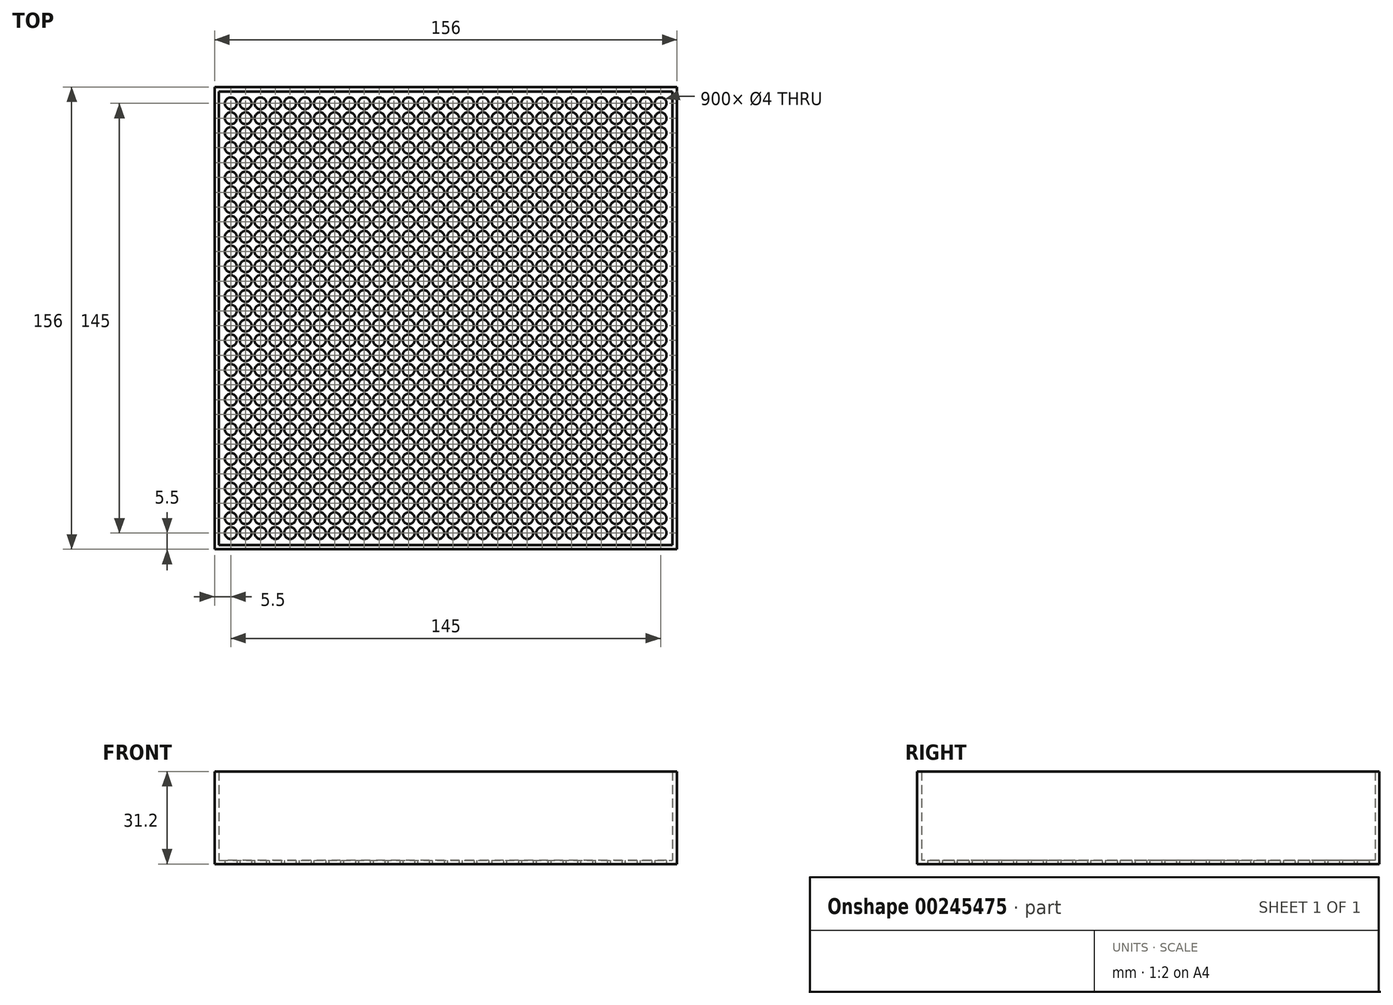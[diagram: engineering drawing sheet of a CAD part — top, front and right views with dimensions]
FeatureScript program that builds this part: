
annotation { "Feature Type Name" : "Feature", "Feature Type Description" : "" }
export const myFeature = defineFeature(function(context is Context, id is Id, definition is map)
    precondition{}
    {
        {
            var Q0;
            Q0=qCreatedBy(makeId("Top.planeOp"),FACE);
            var sketch = newSketch(context, id + "F0", { "sketchPlane" : qUnion([Q0])});
            skCircle(sketch, "E0", {"center": v(0, 0) * mm, "radius": 2 * mm});
            skCircle(sketch, "E1.0.1.0", {"center": v(0, 5) * mm, "radius": 2 * mm});
            skCircle(sketch, "E1.0.2.0", {"center": v(0, 10) * mm, "radius": 2 * mm});
            skCircle(sketch, "E1.0.3.0", {"center": v(0, 15) * mm, "radius": 2 * mm});
            skCircle(sketch, "E1.0.4.0", {"center": v(0, 20) * mm, "radius": 2 * mm});
            skCircle(sketch, "E1.0.5.0", {"center": v(0, 25) * mm, "radius": 2 * mm});
            skCircle(sketch, "E1.0.6.0", {"center": v(0, 30) * mm, "radius": 2 * mm});
            skCircle(sketch, "E1.0.7.0", {"center": v(0, 35) * mm, "radius": 2 * mm});
            skCircle(sketch, "E1.0.8.0", {"center": v(0, 40) * mm, "radius": 2 * mm});
            skCircle(sketch, "E1.0.9.0", {"center": v(0, 45) * mm, "radius": 2 * mm});
            skCircle(sketch, "E1.0.10.0", {"center": v(0, 50) * mm, "radius": 2 * mm});
            skCircle(sketch, "E1.0.11.0", {"center": v(0, 55) * mm, "radius": 2 * mm});
            skCircle(sketch, "E1.0.12.0", {"center": v(0, 60) * mm, "radius": 2 * mm});
            skCircle(sketch, "E1.0.13.0", {"center": v(0, 65) * mm, "radius": 2 * mm});
            skCircle(sketch, "E1.0.14.0", {"center": v(0, 70) * mm, "radius": 2 * mm});
            skCircle(sketch, "E1.0.15.0", {"center": v(0, 75) * mm, "radius": 2 * mm});
            skCircle(sketch, "E1.0.16.0", {"center": v(0, 80) * mm, "radius": 2 * mm});
            skCircle(sketch, "E1.0.17.0", {"center": v(0, 85) * mm, "radius": 2 * mm});
            skCircle(sketch, "E1.0.18.0", {"center": v(0, 90) * mm, "radius": 2 * mm});
            skCircle(sketch, "E1.0.19.0", {"center": v(0, 95) * mm, "radius": 2 * mm});
            skCircle(sketch, "E1.0.20.0", {"center": v(0, 100) * mm, "radius": 2 * mm});
            skCircle(sketch, "E1.0.21.0", {"center": v(0, 105) * mm, "radius": 2 * mm});
            skCircle(sketch, "E1.0.22.0", {"center": v(0, 110) * mm, "radius": 2 * mm});
            skCircle(sketch, "E1.0.23.0", {"center": v(0, 115) * mm, "radius": 2 * mm});
            skCircle(sketch, "E1.0.24.0", {"center": v(0, 120) * mm, "radius": 2 * mm});
            skCircle(sketch, "E1.0.25.0", {"center": v(0, 125) * mm, "radius": 2 * mm});
            skCircle(sketch, "E1.0.26.0", {"center": v(0, 130) * mm, "radius": 2 * mm});
            skCircle(sketch, "E1.0.27.0", {"center": v(0, 135) * mm, "radius": 2 * mm});
            skCircle(sketch, "E1.0.28.0", {"center": v(0, 140) * mm, "radius": 2 * mm});
            skCircle(sketch, "E1.0.29.0", {"center": v(0, 145) * mm, "radius": 2 * mm});
            skCircle(sketch, "E1.1.0.0", {"center": v(5, 0) * mm, "radius": 2 * mm});
            skCircle(sketch, "E1.1.1.0", {"center": v(5, 5) * mm, "radius": 2 * mm});
            skCircle(sketch, "E1.1.2.0", {"center": v(5, 10) * mm, "radius": 2 * mm});
            skCircle(sketch, "E1.1.3.0", {"center": v(5, 15) * mm, "radius": 2 * mm});
            skCircle(sketch, "E1.1.4.0", {"center": v(5, 20) * mm, "radius": 2 * mm});
            skCircle(sketch, "E1.1.5.0", {"center": v(5, 25) * mm, "radius": 2 * mm});
            skCircle(sketch, "E1.1.6.0", {"center": v(5, 30) * mm, "radius": 2 * mm});
            skCircle(sketch, "E1.1.7.0", {"center": v(5, 35) * mm, "radius": 2 * mm});
            skCircle(sketch, "E1.1.8.0", {"center": v(5, 40) * mm, "radius": 2 * mm});
            skCircle(sketch, "E1.1.9.0", {"center": v(5, 45) * mm, "radius": 2 * mm});
            skCircle(sketch, "E1.1.10.0", {"center": v(5, 50) * mm, "radius": 2 * mm});
            skCircle(sketch, "E1.1.11.0", {"center": v(5, 55) * mm, "radius": 2 * mm});
            skCircle(sketch, "E1.1.12.0", {"center": v(5, 60) * mm, "radius": 2 * mm});
            skCircle(sketch, "E1.1.13.0", {"center": v(5, 65) * mm, "radius": 2 * mm});
            skCircle(sketch, "E1.1.14.0", {"center": v(5, 70) * mm, "radius": 2 * mm});
            skCircle(sketch, "E1.1.15.0", {"center": v(5, 75) * mm, "radius": 2 * mm});
            skCircle(sketch, "E1.1.16.0", {"center": v(5, 80) * mm, "radius": 2 * mm});
            skCircle(sketch, "E1.1.17.0", {"center": v(5, 85) * mm, "radius": 2 * mm});
            skCircle(sketch, "E1.1.18.0", {"center": v(5, 90) * mm, "radius": 2 * mm});
            skCircle(sketch, "E1.1.19.0", {"center": v(5, 95) * mm, "radius": 2 * mm});
            skCircle(sketch, "E1.1.20.0", {"center": v(5, 100) * mm, "radius": 2 * mm});
            skCircle(sketch, "E1.1.21.0", {"center": v(5, 105) * mm, "radius": 2 * mm});
            skCircle(sketch, "E1.1.22.0", {"center": v(5, 110) * mm, "radius": 2 * mm});
            skCircle(sketch, "E1.1.23.0", {"center": v(5, 115) * mm, "radius": 2 * mm});
            skCircle(sketch, "E1.1.24.0", {"center": v(5, 120) * mm, "radius": 2 * mm});
            skCircle(sketch, "E1.1.25.0", {"center": v(5, 125) * mm, "radius": 2 * mm});
            skCircle(sketch, "E1.1.26.0", {"center": v(5, 130) * mm, "radius": 2 * mm});
            skCircle(sketch, "E1.1.27.0", {"center": v(5, 135) * mm, "radius": 2 * mm});
            skCircle(sketch, "E1.1.28.0", {"center": v(5, 140) * mm, "radius": 2 * mm});
            skCircle(sketch, "E1.1.29.0", {"center": v(5, 145) * mm, "radius": 2 * mm});
            skCircle(sketch, "E1.2.0.0", {"center": v(10, 0) * mm, "radius": 2 * mm});
            skCircle(sketch, "E1.2.1.0", {"center": v(10, 5) * mm, "radius": 2 * mm});
            skCircle(sketch, "E1.2.2.0", {"center": v(10, 10) * mm, "radius": 2 * mm});
            skCircle(sketch, "E1.2.3.0", {"center": v(10, 15) * mm, "radius": 2 * mm});
            skCircle(sketch, "E1.2.4.0", {"center": v(10, 20) * mm, "radius": 2 * mm});
            skCircle(sketch, "E1.2.5.0", {"center": v(10, 25) * mm, "radius": 2 * mm});
            skCircle(sketch, "E1.2.6.0", {"center": v(10, 30) * mm, "radius": 2 * mm});
            skCircle(sketch, "E1.2.7.0", {"center": v(10, 35) * mm, "radius": 2 * mm});
            skCircle(sketch, "E1.2.8.0", {"center": v(10, 40) * mm, "radius": 2 * mm});
            skCircle(sketch, "E1.2.9.0", {"center": v(10, 45) * mm, "radius": 2 * mm});
            skCircle(sketch, "E1.2.10.0", {"center": v(10, 50) * mm, "radius": 2 * mm});
            skCircle(sketch, "E1.2.11.0", {"center": v(10, 55) * mm, "radius": 2 * mm});
            skCircle(sketch, "E1.2.12.0", {"center": v(10, 60) * mm, "radius": 2 * mm});
            skCircle(sketch, "E1.2.13.0", {"center": v(10, 65) * mm, "radius": 2 * mm});
            skCircle(sketch, "E1.2.14.0", {"center": v(10, 70) * mm, "radius": 2 * mm});
            skCircle(sketch, "E1.2.15.0", {"center": v(10, 75) * mm, "radius": 2 * mm});
            skCircle(sketch, "E1.2.16.0", {"center": v(10, 80) * mm, "radius": 2 * mm});
            skCircle(sketch, "E1.2.17.0", {"center": v(10, 85) * mm, "radius": 2 * mm});
            skCircle(sketch, "E1.2.18.0", {"center": v(10, 90) * mm, "radius": 2 * mm});
            skCircle(sketch, "E1.2.19.0", {"center": v(10, 95) * mm, "radius": 2 * mm});
            skCircle(sketch, "E1.2.20.0", {"center": v(10, 100) * mm, "radius": 2 * mm});
            skCircle(sketch, "E1.2.21.0", {"center": v(10, 105) * mm, "radius": 2 * mm});
            skCircle(sketch, "E1.2.22.0", {"center": v(10, 110) * mm, "radius": 2 * mm});
            skCircle(sketch, "E1.2.23.0", {"center": v(10, 115) * mm, "radius": 2 * mm});
            skCircle(sketch, "E1.2.24.0", {"center": v(10, 120) * mm, "radius": 2 * mm});
            skCircle(sketch, "E1.2.25.0", {"center": v(10, 125) * mm, "radius": 2 * mm});
            skCircle(sketch, "E1.2.26.0", {"center": v(10, 130) * mm, "radius": 2 * mm});
            skCircle(sketch, "E1.2.27.0", {"center": v(10, 135) * mm, "radius": 2 * mm});
            skCircle(sketch, "E1.2.28.0", {"center": v(10, 140) * mm, "radius": 2 * mm});
            skCircle(sketch, "E1.2.29.0", {"center": v(10, 145) * mm, "radius": 2 * mm});
            skCircle(sketch, "E1.3.0.0", {"center": v(15, 0) * mm, "radius": 2 * mm});
            skCircle(sketch, "E1.3.1.0", {"center": v(15, 5) * mm, "radius": 2 * mm});
            skCircle(sketch, "E1.3.2.0", {"center": v(15, 10) * mm, "radius": 2 * mm});
            skCircle(sketch, "E1.3.3.0", {"center": v(15, 15) * mm, "radius": 2 * mm});
            skCircle(sketch, "E1.3.4.0", {"center": v(15, 20) * mm, "radius": 2 * mm});
            skCircle(sketch, "E1.3.5.0", {"center": v(15, 25) * mm, "radius": 2 * mm});
            skCircle(sketch, "E1.3.6.0", {"center": v(15, 30) * mm, "radius": 2 * mm});
            skCircle(sketch, "E1.3.7.0", {"center": v(15, 35) * mm, "radius": 2 * mm});
            skCircle(sketch, "E1.3.8.0", {"center": v(15, 40) * mm, "radius": 2 * mm});
            skCircle(sketch, "E1.3.9.0", {"center": v(15, 45) * mm, "radius": 2 * mm});
            skCircle(sketch, "E1.3.10.0", {"center": v(15, 50) * mm, "radius": 2 * mm});
            skCircle(sketch, "E1.3.11.0", {"center": v(15, 55) * mm, "radius": 2 * mm});
            skCircle(sketch, "E1.3.12.0", {"center": v(15, 60) * mm, "radius": 2 * mm});
            skCircle(sketch, "E1.3.13.0", {"center": v(15, 65) * mm, "radius": 2 * mm});
            skCircle(sketch, "E1.3.14.0", {"center": v(15, 70) * mm, "radius": 2 * mm});
            skCircle(sketch, "E1.3.15.0", {"center": v(15, 75) * mm, "radius": 2 * mm});
            skCircle(sketch, "E1.3.16.0", {"center": v(15, 80) * mm, "radius": 2 * mm});
            skCircle(sketch, "E1.3.17.0", {"center": v(15, 85) * mm, "radius": 2 * mm});
            skCircle(sketch, "E1.3.18.0", {"center": v(15, 90) * mm, "radius": 2 * mm});
            skCircle(sketch, "E1.3.19.0", {"center": v(15, 95) * mm, "radius": 2 * mm});
            skCircle(sketch, "E1.3.20.0", {"center": v(15, 100) * mm, "radius": 2 * mm});
            skCircle(sketch, "E1.3.21.0", {"center": v(15, 105) * mm, "radius": 2 * mm});
            skCircle(sketch, "E1.3.22.0", {"center": v(15, 110) * mm, "radius": 2 * mm});
            skCircle(sketch, "E1.3.23.0", {"center": v(15, 115) * mm, "radius": 2 * mm});
            skCircle(sketch, "E1.3.24.0", {"center": v(15, 120) * mm, "radius": 2 * mm});
            skCircle(sketch, "E1.3.25.0", {"center": v(15, 125) * mm, "radius": 2 * mm});
            skCircle(sketch, "E1.3.26.0", {"center": v(15, 130) * mm, "radius": 2 * mm});
            skCircle(sketch, "E1.3.27.0", {"center": v(15, 135) * mm, "radius": 2 * mm});
            skCircle(sketch, "E1.3.28.0", {"center": v(15, 140) * mm, "radius": 2 * mm});
            skCircle(sketch, "E1.3.29.0", {"center": v(15, 145) * mm, "radius": 2 * mm});
            skCircle(sketch, "E1.4.0.0", {"center": v(20, 0) * mm, "radius": 2 * mm});
            skCircle(sketch, "E1.4.1.0", {"center": v(20, 5) * mm, "radius": 2 * mm});
            skCircle(sketch, "E1.4.2.0", {"center": v(20, 10) * mm, "radius": 2 * mm});
            skCircle(sketch, "E1.4.3.0", {"center": v(20, 15) * mm, "radius": 2 * mm});
            skCircle(sketch, "E1.4.4.0", {"center": v(20, 20) * mm, "radius": 2 * mm});
            skCircle(sketch, "E1.4.5.0", {"center": v(20, 25) * mm, "radius": 2 * mm});
            skCircle(sketch, "E1.4.6.0", {"center": v(20, 30) * mm, "radius": 2 * mm});
            skCircle(sketch, "E1.4.7.0", {"center": v(20, 35) * mm, "radius": 2 * mm});
            skCircle(sketch, "E1.4.8.0", {"center": v(20, 40) * mm, "radius": 2 * mm});
            skCircle(sketch, "E1.4.9.0", {"center": v(20, 45) * mm, "radius": 2 * mm});
            skCircle(sketch, "E1.4.10.0", {"center": v(20, 50) * mm, "radius": 2 * mm});
            skCircle(sketch, "E1.4.11.0", {"center": v(20, 55) * mm, "radius": 2 * mm});
            skCircle(sketch, "E1.4.12.0", {"center": v(20, 60) * mm, "radius": 2 * mm});
            skCircle(sketch, "E1.4.13.0", {"center": v(20, 65) * mm, "radius": 2 * mm});
            skCircle(sketch, "E1.4.14.0", {"center": v(20, 70) * mm, "radius": 2 * mm});
            skCircle(sketch, "E1.4.15.0", {"center": v(20, 75) * mm, "radius": 2 * mm});
            skCircle(sketch, "E1.4.16.0", {"center": v(20, 80) * mm, "radius": 2 * mm});
            skCircle(sketch, "E1.4.17.0", {"center": v(20, 85) * mm, "radius": 2 * mm});
            skCircle(sketch, "E1.4.18.0", {"center": v(20, 90) * mm, "radius": 2 * mm});
            skCircle(sketch, "E1.4.19.0", {"center": v(20, 95) * mm, "radius": 2 * mm});
            skCircle(sketch, "E1.4.20.0", {"center": v(20, 100) * mm, "radius": 2 * mm});
            skCircle(sketch, "E1.4.21.0", {"center": v(20, 105) * mm, "radius": 2 * mm});
            skCircle(sketch, "E1.4.22.0", {"center": v(20, 110) * mm, "radius": 2 * mm});
            skCircle(sketch, "E1.4.23.0", {"center": v(20, 115) * mm, "radius": 2 * mm});
            skCircle(sketch, "E1.4.24.0", {"center": v(20, 120) * mm, "radius": 2 * mm});
            skCircle(sketch, "E1.4.25.0", {"center": v(20, 125) * mm, "radius": 2 * mm});
            skCircle(sketch, "E1.4.26.0", {"center": v(20, 130) * mm, "radius": 2 * mm});
            skCircle(sketch, "E1.4.27.0", {"center": v(20, 135) * mm, "radius": 2 * mm});
            skCircle(sketch, "E1.4.28.0", {"center": v(20, 140) * mm, "radius": 2 * mm});
            skCircle(sketch, "E1.4.29.0", {"center": v(20, 145) * mm, "radius": 2 * mm});
            skCircle(sketch, "E1.5.0.0", {"center": v(25, 0) * mm, "radius": 2 * mm});
            skCircle(sketch, "E1.5.1.0", {"center": v(25, 5) * mm, "radius": 2 * mm});
            skCircle(sketch, "E1.5.2.0", {"center": v(25, 10) * mm, "radius": 2 * mm});
            skCircle(sketch, "E1.5.3.0", {"center": v(25, 15) * mm, "radius": 2 * mm});
            skCircle(sketch, "E1.5.4.0", {"center": v(25, 20) * mm, "radius": 2 * mm});
            skCircle(sketch, "E1.5.5.0", {"center": v(25, 25) * mm, "radius": 2 * mm});
            skCircle(sketch, "E1.5.6.0", {"center": v(25, 30) * mm, "radius": 2 * mm});
            skCircle(sketch, "E1.5.7.0", {"center": v(25, 35) * mm, "radius": 2 * mm});
            skCircle(sketch, "E1.5.8.0", {"center": v(25, 40) * mm, "radius": 2 * mm});
            skCircle(sketch, "E1.5.9.0", {"center": v(25, 45) * mm, "radius": 2 * mm});
            skCircle(sketch, "E1.5.10.0", {"center": v(25, 50) * mm, "radius": 2 * mm});
            skCircle(sketch, "E1.5.11.0", {"center": v(25, 55) * mm, "radius": 2 * mm});
            skCircle(sketch, "E1.5.12.0", {"center": v(25, 60) * mm, "radius": 2 * mm});
            skCircle(sketch, "E1.5.13.0", {"center": v(25, 65) * mm, "radius": 2 * mm});
            skCircle(sketch, "E1.5.14.0", {"center": v(25, 70) * mm, "radius": 2 * mm});
            skCircle(sketch, "E1.5.15.0", {"center": v(25, 75) * mm, "radius": 2 * mm});
            skCircle(sketch, "E1.5.16.0", {"center": v(25, 80) * mm, "radius": 2 * mm});
            skCircle(sketch, "E1.5.17.0", {"center": v(25, 85) * mm, "radius": 2 * mm});
            skCircle(sketch, "E1.5.18.0", {"center": v(25, 90) * mm, "radius": 2 * mm});
            skCircle(sketch, "E1.5.19.0", {"center": v(25, 95) * mm, "radius": 2 * mm});
            skCircle(sketch, "E1.5.20.0", {"center": v(25, 100) * mm, "radius": 2 * mm});
            skCircle(sketch, "E1.5.21.0", {"center": v(25, 105) * mm, "radius": 2 * mm});
            skCircle(sketch, "E1.5.22.0", {"center": v(25, 110) * mm, "radius": 2 * mm});
            skCircle(sketch, "E1.5.23.0", {"center": v(25, 115) * mm, "radius": 2 * mm});
            skCircle(sketch, "E1.5.24.0", {"center": v(25, 120) * mm, "radius": 2 * mm});
            skCircle(sketch, "E1.5.25.0", {"center": v(25, 125) * mm, "radius": 2 * mm});
            skCircle(sketch, "E1.5.26.0", {"center": v(25, 130) * mm, "radius": 2 * mm});
            skCircle(sketch, "E1.5.27.0", {"center": v(25, 135) * mm, "radius": 2 * mm});
            skCircle(sketch, "E1.5.28.0", {"center": v(25, 140) * mm, "radius": 2 * mm});
            skCircle(sketch, "E1.5.29.0", {"center": v(25, 145) * mm, "radius": 2 * mm});
            skCircle(sketch, "E1.6.0.0", {"center": v(30, 0) * mm, "radius": 2 * mm});
            skCircle(sketch, "E1.6.1.0", {"center": v(30, 5) * mm, "radius": 2 * mm});
            skCircle(sketch, "E1.6.2.0", {"center": v(30, 10) * mm, "radius": 2 * mm});
            skCircle(sketch, "E1.6.3.0", {"center": v(30, 15) * mm, "radius": 2 * mm});
            skCircle(sketch, "E1.6.4.0", {"center": v(30, 20) * mm, "radius": 2 * mm});
            skCircle(sketch, "E1.6.5.0", {"center": v(30, 25) * mm, "radius": 2 * mm});
            skCircle(sketch, "E1.6.6.0", {"center": v(30, 30) * mm, "radius": 2 * mm});
            skCircle(sketch, "E1.6.7.0", {"center": v(30, 35) * mm, "radius": 2 * mm});
            skCircle(sketch, "E1.6.8.0", {"center": v(30, 40) * mm, "radius": 2 * mm});
            skCircle(sketch, "E1.6.9.0", {"center": v(30, 45) * mm, "radius": 2 * mm});
            skCircle(sketch, "E1.6.10.0", {"center": v(30, 50) * mm, "radius": 2 * mm});
            skCircle(sketch, "E1.6.11.0", {"center": v(30, 55) * mm, "radius": 2 * mm});
            skCircle(sketch, "E1.6.12.0", {"center": v(30, 60) * mm, "radius": 2 * mm});
            skCircle(sketch, "E1.6.13.0", {"center": v(30, 65) * mm, "radius": 2 * mm});
            skCircle(sketch, "E1.6.14.0", {"center": v(30, 70) * mm, "radius": 2 * mm});
            skCircle(sketch, "E1.6.15.0", {"center": v(30, 75) * mm, "radius": 2 * mm});
            skCircle(sketch, "E1.6.16.0", {"center": v(30, 80) * mm, "radius": 2 * mm});
            skCircle(sketch, "E1.6.17.0", {"center": v(30, 85) * mm, "radius": 2 * mm});
            skCircle(sketch, "E1.6.18.0", {"center": v(30, 90) * mm, "radius": 2 * mm});
            skCircle(sketch, "E1.6.19.0", {"center": v(30, 95) * mm, "radius": 2 * mm});
            skCircle(sketch, "E1.6.20.0", {"center": v(30, 100) * mm, "radius": 2 * mm});
            skCircle(sketch, "E1.6.21.0", {"center": v(30, 105) * mm, "radius": 2 * mm});
            skCircle(sketch, "E1.6.22.0", {"center": v(30, 110) * mm, "radius": 2 * mm});
            skCircle(sketch, "E1.6.23.0", {"center": v(30, 115) * mm, "radius": 2 * mm});
            skCircle(sketch, "E1.6.24.0", {"center": v(30, 120) * mm, "radius": 2 * mm});
            skCircle(sketch, "E1.6.25.0", {"center": v(30, 125) * mm, "radius": 2 * mm});
            skCircle(sketch, "E1.6.26.0", {"center": v(30, 130) * mm, "radius": 2 * mm});
            skCircle(sketch, "E1.6.27.0", {"center": v(30, 135) * mm, "radius": 2 * mm});
            skCircle(sketch, "E1.6.28.0", {"center": v(30, 140) * mm, "radius": 2 * mm});
            skCircle(sketch, "E1.6.29.0", {"center": v(30, 145) * mm, "radius": 2 * mm});
            skCircle(sketch, "E1.7.0.0", {"center": v(35, 0) * mm, "radius": 2 * mm});
            skCircle(sketch, "E1.7.1.0", {"center": v(35, 5) * mm, "radius": 2 * mm});
            skCircle(sketch, "E1.7.2.0", {"center": v(35, 10) * mm, "radius": 2 * mm});
            skCircle(sketch, "E1.7.3.0", {"center": v(35, 15) * mm, "radius": 2 * mm});
            skCircle(sketch, "E1.7.4.0", {"center": v(35, 20) * mm, "radius": 2 * mm});
            skCircle(sketch, "E1.7.5.0", {"center": v(35, 25) * mm, "radius": 2 * mm});
            skCircle(sketch, "E1.7.6.0", {"center": v(35, 30) * mm, "radius": 2 * mm});
            skCircle(sketch, "E1.7.7.0", {"center": v(35, 35) * mm, "radius": 2 * mm});
            skCircle(sketch, "E1.7.8.0", {"center": v(35, 40) * mm, "radius": 2 * mm});
            skCircle(sketch, "E1.7.9.0", {"center": v(35, 45) * mm, "radius": 2 * mm});
            skCircle(sketch, "E1.7.10.0", {"center": v(35, 50) * mm, "radius": 2 * mm});
            skCircle(sketch, "E1.7.11.0", {"center": v(35, 55) * mm, "radius": 2 * mm});
            skCircle(sketch, "E1.7.12.0", {"center": v(35, 60) * mm, "radius": 2 * mm});
            skCircle(sketch, "E1.7.13.0", {"center": v(35, 65) * mm, "radius": 2 * mm});
            skCircle(sketch, "E1.7.14.0", {"center": v(35, 70) * mm, "radius": 2 * mm});
            skCircle(sketch, "E1.7.15.0", {"center": v(35, 75) * mm, "radius": 2 * mm});
            skCircle(sketch, "E1.7.16.0", {"center": v(35, 80) * mm, "radius": 2 * mm});
            skCircle(sketch, "E1.7.17.0", {"center": v(35, 85) * mm, "radius": 2 * mm});
            skCircle(sketch, "E1.7.18.0", {"center": v(35, 90) * mm, "radius": 2 * mm});
            skCircle(sketch, "E1.7.19.0", {"center": v(35, 95) * mm, "radius": 2 * mm});
            skCircle(sketch, "E1.7.20.0", {"center": v(35, 100) * mm, "radius": 2 * mm});
            skCircle(sketch, "E1.7.21.0", {"center": v(35, 105) * mm, "radius": 2 * mm});
            skCircle(sketch, "E1.7.22.0", {"center": v(35, 110) * mm, "radius": 2 * mm});
            skCircle(sketch, "E1.7.23.0", {"center": v(35, 115) * mm, "radius": 2 * mm});
            skCircle(sketch, "E1.7.24.0", {"center": v(35, 120) * mm, "radius": 2 * mm});
            skCircle(sketch, "E1.7.25.0", {"center": v(35, 125) * mm, "radius": 2 * mm});
            skCircle(sketch, "E1.7.26.0", {"center": v(35, 130) * mm, "radius": 2 * mm});
            skCircle(sketch, "E1.7.27.0", {"center": v(35, 135) * mm, "radius": 2 * mm});
            skCircle(sketch, "E1.7.28.0", {"center": v(35, 140) * mm, "radius": 2 * mm});
            skCircle(sketch, "E1.7.29.0", {"center": v(35, 145) * mm, "radius": 2 * mm});
            skCircle(sketch, "E1.8.0.0", {"center": v(40, 0) * mm, "radius": 2 * mm});
            skCircle(sketch, "E1.8.1.0", {"center": v(40, 5) * mm, "radius": 2 * mm});
            skCircle(sketch, "E1.8.2.0", {"center": v(40, 10) * mm, "radius": 2 * mm});
            skCircle(sketch, "E1.8.3.0", {"center": v(40, 15) * mm, "radius": 2 * mm});
            skCircle(sketch, "E1.8.4.0", {"center": v(40, 20) * mm, "radius": 2 * mm});
            skCircle(sketch, "E1.8.5.0", {"center": v(40, 25) * mm, "radius": 2 * mm});
            skCircle(sketch, "E1.8.6.0", {"center": v(40, 30) * mm, "radius": 2 * mm});
            skCircle(sketch, "E1.8.7.0", {"center": v(40, 35) * mm, "radius": 2 * mm});
            skCircle(sketch, "E1.8.8.0", {"center": v(40, 40) * mm, "radius": 2 * mm});
            skCircle(sketch, "E1.8.9.0", {"center": v(40, 45) * mm, "radius": 2 * mm});
            skCircle(sketch, "E1.8.10.0", {"center": v(40, 50) * mm, "radius": 2 * mm});
            skCircle(sketch, "E1.8.11.0", {"center": v(40, 55) * mm, "radius": 2 * mm});
            skCircle(sketch, "E1.8.12.0", {"center": v(40, 60) * mm, "radius": 2 * mm});
            skCircle(sketch, "E1.8.13.0", {"center": v(40, 65) * mm, "radius": 2 * mm});
            skCircle(sketch, "E1.8.14.0", {"center": v(40, 70) * mm, "radius": 2 * mm});
            skCircle(sketch, "E1.8.15.0", {"center": v(40, 75) * mm, "radius": 2 * mm});
            skCircle(sketch, "E1.8.16.0", {"center": v(40, 80) * mm, "radius": 2 * mm});
            skCircle(sketch, "E1.8.17.0", {"center": v(40, 85) * mm, "radius": 2 * mm});
            skCircle(sketch, "E1.8.18.0", {"center": v(40, 90) * mm, "radius": 2 * mm});
            skCircle(sketch, "E1.8.19.0", {"center": v(40, 95) * mm, "radius": 2 * mm});
            skCircle(sketch, "E1.8.20.0", {"center": v(40, 100) * mm, "radius": 2 * mm});
            skCircle(sketch, "E1.8.21.0", {"center": v(40, 105) * mm, "radius": 2 * mm});
            skCircle(sketch, "E1.8.22.0", {"center": v(40, 110) * mm, "radius": 2 * mm});
            skCircle(sketch, "E1.8.23.0", {"center": v(40, 115) * mm, "radius": 2 * mm});
            skCircle(sketch, "E1.8.24.0", {"center": v(40, 120) * mm, "radius": 2 * mm});
            skCircle(sketch, "E1.8.25.0", {"center": v(40, 125) * mm, "radius": 2 * mm});
            skCircle(sketch, "E1.8.26.0", {"center": v(40, 130) * mm, "radius": 2 * mm});
            skCircle(sketch, "E1.8.27.0", {"center": v(40, 135) * mm, "radius": 2 * mm});
            skCircle(sketch, "E1.8.28.0", {"center": v(40, 140) * mm, "radius": 2 * mm});
            skCircle(sketch, "E1.8.29.0", {"center": v(40, 145) * mm, "radius": 2 * mm});
            skCircle(sketch, "E1.9.0.0", {"center": v(45, 0) * mm, "radius": 2 * mm});
            skCircle(sketch, "E1.9.1.0", {"center": v(45, 5) * mm, "radius": 2 * mm});
            skCircle(sketch, "E1.9.2.0", {"center": v(45, 10) * mm, "radius": 2 * mm});
            skCircle(sketch, "E1.9.3.0", {"center": v(45, 15) * mm, "radius": 2 * mm});
            skCircle(sketch, "E1.9.4.0", {"center": v(45, 20) * mm, "radius": 2 * mm});
            skCircle(sketch, "E1.9.5.0", {"center": v(45, 25) * mm, "radius": 2 * mm});
            skCircle(sketch, "E1.9.6.0", {"center": v(45, 30) * mm, "radius": 2 * mm});
            skCircle(sketch, "E1.9.7.0", {"center": v(45, 35) * mm, "radius": 2 * mm});
            skCircle(sketch, "E1.9.8.0", {"center": v(45, 40) * mm, "radius": 2 * mm});
            skCircle(sketch, "E1.9.9.0", {"center": v(45, 45) * mm, "radius": 2 * mm});
            skCircle(sketch, "E1.9.10.0", {"center": v(45, 50) * mm, "radius": 2 * mm});
            skCircle(sketch, "E1.9.11.0", {"center": v(45, 55) * mm, "radius": 2 * mm});
            skCircle(sketch, "E1.9.12.0", {"center": v(45, 60) * mm, "radius": 2 * mm});
            skCircle(sketch, "E1.9.13.0", {"center": v(45, 65) * mm, "radius": 2 * mm});
            skCircle(sketch, "E1.9.14.0", {"center": v(45, 70) * mm, "radius": 2 * mm});
            skCircle(sketch, "E1.9.15.0", {"center": v(45, 75) * mm, "radius": 2 * mm});
            skCircle(sketch, "E1.9.16.0", {"center": v(45, 80) * mm, "radius": 2 * mm});
            skCircle(sketch, "E1.9.17.0", {"center": v(45, 85) * mm, "radius": 2 * mm});
            skCircle(sketch, "E1.9.18.0", {"center": v(45, 90) * mm, "radius": 2 * mm});
            skCircle(sketch, "E1.9.19.0", {"center": v(45, 95) * mm, "radius": 2 * mm});
            skCircle(sketch, "E1.9.20.0", {"center": v(45, 100) * mm, "radius": 2 * mm});
            skCircle(sketch, "E1.9.21.0", {"center": v(45, 105) * mm, "radius": 2 * mm});
            skCircle(sketch, "E1.9.22.0", {"center": v(45, 110) * mm, "radius": 2 * mm});
            skCircle(sketch, "E1.9.23.0", {"center": v(45, 115) * mm, "radius": 2 * mm});
            skCircle(sketch, "E1.9.24.0", {"center": v(45, 120) * mm, "radius": 2 * mm});
            skCircle(sketch, "E1.9.25.0", {"center": v(45, 125) * mm, "radius": 2 * mm});
            skCircle(sketch, "E1.9.26.0", {"center": v(45, 130) * mm, "radius": 2 * mm});
            skCircle(sketch, "E1.9.27.0", {"center": v(45, 135) * mm, "radius": 2 * mm});
            skCircle(sketch, "E1.9.28.0", {"center": v(45, 140) * mm, "radius": 2 * mm});
            skCircle(sketch, "E1.9.29.0", {"center": v(45, 145) * mm, "radius": 2 * mm});
            skCircle(sketch, "E1.10.0.0", {"center": v(50, 0) * mm, "radius": 2 * mm});
            skCircle(sketch, "E1.10.1.0", {"center": v(50, 5) * mm, "radius": 2 * mm});
            skCircle(sketch, "E1.10.2.0", {"center": v(50, 10) * mm, "radius": 2 * mm});
            skCircle(sketch, "E1.10.3.0", {"center": v(50, 15) * mm, "radius": 2 * mm});
            skCircle(sketch, "E1.10.4.0", {"center": v(50, 20) * mm, "radius": 2 * mm});
            skCircle(sketch, "E1.10.5.0", {"center": v(50, 25) * mm, "radius": 2 * mm});
            skCircle(sketch, "E1.10.6.0", {"center": v(50, 30) * mm, "radius": 2 * mm});
            skCircle(sketch, "E1.10.7.0", {"center": v(50, 35) * mm, "radius": 2 * mm});
            skCircle(sketch, "E1.10.8.0", {"center": v(50, 40) * mm, "radius": 2 * mm});
            skCircle(sketch, "E1.10.9.0", {"center": v(50, 45) * mm, "radius": 2 * mm});
            skCircle(sketch, "E1.10.10.0", {"center": v(50, 50) * mm, "radius": 2 * mm});
            skCircle(sketch, "E1.10.11.0", {"center": v(50, 55) * mm, "radius": 2 * mm});
            skCircle(sketch, "E1.10.12.0", {"center": v(50, 60) * mm, "radius": 2 * mm});
            skCircle(sketch, "E1.10.13.0", {"center": v(50, 65) * mm, "radius": 2 * mm});
            skCircle(sketch, "E1.10.14.0", {"center": v(50, 70) * mm, "radius": 2 * mm});
            skCircle(sketch, "E1.10.15.0", {"center": v(50, 75) * mm, "radius": 2 * mm});
            skCircle(sketch, "E1.10.16.0", {"center": v(50, 80) * mm, "radius": 2 * mm});
            skCircle(sketch, "E1.10.17.0", {"center": v(50, 85) * mm, "radius": 2 * mm});
            skCircle(sketch, "E1.10.18.0", {"center": v(50, 90) * mm, "radius": 2 * mm});
            skCircle(sketch, "E1.10.19.0", {"center": v(50, 95) * mm, "radius": 2 * mm});
            skCircle(sketch, "E1.10.20.0", {"center": v(50, 100) * mm, "radius": 2 * mm});
            skCircle(sketch, "E1.10.21.0", {"center": v(50, 105) * mm, "radius": 2 * mm});
            skCircle(sketch, "E1.10.22.0", {"center": v(50, 110) * mm, "radius": 2 * mm});
            skCircle(sketch, "E1.10.23.0", {"center": v(50, 115) * mm, "radius": 2 * mm});
            skCircle(sketch, "E1.10.24.0", {"center": v(50, 120) * mm, "radius": 2 * mm});
            skCircle(sketch, "E1.10.25.0", {"center": v(50, 125) * mm, "radius": 2 * mm});
            skCircle(sketch, "E1.10.26.0", {"center": v(50, 130) * mm, "radius": 2 * mm});
            skCircle(sketch, "E1.10.27.0", {"center": v(50, 135) * mm, "radius": 2 * mm});
            skCircle(sketch, "E1.10.28.0", {"center": v(50, 140) * mm, "radius": 2 * mm});
            skCircle(sketch, "E1.10.29.0", {"center": v(50, 145) * mm, "radius": 2 * mm});
            skCircle(sketch, "E1.11.0.0", {"center": v(55, 0) * mm, "radius": 2 * mm});
            skCircle(sketch, "E1.11.1.0", {"center": v(55, 5) * mm, "radius": 2 * mm});
            skCircle(sketch, "E1.11.2.0", {"center": v(55, 10) * mm, "radius": 2 * mm});
            skCircle(sketch, "E1.11.3.0", {"center": v(55, 15) * mm, "radius": 2 * mm});
            skCircle(sketch, "E1.11.4.0", {"center": v(55, 20) * mm, "radius": 2 * mm});
            skCircle(sketch, "E1.11.5.0", {"center": v(55, 25) * mm, "radius": 2 * mm});
            skCircle(sketch, "E1.11.6.0", {"center": v(55, 30) * mm, "radius": 2 * mm});
            skCircle(sketch, "E1.11.7.0", {"center": v(55, 35) * mm, "radius": 2 * mm});
            skCircle(sketch, "E1.11.8.0", {"center": v(55, 40) * mm, "radius": 2 * mm});
            skCircle(sketch, "E1.11.9.0", {"center": v(55, 45) * mm, "radius": 2 * mm});
            skCircle(sketch, "E1.11.10.0", {"center": v(55, 50) * mm, "radius": 2 * mm});
            skCircle(sketch, "E1.11.11.0", {"center": v(55, 55) * mm, "radius": 2 * mm});
            skCircle(sketch, "E1.11.12.0", {"center": v(55, 60) * mm, "radius": 2 * mm});
            skCircle(sketch, "E1.11.13.0", {"center": v(55, 65) * mm, "radius": 2 * mm});
            skCircle(sketch, "E1.11.14.0", {"center": v(55, 70) * mm, "radius": 2 * mm});
            skCircle(sketch, "E1.11.15.0", {"center": v(55, 75) * mm, "radius": 2 * mm});
            skCircle(sketch, "E1.11.16.0", {"center": v(55, 80) * mm, "radius": 2 * mm});
            skCircle(sketch, "E1.11.17.0", {"center": v(55, 85) * mm, "radius": 2 * mm});
            skCircle(sketch, "E1.11.18.0", {"center": v(55, 90) * mm, "radius": 2 * mm});
            skCircle(sketch, "E1.11.19.0", {"center": v(55, 95) * mm, "radius": 2 * mm});
            skCircle(sketch, "E1.11.20.0", {"center": v(55, 100) * mm, "radius": 2 * mm});
            skCircle(sketch, "E1.11.21.0", {"center": v(55, 105) * mm, "radius": 2 * mm});
            skCircle(sketch, "E1.11.22.0", {"center": v(55, 110) * mm, "radius": 2 * mm});
            skCircle(sketch, "E1.11.23.0", {"center": v(55, 115) * mm, "radius": 2 * mm});
            skCircle(sketch, "E1.11.24.0", {"center": v(55, 120) * mm, "radius": 2 * mm});
            skCircle(sketch, "E1.11.25.0", {"center": v(55, 125) * mm, "radius": 2 * mm});
            skCircle(sketch, "E1.11.26.0", {"center": v(55, 130) * mm, "radius": 2 * mm});
            skCircle(sketch, "E1.11.27.0", {"center": v(55, 135) * mm, "radius": 2 * mm});
            skCircle(sketch, "E1.11.28.0", {"center": v(55, 140) * mm, "radius": 2 * mm});
            skCircle(sketch, "E1.11.29.0", {"center": v(55, 145) * mm, "radius": 2 * mm});
            skCircle(sketch, "E1.12.0.0", {"center": v(60, 0) * mm, "radius": 2 * mm});
            skCircle(sketch, "E1.12.1.0", {"center": v(60, 5) * mm, "radius": 2 * mm});
            skCircle(sketch, "E1.12.2.0", {"center": v(60, 10) * mm, "radius": 2 * mm});
            skCircle(sketch, "E1.12.3.0", {"center": v(60, 15) * mm, "radius": 2 * mm});
            skCircle(sketch, "E1.12.4.0", {"center": v(60, 20) * mm, "radius": 2 * mm});
            skCircle(sketch, "E1.12.5.0", {"center": v(60, 25) * mm, "radius": 2 * mm});
            skCircle(sketch, "E1.12.6.0", {"center": v(60, 30) * mm, "radius": 2 * mm});
            skCircle(sketch, "E1.12.7.0", {"center": v(60, 35) * mm, "radius": 2 * mm});
            skCircle(sketch, "E1.12.8.0", {"center": v(60, 40) * mm, "radius": 2 * mm});
            skCircle(sketch, "E1.12.9.0", {"center": v(60, 45) * mm, "radius": 2 * mm});
            skCircle(sketch, "E1.12.10.0", {"center": v(60, 50) * mm, "radius": 2 * mm});
            skCircle(sketch, "E1.12.11.0", {"center": v(60, 55) * mm, "radius": 2 * mm});
            skCircle(sketch, "E1.12.12.0", {"center": v(60, 60) * mm, "radius": 2 * mm});
            skCircle(sketch, "E1.12.13.0", {"center": v(60, 65) * mm, "radius": 2 * mm});
            skCircle(sketch, "E1.12.14.0", {"center": v(60, 70) * mm, "radius": 2 * mm});
            skCircle(sketch, "E1.12.15.0", {"center": v(60, 75) * mm, "radius": 2 * mm});
            skCircle(sketch, "E1.12.16.0", {"center": v(60, 80) * mm, "radius": 2 * mm});
            skCircle(sketch, "E1.12.17.0", {"center": v(60, 85) * mm, "radius": 2 * mm});
            skCircle(sketch, "E1.12.18.0", {"center": v(60, 90) * mm, "radius": 2 * mm});
            skCircle(sketch, "E1.12.19.0", {"center": v(60, 95) * mm, "radius": 2 * mm});
            skCircle(sketch, "E1.12.20.0", {"center": v(60, 100) * mm, "radius": 2 * mm});
            skCircle(sketch, "E1.12.21.0", {"center": v(60, 105) * mm, "radius": 2 * mm});
            skCircle(sketch, "E1.12.22.0", {"center": v(60, 110) * mm, "radius": 2 * mm});
            skCircle(sketch, "E1.12.23.0", {"center": v(60, 115) * mm, "radius": 2 * mm});
            skCircle(sketch, "E1.12.24.0", {"center": v(60, 120) * mm, "radius": 2 * mm});
            skCircle(sketch, "E1.12.25.0", {"center": v(60, 125) * mm, "radius": 2 * mm});
            skCircle(sketch, "E1.12.26.0", {"center": v(60, 130) * mm, "radius": 2 * mm});
            skCircle(sketch, "E1.12.27.0", {"center": v(60, 135) * mm, "radius": 2 * mm});
            skCircle(sketch, "E1.12.28.0", {"center": v(60, 140) * mm, "radius": 2 * mm});
            skCircle(sketch, "E1.12.29.0", {"center": v(60, 145) * mm, "radius": 2 * mm});
            skCircle(sketch, "E1.13.0.0", {"center": v(65, 0) * mm, "radius": 2 * mm});
            skCircle(sketch, "E1.13.1.0", {"center": v(65, 5) * mm, "radius": 2 * mm});
            skCircle(sketch, "E1.13.2.0", {"center": v(65, 10) * mm, "radius": 2 * mm});
            skCircle(sketch, "E1.13.3.0", {"center": v(65, 15) * mm, "radius": 2 * mm});
            skCircle(sketch, "E1.13.4.0", {"center": v(65, 20) * mm, "radius": 2 * mm});
            skCircle(sketch, "E1.13.5.0", {"center": v(65, 25) * mm, "radius": 2 * mm});
            skCircle(sketch, "E1.13.6.0", {"center": v(65, 30) * mm, "radius": 2 * mm});
            skCircle(sketch, "E1.13.7.0", {"center": v(65, 35) * mm, "radius": 2 * mm});
            skCircle(sketch, "E1.13.8.0", {"center": v(65, 40) * mm, "radius": 2 * mm});
            skCircle(sketch, "E1.13.9.0", {"center": v(65, 45) * mm, "radius": 2 * mm});
            skCircle(sketch, "E1.13.10.0", {"center": v(65, 50) * mm, "radius": 2 * mm});
            skCircle(sketch, "E1.13.11.0", {"center": v(65, 55) * mm, "radius": 2 * mm});
            skCircle(sketch, "E1.13.12.0", {"center": v(65, 60) * mm, "radius": 2 * mm});
            skCircle(sketch, "E1.13.13.0", {"center": v(65, 65) * mm, "radius": 2 * mm});
            skCircle(sketch, "E1.13.14.0", {"center": v(65, 70) * mm, "radius": 2 * mm});
            skCircle(sketch, "E1.13.15.0", {"center": v(65, 75) * mm, "radius": 2 * mm});
            skCircle(sketch, "E1.13.16.0", {"center": v(65, 80) * mm, "radius": 2 * mm});
            skCircle(sketch, "E1.13.17.0", {"center": v(65, 85) * mm, "radius": 2 * mm});
            skCircle(sketch, "E1.13.18.0", {"center": v(65, 90) * mm, "radius": 2 * mm});
            skCircle(sketch, "E1.13.19.0", {"center": v(65, 95) * mm, "radius": 2 * mm});
            skCircle(sketch, "E1.13.20.0", {"center": v(65, 100) * mm, "radius": 2 * mm});
            skCircle(sketch, "E1.13.21.0", {"center": v(65, 105) * mm, "radius": 2 * mm});
            skCircle(sketch, "E1.13.22.0", {"center": v(65, 110) * mm, "radius": 2 * mm});
            skCircle(sketch, "E1.13.23.0", {"center": v(65, 115) * mm, "radius": 2 * mm});
            skCircle(sketch, "E1.13.24.0", {"center": v(65, 120) * mm, "radius": 2 * mm});
            skCircle(sketch, "E1.13.25.0", {"center": v(65, 125) * mm, "radius": 2 * mm});
            skCircle(sketch, "E1.13.26.0", {"center": v(65, 130) * mm, "radius": 2 * mm});
            skCircle(sketch, "E1.13.27.0", {"center": v(65, 135) * mm, "radius": 2 * mm});
            skCircle(sketch, "E1.13.28.0", {"center": v(65, 140) * mm, "radius": 2 * mm});
            skCircle(sketch, "E1.13.29.0", {"center": v(65, 145) * mm, "radius": 2 * mm});
            skCircle(sketch, "E1.14.0.0", {"center": v(70, 0) * mm, "radius": 2 * mm});
            skCircle(sketch, "E1.14.1.0", {"center": v(70, 5) * mm, "radius": 2 * mm});
            skCircle(sketch, "E1.14.2.0", {"center": v(70, 10) * mm, "radius": 2 * mm});
            skCircle(sketch, "E1.14.3.0", {"center": v(70, 15) * mm, "radius": 2 * mm});
            skCircle(sketch, "E1.14.4.0", {"center": v(70, 20) * mm, "radius": 2 * mm});
            skCircle(sketch, "E1.14.5.0", {"center": v(70, 25) * mm, "radius": 2 * mm});
            skCircle(sketch, "E1.14.6.0", {"center": v(70, 30) * mm, "radius": 2 * mm});
            skCircle(sketch, "E1.14.7.0", {"center": v(70, 35) * mm, "radius": 2 * mm});
            skCircle(sketch, "E1.14.8.0", {"center": v(70, 40) * mm, "radius": 2 * mm});
            skCircle(sketch, "E1.14.9.0", {"center": v(70, 45) * mm, "radius": 2 * mm});
            skCircle(sketch, "E1.14.10.0", {"center": v(70, 50) * mm, "radius": 2 * mm});
            skCircle(sketch, "E1.14.11.0", {"center": v(70, 55) * mm, "radius": 2 * mm});
            skCircle(sketch, "E1.14.12.0", {"center": v(70, 60) * mm, "radius": 2 * mm});
            skCircle(sketch, "E1.14.13.0", {"center": v(70, 65) * mm, "radius": 2 * mm});
            skCircle(sketch, "E1.14.14.0", {"center": v(70, 70) * mm, "radius": 2 * mm});
            skCircle(sketch, "E1.14.15.0", {"center": v(70, 75) * mm, "radius": 2 * mm});
            skCircle(sketch, "E1.14.16.0", {"center": v(70, 80) * mm, "radius": 2 * mm});
            skCircle(sketch, "E1.14.17.0", {"center": v(70, 85) * mm, "radius": 2 * mm});
            skCircle(sketch, "E1.14.18.0", {"center": v(70, 90) * mm, "radius": 2 * mm});
            skCircle(sketch, "E1.14.19.0", {"center": v(70, 95) * mm, "radius": 2 * mm});
            skCircle(sketch, "E1.14.20.0", {"center": v(70, 100) * mm, "radius": 2 * mm});
            skCircle(sketch, "E1.14.21.0", {"center": v(70, 105) * mm, "radius": 2 * mm});
            skCircle(sketch, "E1.14.22.0", {"center": v(70, 110) * mm, "radius": 2 * mm});
            skCircle(sketch, "E1.14.23.0", {"center": v(70, 115) * mm, "radius": 2 * mm});
            skCircle(sketch, "E1.14.24.0", {"center": v(70, 120) * mm, "radius": 2 * mm});
            skCircle(sketch, "E1.14.25.0", {"center": v(70, 125) * mm, "radius": 2 * mm});
            skCircle(sketch, "E1.14.26.0", {"center": v(70, 130) * mm, "radius": 2 * mm});
            skCircle(sketch, "E1.14.27.0", {"center": v(70, 135) * mm, "radius": 2 * mm});
            skCircle(sketch, "E1.14.28.0", {"center": v(70, 140) * mm, "radius": 2 * mm});
            skCircle(sketch, "E1.14.29.0", {"center": v(70, 145) * mm, "radius": 2 * mm});
            skCircle(sketch, "E1.15.0.0", {"center": v(75, 0) * mm, "radius": 2 * mm});
            skCircle(sketch, "E1.15.1.0", {"center": v(75, 5) * mm, "radius": 2 * mm});
            skCircle(sketch, "E1.15.2.0", {"center": v(75, 10) * mm, "radius": 2 * mm});
            skCircle(sketch, "E1.15.3.0", {"center": v(75, 15) * mm, "radius": 2 * mm});
            skCircle(sketch, "E1.15.4.0", {"center": v(75, 20) * mm, "radius": 2 * mm});
            skCircle(sketch, "E1.15.5.0", {"center": v(75, 25) * mm, "radius": 2 * mm});
            skCircle(sketch, "E1.15.6.0", {"center": v(75, 30) * mm, "radius": 2 * mm});
            skCircle(sketch, "E1.15.7.0", {"center": v(75, 35) * mm, "radius": 2 * mm});
            skCircle(sketch, "E1.15.8.0", {"center": v(75, 40) * mm, "radius": 2 * mm});
            skCircle(sketch, "E1.15.9.0", {"center": v(75, 45) * mm, "radius": 2 * mm});
            skCircle(sketch, "E1.15.10.0", {"center": v(75, 50) * mm, "radius": 2 * mm});
            skCircle(sketch, "E1.15.11.0", {"center": v(75, 55) * mm, "radius": 2 * mm});
            skCircle(sketch, "E1.15.12.0", {"center": v(75, 60) * mm, "radius": 2 * mm});
            skCircle(sketch, "E1.15.13.0", {"center": v(75, 65) * mm, "radius": 2 * mm});
            skCircle(sketch, "E1.15.14.0", {"center": v(75, 70) * mm, "radius": 2 * mm});
            skCircle(sketch, "E1.15.15.0", {"center": v(75, 75) * mm, "radius": 2 * mm});
            skCircle(sketch, "E1.15.16.0", {"center": v(75, 80) * mm, "radius": 2 * mm});
            skCircle(sketch, "E1.15.17.0", {"center": v(75, 85) * mm, "radius": 2 * mm});
            skCircle(sketch, "E1.15.18.0", {"center": v(75, 90) * mm, "radius": 2 * mm});
            skCircle(sketch, "E1.15.19.0", {"center": v(75, 95) * mm, "radius": 2 * mm});
            skCircle(sketch, "E1.15.20.0", {"center": v(75, 100) * mm, "radius": 2 * mm});
            skCircle(sketch, "E1.15.21.0", {"center": v(75, 105) * mm, "radius": 2 * mm});
            skCircle(sketch, "E1.15.22.0", {"center": v(75, 110) * mm, "radius": 2 * mm});
            skCircle(sketch, "E1.15.23.0", {"center": v(75, 115) * mm, "radius": 2 * mm});
            skCircle(sketch, "E1.15.24.0", {"center": v(75, 120) * mm, "radius": 2 * mm});
            skCircle(sketch, "E1.15.25.0", {"center": v(75, 125) * mm, "radius": 2 * mm});
            skCircle(sketch, "E1.15.26.0", {"center": v(75, 130) * mm, "radius": 2 * mm});
            skCircle(sketch, "E1.15.27.0", {"center": v(75, 135) * mm, "radius": 2 * mm});
            skCircle(sketch, "E1.15.28.0", {"center": v(75, 140) * mm, "radius": 2 * mm});
            skCircle(sketch, "E1.15.29.0", {"center": v(75, 145) * mm, "radius": 2 * mm});
            skCircle(sketch, "E1.16.0.0", {"center": v(80, 0) * mm, "radius": 2 * mm});
            skCircle(sketch, "E1.16.1.0", {"center": v(80, 5) * mm, "radius": 2 * mm});
            skCircle(sketch, "E1.16.2.0", {"center": v(80, 10) * mm, "radius": 2 * mm});
            skCircle(sketch, "E1.16.3.0", {"center": v(80, 15) * mm, "radius": 2 * mm});
            skCircle(sketch, "E1.16.4.0", {"center": v(80, 20) * mm, "radius": 2 * mm});
            skCircle(sketch, "E1.16.5.0", {"center": v(80, 25) * mm, "radius": 2 * mm});
            skCircle(sketch, "E1.16.6.0", {"center": v(80, 30) * mm, "radius": 2 * mm});
            skCircle(sketch, "E1.16.7.0", {"center": v(80, 35) * mm, "radius": 2 * mm});
            skCircle(sketch, "E1.16.8.0", {"center": v(80, 40) * mm, "radius": 2 * mm});
            skCircle(sketch, "E1.16.9.0", {"center": v(80, 45) * mm, "radius": 2 * mm});
            skCircle(sketch, "E1.16.10.0", {"center": v(80, 50) * mm, "radius": 2 * mm});
            skCircle(sketch, "E1.16.11.0", {"center": v(80, 55) * mm, "radius": 2 * mm});
            skCircle(sketch, "E1.16.12.0", {"center": v(80, 60) * mm, "radius": 2 * mm});
            skCircle(sketch, "E1.16.13.0", {"center": v(80, 65) * mm, "radius": 2 * mm});
            skCircle(sketch, "E1.16.14.0", {"center": v(80, 70) * mm, "radius": 2 * mm});
            skCircle(sketch, "E1.16.15.0", {"center": v(80, 75) * mm, "radius": 2 * mm});
            skCircle(sketch, "E1.16.16.0", {"center": v(80, 80) * mm, "radius": 2 * mm});
            skCircle(sketch, "E1.16.17.0", {"center": v(80, 85) * mm, "radius": 2 * mm});
            skCircle(sketch, "E1.16.18.0", {"center": v(80, 90) * mm, "radius": 2 * mm});
            skCircle(sketch, "E1.16.19.0", {"center": v(80, 95) * mm, "radius": 2 * mm});
            skCircle(sketch, "E1.16.20.0", {"center": v(80, 100) * mm, "radius": 2 * mm});
            skCircle(sketch, "E1.16.21.0", {"center": v(80, 105) * mm, "radius": 2 * mm});
            skCircle(sketch, "E1.16.22.0", {"center": v(80, 110) * mm, "radius": 2 * mm});
            skCircle(sketch, "E1.16.23.0", {"center": v(80, 115) * mm, "radius": 2 * mm});
            skCircle(sketch, "E1.16.24.0", {"center": v(80, 120) * mm, "radius": 2 * mm});
            skCircle(sketch, "E1.16.25.0", {"center": v(80, 125) * mm, "radius": 2 * mm});
            skCircle(sketch, "E1.16.26.0", {"center": v(80, 130) * mm, "radius": 2 * mm});
            skCircle(sketch, "E1.16.27.0", {"center": v(80, 135) * mm, "radius": 2 * mm});
            skCircle(sketch, "E1.16.28.0", {"center": v(80, 140) * mm, "radius": 2 * mm});
            skCircle(sketch, "E1.16.29.0", {"center": v(80, 145) * mm, "radius": 2 * mm});
            skCircle(sketch, "E1.17.0.0", {"center": v(85, 0) * mm, "radius": 2 * mm});
            skCircle(sketch, "E1.17.1.0", {"center": v(85, 5) * mm, "radius": 2 * mm});
            skCircle(sketch, "E1.17.2.0", {"center": v(85, 10) * mm, "radius": 2 * mm});
            skCircle(sketch, "E1.17.3.0", {"center": v(85, 15) * mm, "radius": 2 * mm});
            skCircle(sketch, "E1.17.4.0", {"center": v(85, 20) * mm, "radius": 2 * mm});
            skCircle(sketch, "E1.17.5.0", {"center": v(85, 25) * mm, "radius": 2 * mm});
            skCircle(sketch, "E1.17.6.0", {"center": v(85, 30) * mm, "radius": 2 * mm});
            skCircle(sketch, "E1.17.7.0", {"center": v(85, 35) * mm, "radius": 2 * mm});
            skCircle(sketch, "E1.17.8.0", {"center": v(85, 40) * mm, "radius": 2 * mm});
            skCircle(sketch, "E1.17.9.0", {"center": v(85, 45) * mm, "radius": 2 * mm});
            skCircle(sketch, "E1.17.10.0", {"center": v(85, 50) * mm, "radius": 2 * mm});
            skCircle(sketch, "E1.17.11.0", {"center": v(85, 55) * mm, "radius": 2 * mm});
            skCircle(sketch, "E1.17.12.0", {"center": v(85, 60) * mm, "radius": 2 * mm});
            skCircle(sketch, "E1.17.13.0", {"center": v(85, 65) * mm, "radius": 2 * mm});
            skCircle(sketch, "E1.17.14.0", {"center": v(85, 70) * mm, "radius": 2 * mm});
            skCircle(sketch, "E1.17.15.0", {"center": v(85, 75) * mm, "radius": 2 * mm});
            skCircle(sketch, "E1.17.16.0", {"center": v(85, 80) * mm, "radius": 2 * mm});
            skCircle(sketch, "E1.17.17.0", {"center": v(85, 85) * mm, "radius": 2 * mm});
            skCircle(sketch, "E1.17.18.0", {"center": v(85, 90) * mm, "radius": 2 * mm});
            skCircle(sketch, "E1.17.19.0", {"center": v(85, 95) * mm, "radius": 2 * mm});
            skCircle(sketch, "E1.17.20.0", {"center": v(85, 100) * mm, "radius": 2 * mm});
            skCircle(sketch, "E1.17.21.0", {"center": v(85, 105) * mm, "radius": 2 * mm});
            skCircle(sketch, "E1.17.22.0", {"center": v(85, 110) * mm, "radius": 2 * mm});
            skCircle(sketch, "E1.17.23.0", {"center": v(85, 115) * mm, "radius": 2 * mm});
            skCircle(sketch, "E1.17.24.0", {"center": v(85, 120) * mm, "radius": 2 * mm});
            skCircle(sketch, "E1.17.25.0", {"center": v(85, 125) * mm, "radius": 2 * mm});
            skCircle(sketch, "E1.17.26.0", {"center": v(85, 130) * mm, "radius": 2 * mm});
            skCircle(sketch, "E1.17.27.0", {"center": v(85, 135) * mm, "radius": 2 * mm});
            skCircle(sketch, "E1.17.28.0", {"center": v(85, 140) * mm, "radius": 2 * mm});
            skCircle(sketch, "E1.17.29.0", {"center": v(85, 145) * mm, "radius": 2 * mm});
            skCircle(sketch, "E1.18.0.0", {"center": v(90, 0) * mm, "radius": 2 * mm});
            skCircle(sketch, "E1.18.1.0", {"center": v(90, 5) * mm, "radius": 2 * mm});
            skCircle(sketch, "E1.18.2.0", {"center": v(90, 10) * mm, "radius": 2 * mm});
            skCircle(sketch, "E1.18.3.0", {"center": v(90, 15) * mm, "radius": 2 * mm});
            skCircle(sketch, "E1.18.4.0", {"center": v(90, 20) * mm, "radius": 2 * mm});
            skCircle(sketch, "E1.18.5.0", {"center": v(90, 25) * mm, "radius": 2 * mm});
            skCircle(sketch, "E1.18.6.0", {"center": v(90, 30) * mm, "radius": 2 * mm});
            skCircle(sketch, "E1.18.7.0", {"center": v(90, 35) * mm, "radius": 2 * mm});
            skCircle(sketch, "E1.18.8.0", {"center": v(90, 40) * mm, "radius": 2 * mm});
            skCircle(sketch, "E1.18.9.0", {"center": v(90, 45) * mm, "radius": 2 * mm});
            skCircle(sketch, "E1.18.10.0", {"center": v(90, 50) * mm, "radius": 2 * mm});
            skCircle(sketch, "E1.18.11.0", {"center": v(90, 55) * mm, "radius": 2 * mm});
            skCircle(sketch, "E1.18.12.0", {"center": v(90, 60) * mm, "radius": 2 * mm});
            skCircle(sketch, "E1.18.13.0", {"center": v(90, 65) * mm, "radius": 2 * mm});
            skCircle(sketch, "E1.18.14.0", {"center": v(90, 70) * mm, "radius": 2 * mm});
            skCircle(sketch, "E1.18.15.0", {"center": v(90, 75) * mm, "radius": 2 * mm});
            skCircle(sketch, "E1.18.16.0", {"center": v(90, 80) * mm, "radius": 2 * mm});
            skCircle(sketch, "E1.18.17.0", {"center": v(90, 85) * mm, "radius": 2 * mm});
            skCircle(sketch, "E1.18.18.0", {"center": v(90, 90) * mm, "radius": 2 * mm});
            skCircle(sketch, "E1.18.19.0", {"center": v(90, 95) * mm, "radius": 2 * mm});
            skCircle(sketch, "E1.18.20.0", {"center": v(90, 100) * mm, "radius": 2 * mm});
            skCircle(sketch, "E1.18.21.0", {"center": v(90, 105) * mm, "radius": 2 * mm});
            skCircle(sketch, "E1.18.22.0", {"center": v(90, 110) * mm, "radius": 2 * mm});
            skCircle(sketch, "E1.18.23.0", {"center": v(90, 115) * mm, "radius": 2 * mm});
            skCircle(sketch, "E1.18.24.0", {"center": v(90, 120) * mm, "radius": 2 * mm});
            skCircle(sketch, "E1.18.25.0", {"center": v(90, 125) * mm, "radius": 2 * mm});
            skCircle(sketch, "E1.18.26.0", {"center": v(90, 130) * mm, "radius": 2 * mm});
            skCircle(sketch, "E1.18.27.0", {"center": v(90, 135) * mm, "radius": 2 * mm});
            skCircle(sketch, "E1.18.28.0", {"center": v(90, 140) * mm, "radius": 2 * mm});
            skCircle(sketch, "E1.18.29.0", {"center": v(90, 145) * mm, "radius": 2 * mm});
            skCircle(sketch, "E1.19.0.0", {"center": v(95, 0) * mm, "radius": 2 * mm});
            skCircle(sketch, "E1.19.1.0", {"center": v(95, 5) * mm, "radius": 2 * mm});
            skCircle(sketch, "E1.19.2.0", {"center": v(95, 10) * mm, "radius": 2 * mm});
            skCircle(sketch, "E1.19.3.0", {"center": v(95, 15) * mm, "radius": 2 * mm});
            skCircle(sketch, "E1.19.4.0", {"center": v(95, 20) * mm, "radius": 2 * mm});
            skCircle(sketch, "E1.19.5.0", {"center": v(95, 25) * mm, "radius": 2 * mm});
            skCircle(sketch, "E1.19.6.0", {"center": v(95, 30) * mm, "radius": 2 * mm});
            skCircle(sketch, "E1.19.7.0", {"center": v(95, 35) * mm, "radius": 2 * mm});
            skCircle(sketch, "E1.19.8.0", {"center": v(95, 40) * mm, "radius": 2 * mm});
            skCircle(sketch, "E1.19.9.0", {"center": v(95, 45) * mm, "radius": 2 * mm});
            skCircle(sketch, "E1.19.10.0", {"center": v(95, 50) * mm, "radius": 2 * mm});
            skCircle(sketch, "E1.19.11.0", {"center": v(95, 55) * mm, "radius": 2 * mm});
            skCircle(sketch, "E1.19.12.0", {"center": v(95, 60) * mm, "radius": 2 * mm});
            skCircle(sketch, "E1.19.13.0", {"center": v(95, 65) * mm, "radius": 2 * mm});
            skCircle(sketch, "E1.19.14.0", {"center": v(95, 70) * mm, "radius": 2 * mm});
            skCircle(sketch, "E1.19.15.0", {"center": v(95, 75) * mm, "radius": 2 * mm});
            skCircle(sketch, "E1.19.16.0", {"center": v(95, 80) * mm, "radius": 2 * mm});
            skCircle(sketch, "E1.19.17.0", {"center": v(95, 85) * mm, "radius": 2 * mm});
            skCircle(sketch, "E1.19.18.0", {"center": v(95, 90) * mm, "radius": 2 * mm});
            skCircle(sketch, "E1.19.19.0", {"center": v(95, 95) * mm, "radius": 2 * mm});
            skCircle(sketch, "E1.19.20.0", {"center": v(95, 100) * mm, "radius": 2 * mm});
            skCircle(sketch, "E1.19.21.0", {"center": v(95, 105) * mm, "radius": 2 * mm});
            skCircle(sketch, "E1.19.22.0", {"center": v(95, 110) * mm, "radius": 2 * mm});
            skCircle(sketch, "E1.19.23.0", {"center": v(95, 115) * mm, "radius": 2 * mm});
            skCircle(sketch, "E1.19.24.0", {"center": v(95, 120) * mm, "radius": 2 * mm});
            skCircle(sketch, "E1.19.25.0", {"center": v(95, 125) * mm, "radius": 2 * mm});
            skCircle(sketch, "E1.19.26.0", {"center": v(95, 130) * mm, "radius": 2 * mm});
            skCircle(sketch, "E1.19.27.0", {"center": v(95, 135) * mm, "radius": 2 * mm});
            skCircle(sketch, "E1.19.28.0", {"center": v(95, 140) * mm, "radius": 2 * mm});
            skCircle(sketch, "E1.19.29.0", {"center": v(95, 145) * mm, "radius": 2 * mm});
            skCircle(sketch, "E1.20.0.0", {"center": v(100, 0) * mm, "radius": 2 * mm});
            skCircle(sketch, "E1.20.1.0", {"center": v(100, 5) * mm, "radius": 2 * mm});
            skCircle(sketch, "E1.20.2.0", {"center": v(100, 10) * mm, "radius": 2 * mm});
            skCircle(sketch, "E1.20.3.0", {"center": v(100, 15) * mm, "radius": 2 * mm});
            skCircle(sketch, "E1.20.4.0", {"center": v(100, 20) * mm, "radius": 2 * mm});
            skCircle(sketch, "E1.20.5.0", {"center": v(100, 25) * mm, "radius": 2 * mm});
            skCircle(sketch, "E1.20.6.0", {"center": v(100, 30) * mm, "radius": 2 * mm});
            skCircle(sketch, "E1.20.7.0", {"center": v(100, 35) * mm, "radius": 2 * mm});
            skCircle(sketch, "E1.20.8.0", {"center": v(100, 40) * mm, "radius": 2 * mm});
            skCircle(sketch, "E1.20.9.0", {"center": v(100, 45) * mm, "radius": 2 * mm});
            skCircle(sketch, "E1.20.10.0", {"center": v(100, 50) * mm, "radius": 2 * mm});
            skCircle(sketch, "E1.20.11.0", {"center": v(100, 55) * mm, "radius": 2 * mm});
            skCircle(sketch, "E1.20.12.0", {"center": v(100, 60) * mm, "radius": 2 * mm});
            skCircle(sketch, "E1.20.13.0", {"center": v(100, 65) * mm, "radius": 2 * mm});
            skCircle(sketch, "E1.20.14.0", {"center": v(100, 70) * mm, "radius": 2 * mm});
            skCircle(sketch, "E1.20.15.0", {"center": v(100, 75) * mm, "radius": 2 * mm});
            skCircle(sketch, "E1.20.16.0", {"center": v(100, 80) * mm, "radius": 2 * mm});
            skCircle(sketch, "E1.20.17.0", {"center": v(100, 85) * mm, "radius": 2 * mm});
            skCircle(sketch, "E1.20.18.0", {"center": v(100, 90) * mm, "radius": 2 * mm});
            skCircle(sketch, "E1.20.19.0", {"center": v(100, 95) * mm, "radius": 2 * mm});
            skCircle(sketch, "E1.20.20.0", {"center": v(100, 100) * mm, "radius": 2 * mm});
            skCircle(sketch, "E1.20.21.0", {"center": v(100, 105) * mm, "radius": 2 * mm});
            skCircle(sketch, "E1.20.22.0", {"center": v(100, 110) * mm, "radius": 2 * mm});
            skCircle(sketch, "E1.20.23.0", {"center": v(100, 115) * mm, "radius": 2 * mm});
            skCircle(sketch, "E1.20.24.0", {"center": v(100, 120) * mm, "radius": 2 * mm});
            skCircle(sketch, "E1.20.25.0", {"center": v(100, 125) * mm, "radius": 2 * mm});
            skCircle(sketch, "E1.20.26.0", {"center": v(100, 130) * mm, "radius": 2 * mm});
            skCircle(sketch, "E1.20.27.0", {"center": v(100, 135) * mm, "radius": 2 * mm});
            skCircle(sketch, "E1.20.28.0", {"center": v(100, 140) * mm, "radius": 2 * mm});
            skCircle(sketch, "E1.20.29.0", {"center": v(100, 145) * mm, "radius": 2 * mm});
            skCircle(sketch, "E1.21.0.0", {"center": v(105, 0) * mm, "radius": 2 * mm});
            skCircle(sketch, "E1.21.1.0", {"center": v(105, 5) * mm, "radius": 2 * mm});
            skCircle(sketch, "E1.21.2.0", {"center": v(105, 10) * mm, "radius": 2 * mm});
            skCircle(sketch, "E1.21.3.0", {"center": v(105, 15) * mm, "radius": 2 * mm});
            skCircle(sketch, "E1.21.4.0", {"center": v(105, 20) * mm, "radius": 2 * mm});
            skCircle(sketch, "E1.21.5.0", {"center": v(105, 25) * mm, "radius": 2 * mm});
            skCircle(sketch, "E1.21.6.0", {"center": v(105, 30) * mm, "radius": 2 * mm});
            skCircle(sketch, "E1.21.7.0", {"center": v(105, 35) * mm, "radius": 2 * mm});
            skCircle(sketch, "E1.21.8.0", {"center": v(105, 40) * mm, "radius": 2 * mm});
            skCircle(sketch, "E1.21.9.0", {"center": v(105, 45) * mm, "radius": 2 * mm});
            skCircle(sketch, "E1.21.10.0", {"center": v(105, 50) * mm, "radius": 2 * mm});
            skCircle(sketch, "E1.21.11.0", {"center": v(105, 55) * mm, "radius": 2 * mm});
            skCircle(sketch, "E1.21.12.0", {"center": v(105, 60) * mm, "radius": 2 * mm});
            skCircle(sketch, "E1.21.13.0", {"center": v(105, 65) * mm, "radius": 2 * mm});
            skCircle(sketch, "E1.21.14.0", {"center": v(105, 70) * mm, "radius": 2 * mm});
            skCircle(sketch, "E1.21.15.0", {"center": v(105, 75) * mm, "radius": 2 * mm});
            skCircle(sketch, "E1.21.16.0", {"center": v(105, 80) * mm, "radius": 2 * mm});
            skCircle(sketch, "E1.21.17.0", {"center": v(105, 85) * mm, "radius": 2 * mm});
            skCircle(sketch, "E1.21.18.0", {"center": v(105, 90) * mm, "radius": 2 * mm});
            skCircle(sketch, "E1.21.19.0", {"center": v(105, 95) * mm, "radius": 2 * mm});
            skCircle(sketch, "E1.21.20.0", {"center": v(105, 100) * mm, "radius": 2 * mm});
            skCircle(sketch, "E1.21.21.0", {"center": v(105, 105) * mm, "radius": 2 * mm});
            skCircle(sketch, "E1.21.22.0", {"center": v(105, 110) * mm, "radius": 2 * mm});
            skCircle(sketch, "E1.21.23.0", {"center": v(105, 115) * mm, "radius": 2 * mm});
            skCircle(sketch, "E1.21.24.0", {"center": v(105, 120) * mm, "radius": 2 * mm});
            skCircle(sketch, "E1.21.25.0", {"center": v(105, 125) * mm, "radius": 2 * mm});
            skCircle(sketch, "E1.21.26.0", {"center": v(105, 130) * mm, "radius": 2 * mm});
            skCircle(sketch, "E1.21.27.0", {"center": v(105, 135) * mm, "radius": 2 * mm});
            skCircle(sketch, "E1.21.28.0", {"center": v(105, 140) * mm, "radius": 2 * mm});
            skCircle(sketch, "E1.21.29.0", {"center": v(105, 145) * mm, "radius": 2 * mm});
            skCircle(sketch, "E1.22.0.0", {"center": v(110, 0) * mm, "radius": 2 * mm});
            skCircle(sketch, "E1.22.1.0", {"center": v(110, 5) * mm, "radius": 2 * mm});
            skCircle(sketch, "E1.22.2.0", {"center": v(110, 10) * mm, "radius": 2 * mm});
            skCircle(sketch, "E1.22.3.0", {"center": v(110, 15) * mm, "radius": 2 * mm});
            skCircle(sketch, "E1.22.4.0", {"center": v(110, 20) * mm, "radius": 2 * mm});
            skCircle(sketch, "E1.22.5.0", {"center": v(110, 25) * mm, "radius": 2 * mm});
            skCircle(sketch, "E1.22.6.0", {"center": v(110, 30) * mm, "radius": 2 * mm});
            skCircle(sketch, "E1.22.7.0", {"center": v(110, 35) * mm, "radius": 2 * mm});
            skCircle(sketch, "E1.22.8.0", {"center": v(110, 40) * mm, "radius": 2 * mm});
            skCircle(sketch, "E1.22.9.0", {"center": v(110, 45) * mm, "radius": 2 * mm});
            skCircle(sketch, "E1.22.10.0", {"center": v(110, 50) * mm, "radius": 2 * mm});
            skCircle(sketch, "E1.22.11.0", {"center": v(110, 55) * mm, "radius": 2 * mm});
            skCircle(sketch, "E1.22.12.0", {"center": v(110, 60) * mm, "radius": 2 * mm});
            skCircle(sketch, "E1.22.13.0", {"center": v(110, 65) * mm, "radius": 2 * mm});
            skCircle(sketch, "E1.22.14.0", {"center": v(110, 70) * mm, "radius": 2 * mm});
            skCircle(sketch, "E1.22.15.0", {"center": v(110, 75) * mm, "radius": 2 * mm});
            skCircle(sketch, "E1.22.16.0", {"center": v(110, 80) * mm, "radius": 2 * mm});
            skCircle(sketch, "E1.22.17.0", {"center": v(110, 85) * mm, "radius": 2 * mm});
            skCircle(sketch, "E1.22.18.0", {"center": v(110, 90) * mm, "radius": 2 * mm});
            skCircle(sketch, "E1.22.19.0", {"center": v(110, 95) * mm, "radius": 2 * mm});
            skCircle(sketch, "E1.22.20.0", {"center": v(110, 100) * mm, "radius": 2 * mm});
            skCircle(sketch, "E1.22.21.0", {"center": v(110, 105) * mm, "radius": 2 * mm});
            skCircle(sketch, "E1.22.22.0", {"center": v(110, 110) * mm, "radius": 2 * mm});
            skCircle(sketch, "E1.22.23.0", {"center": v(110, 115) * mm, "radius": 2 * mm});
            skCircle(sketch, "E1.22.24.0", {"center": v(110, 120) * mm, "radius": 2 * mm});
            skCircle(sketch, "E1.22.25.0", {"center": v(110, 125) * mm, "radius": 2 * mm});
            skCircle(sketch, "E1.22.26.0", {"center": v(110, 130) * mm, "radius": 2 * mm});
            skCircle(sketch, "E1.22.27.0", {"center": v(110, 135) * mm, "radius": 2 * mm});
            skCircle(sketch, "E1.22.28.0", {"center": v(110, 140) * mm, "radius": 2 * mm});
            skCircle(sketch, "E1.22.29.0", {"center": v(110, 145) * mm, "radius": 2 * mm});
            skCircle(sketch, "E1.23.0.0", {"center": v(115, 0) * mm, "radius": 2 * mm});
            skCircle(sketch, "E1.23.1.0", {"center": v(115, 5) * mm, "radius": 2 * mm});
            skCircle(sketch, "E1.23.2.0", {"center": v(115, 10) * mm, "radius": 2 * mm});
            skCircle(sketch, "E1.23.3.0", {"center": v(115, 15) * mm, "radius": 2 * mm});
            skCircle(sketch, "E1.23.4.0", {"center": v(115, 20) * mm, "radius": 2 * mm});
            skCircle(sketch, "E1.23.5.0", {"center": v(115, 25) * mm, "radius": 2 * mm});
            skCircle(sketch, "E1.23.6.0", {"center": v(115, 30) * mm, "radius": 2 * mm});
            skCircle(sketch, "E1.23.7.0", {"center": v(115, 35) * mm, "radius": 2 * mm});
            skCircle(sketch, "E1.23.8.0", {"center": v(115, 40) * mm, "radius": 2 * mm});
            skCircle(sketch, "E1.23.9.0", {"center": v(115, 45) * mm, "radius": 2 * mm});
            skCircle(sketch, "E1.23.10.0", {"center": v(115, 50) * mm, "radius": 2 * mm});
            skCircle(sketch, "E1.23.11.0", {"center": v(115, 55) * mm, "radius": 2 * mm});
            skCircle(sketch, "E1.23.12.0", {"center": v(115, 60) * mm, "radius": 2 * mm});
            skCircle(sketch, "E1.23.13.0", {"center": v(115, 65) * mm, "radius": 2 * mm});
            skCircle(sketch, "E1.23.14.0", {"center": v(115, 70) * mm, "radius": 2 * mm});
            skCircle(sketch, "E1.23.15.0", {"center": v(115, 75) * mm, "radius": 2 * mm});
            skCircle(sketch, "E1.23.16.0", {"center": v(115, 80) * mm, "radius": 2 * mm});
            skCircle(sketch, "E1.23.17.0", {"center": v(115, 85) * mm, "radius": 2 * mm});
            skCircle(sketch, "E1.23.18.0", {"center": v(115, 90) * mm, "radius": 2 * mm});
            skCircle(sketch, "E1.23.19.0", {"center": v(115, 95) * mm, "radius": 2 * mm});
            skCircle(sketch, "E1.23.20.0", {"center": v(115, 100) * mm, "radius": 2 * mm});
            skCircle(sketch, "E1.23.21.0", {"center": v(115, 105) * mm, "radius": 2 * mm});
            skCircle(sketch, "E1.23.22.0", {"center": v(115, 110) * mm, "radius": 2 * mm});
            skCircle(sketch, "E1.23.23.0", {"center": v(115, 115) * mm, "radius": 2 * mm});
            skCircle(sketch, "E1.23.24.0", {"center": v(115, 120) * mm, "radius": 2 * mm});
            skCircle(sketch, "E1.23.25.0", {"center": v(115, 125) * mm, "radius": 2 * mm});
            skCircle(sketch, "E1.23.26.0", {"center": v(115, 130) * mm, "radius": 2 * mm});
            skCircle(sketch, "E1.23.27.0", {"center": v(115, 135) * mm, "radius": 2 * mm});
            skCircle(sketch, "E1.23.28.0", {"center": v(115, 140) * mm, "radius": 2 * mm});
            skCircle(sketch, "E1.23.29.0", {"center": v(115, 145) * mm, "radius": 2 * mm});
            skCircle(sketch, "E1.24.0.0", {"center": v(120, 0) * mm, "radius": 2 * mm});
            skCircle(sketch, "E1.24.1.0", {"center": v(120, 5) * mm, "radius": 2 * mm});
            skCircle(sketch, "E1.24.2.0", {"center": v(120, 10) * mm, "radius": 2 * mm});
            skCircle(sketch, "E1.24.3.0", {"center": v(120, 15) * mm, "radius": 2 * mm});
            skCircle(sketch, "E1.24.4.0", {"center": v(120, 20) * mm, "radius": 2 * mm});
            skCircle(sketch, "E1.24.5.0", {"center": v(120, 25) * mm, "radius": 2 * mm});
            skCircle(sketch, "E1.24.6.0", {"center": v(120, 30) * mm, "radius": 2 * mm});
            skCircle(sketch, "E1.24.7.0", {"center": v(120, 35) * mm, "radius": 2 * mm});
            skCircle(sketch, "E1.24.8.0", {"center": v(120, 40) * mm, "radius": 2 * mm});
            skCircle(sketch, "E1.24.9.0", {"center": v(120, 45) * mm, "radius": 2 * mm});
            skCircle(sketch, "E1.24.10.0", {"center": v(120, 50) * mm, "radius": 2 * mm});
            skCircle(sketch, "E1.24.11.0", {"center": v(120, 55) * mm, "radius": 2 * mm});
            skCircle(sketch, "E1.24.12.0", {"center": v(120, 60) * mm, "radius": 2 * mm});
            skCircle(sketch, "E1.24.13.0", {"center": v(120, 65) * mm, "radius": 2 * mm});
            skCircle(sketch, "E1.24.14.0", {"center": v(120, 70) * mm, "radius": 2 * mm});
            skCircle(sketch, "E1.24.15.0", {"center": v(120, 75) * mm, "radius": 2 * mm});
            skCircle(sketch, "E1.24.16.0", {"center": v(120, 80) * mm, "radius": 2 * mm});
            skCircle(sketch, "E1.24.17.0", {"center": v(120, 85) * mm, "radius": 2 * mm});
            skCircle(sketch, "E1.24.18.0", {"center": v(120, 90) * mm, "radius": 2 * mm});
            skCircle(sketch, "E1.24.19.0", {"center": v(120, 95) * mm, "radius": 2 * mm});
            skCircle(sketch, "E1.24.20.0", {"center": v(120, 100) * mm, "radius": 2 * mm});
            skCircle(sketch, "E1.24.21.0", {"center": v(120, 105) * mm, "radius": 2 * mm});
            skCircle(sketch, "E1.24.22.0", {"center": v(120, 110) * mm, "radius": 2 * mm});
            skCircle(sketch, "E1.24.23.0", {"center": v(120, 115) * mm, "radius": 2 * mm});
            skCircle(sketch, "E1.24.24.0", {"center": v(120, 120) * mm, "radius": 2 * mm});
            skCircle(sketch, "E1.24.25.0", {"center": v(120, 125) * mm, "radius": 2 * mm});
            skCircle(sketch, "E1.24.26.0", {"center": v(120, 130) * mm, "radius": 2 * mm});
            skCircle(sketch, "E1.24.27.0", {"center": v(120, 135) * mm, "radius": 2 * mm});
            skCircle(sketch, "E1.24.28.0", {"center": v(120, 140) * mm, "radius": 2 * mm});
            skCircle(sketch, "E1.24.29.0", {"center": v(120, 145) * mm, "radius": 2 * mm});
            skCircle(sketch, "E1.25.0.0", {"center": v(125, 0) * mm, "radius": 2 * mm});
            skCircle(sketch, "E1.25.1.0", {"center": v(125, 5) * mm, "radius": 2 * mm});
            skCircle(sketch, "E1.25.2.0", {"center": v(125, 10) * mm, "radius": 2 * mm});
            skCircle(sketch, "E1.25.3.0", {"center": v(125, 15) * mm, "radius": 2 * mm});
            skCircle(sketch, "E1.25.4.0", {"center": v(125, 20) * mm, "radius": 2 * mm});
            skCircle(sketch, "E1.25.5.0", {"center": v(125, 25) * mm, "radius": 2 * mm});
            skCircle(sketch, "E1.25.6.0", {"center": v(125, 30) * mm, "radius": 2 * mm});
            skCircle(sketch, "E1.25.7.0", {"center": v(125, 35) * mm, "radius": 2 * mm});
            skCircle(sketch, "E1.25.8.0", {"center": v(125, 40) * mm, "radius": 2 * mm});
            skCircle(sketch, "E1.25.9.0", {"center": v(125, 45) * mm, "radius": 2 * mm});
            skCircle(sketch, "E1.25.10.0", {"center": v(125, 50) * mm, "radius": 2 * mm});
            skCircle(sketch, "E1.25.11.0", {"center": v(125, 55) * mm, "radius": 2 * mm});
            skCircle(sketch, "E1.25.12.0", {"center": v(125, 60) * mm, "radius": 2 * mm});
            skCircle(sketch, "E1.25.13.0", {"center": v(125, 65) * mm, "radius": 2 * mm});
            skCircle(sketch, "E1.25.14.0", {"center": v(125, 70) * mm, "radius": 2 * mm});
            skCircle(sketch, "E1.25.15.0", {"center": v(125, 75) * mm, "radius": 2 * mm});
            skCircle(sketch, "E1.25.16.0", {"center": v(125, 80) * mm, "radius": 2 * mm});
            skCircle(sketch, "E1.25.17.0", {"center": v(125, 85) * mm, "radius": 2 * mm});
            skCircle(sketch, "E1.25.18.0", {"center": v(125, 90) * mm, "radius": 2 * mm});
            skCircle(sketch, "E1.25.19.0", {"center": v(125, 95) * mm, "radius": 2 * mm});
            skCircle(sketch, "E1.25.20.0", {"center": v(125, 100) * mm, "radius": 2 * mm});
            skCircle(sketch, "E1.25.21.0", {"center": v(125, 105) * mm, "radius": 2 * mm});
            skCircle(sketch, "E1.25.22.0", {"center": v(125, 110) * mm, "radius": 2 * mm});
            skCircle(sketch, "E1.25.23.0", {"center": v(125, 115) * mm, "radius": 2 * mm});
            skCircle(sketch, "E1.25.24.0", {"center": v(125, 120) * mm, "radius": 2 * mm});
            skCircle(sketch, "E1.25.25.0", {"center": v(125, 125) * mm, "radius": 2 * mm});
            skCircle(sketch, "E1.25.26.0", {"center": v(125, 130) * mm, "radius": 2 * mm});
            skCircle(sketch, "E1.25.27.0", {"center": v(125, 135) * mm, "radius": 2 * mm});
            skCircle(sketch, "E1.25.28.0", {"center": v(125, 140) * mm, "radius": 2 * mm});
            skCircle(sketch, "E1.25.29.0", {"center": v(125, 145) * mm, "radius": 2 * mm});
            skCircle(sketch, "E1.26.0.0", {"center": v(130, 0) * mm, "radius": 2 * mm});
            skCircle(sketch, "E1.26.1.0", {"center": v(130, 5) * mm, "radius": 2 * mm});
            skCircle(sketch, "E1.26.2.0", {"center": v(130, 10) * mm, "radius": 2 * mm});
            skCircle(sketch, "E1.26.3.0", {"center": v(130, 15) * mm, "radius": 2 * mm});
            skCircle(sketch, "E1.26.4.0", {"center": v(130, 20) * mm, "radius": 2 * mm});
            skCircle(sketch, "E1.26.5.0", {"center": v(130, 25) * mm, "radius": 2 * mm});
            skCircle(sketch, "E1.26.6.0", {"center": v(130, 30) * mm, "radius": 2 * mm});
            skCircle(sketch, "E1.26.7.0", {"center": v(130, 35) * mm, "radius": 2 * mm});
            skCircle(sketch, "E1.26.8.0", {"center": v(130, 40) * mm, "radius": 2 * mm});
            skCircle(sketch, "E1.26.9.0", {"center": v(130, 45) * mm, "radius": 2 * mm});
            skCircle(sketch, "E1.26.10.0", {"center": v(130, 50) * mm, "radius": 2 * mm});
            skCircle(sketch, "E1.26.11.0", {"center": v(130, 55) * mm, "radius": 2 * mm});
            skCircle(sketch, "E1.26.12.0", {"center": v(130, 60) * mm, "radius": 2 * mm});
            skCircle(sketch, "E1.26.13.0", {"center": v(130, 65) * mm, "radius": 2 * mm});
            skCircle(sketch, "E1.26.14.0", {"center": v(130, 70) * mm, "radius": 2 * mm});
            skCircle(sketch, "E1.26.15.0", {"center": v(130, 75) * mm, "radius": 2 * mm});
            skCircle(sketch, "E1.26.16.0", {"center": v(130, 80) * mm, "radius": 2 * mm});
            skCircle(sketch, "E1.26.17.0", {"center": v(130, 85) * mm, "radius": 2 * mm});
            skCircle(sketch, "E1.26.18.0", {"center": v(130, 90) * mm, "radius": 2 * mm});
            skCircle(sketch, "E1.26.19.0", {"center": v(130, 95) * mm, "radius": 2 * mm});
            skCircle(sketch, "E1.26.20.0", {"center": v(130, 100) * mm, "radius": 2 * mm});
            skCircle(sketch, "E1.26.21.0", {"center": v(130, 105) * mm, "radius": 2 * mm});
            skCircle(sketch, "E1.26.22.0", {"center": v(130, 110) * mm, "radius": 2 * mm});
            skCircle(sketch, "E1.26.23.0", {"center": v(130, 115) * mm, "radius": 2 * mm});
            skCircle(sketch, "E1.26.24.0", {"center": v(130, 120) * mm, "radius": 2 * mm});
            skCircle(sketch, "E1.26.25.0", {"center": v(130, 125) * mm, "radius": 2 * mm});
            skCircle(sketch, "E1.26.26.0", {"center": v(130, 130) * mm, "radius": 2 * mm});
            skCircle(sketch, "E1.26.27.0", {"center": v(130, 135) * mm, "radius": 2 * mm});
            skCircle(sketch, "E1.26.28.0", {"center": v(130, 140) * mm, "radius": 2 * mm});
            skCircle(sketch, "E1.26.29.0", {"center": v(130, 145) * mm, "radius": 2 * mm});
            skCircle(sketch, "E1.27.0.0", {"center": v(135, 0) * mm, "radius": 2 * mm});
            skCircle(sketch, "E1.27.1.0", {"center": v(135, 5) * mm, "radius": 2 * mm});
            skCircle(sketch, "E1.27.2.0", {"center": v(135, 10) * mm, "radius": 2 * mm});
            skCircle(sketch, "E1.27.3.0", {"center": v(135, 15) * mm, "radius": 2 * mm});
            skCircle(sketch, "E1.27.4.0", {"center": v(135, 20) * mm, "radius": 2 * mm});
            skCircle(sketch, "E1.27.5.0", {"center": v(135, 25) * mm, "radius": 2 * mm});
            skCircle(sketch, "E1.27.6.0", {"center": v(135, 30) * mm, "radius": 2 * mm});
            skCircle(sketch, "E1.27.7.0", {"center": v(135, 35) * mm, "radius": 2 * mm});
            skCircle(sketch, "E1.27.8.0", {"center": v(135, 40) * mm, "radius": 2 * mm});
            skCircle(sketch, "E1.27.9.0", {"center": v(135, 45) * mm, "radius": 2 * mm});
            skCircle(sketch, "E1.27.10.0", {"center": v(135, 50) * mm, "radius": 2 * mm});
            skCircle(sketch, "E1.27.11.0", {"center": v(135, 55) * mm, "radius": 2 * mm});
            skCircle(sketch, "E1.27.12.0", {"center": v(135, 60) * mm, "radius": 2 * mm});
            skCircle(sketch, "E1.27.13.0", {"center": v(135, 65) * mm, "radius": 2 * mm});
            skCircle(sketch, "E1.27.14.0", {"center": v(135, 70) * mm, "radius": 2 * mm});
            skCircle(sketch, "E1.27.15.0", {"center": v(135, 75) * mm, "radius": 2 * mm});
            skCircle(sketch, "E1.27.16.0", {"center": v(135, 80) * mm, "radius": 2 * mm});
            skCircle(sketch, "E1.27.17.0", {"center": v(135, 85) * mm, "radius": 2 * mm});
            skCircle(sketch, "E1.27.18.0", {"center": v(135, 90) * mm, "radius": 2 * mm});
            skCircle(sketch, "E1.27.19.0", {"center": v(135, 95) * mm, "radius": 2 * mm});
            skCircle(sketch, "E1.27.20.0", {"center": v(135, 100) * mm, "radius": 2 * mm});
            skCircle(sketch, "E1.27.21.0", {"center": v(135, 105) * mm, "radius": 2 * mm});
            skCircle(sketch, "E1.27.22.0", {"center": v(135, 110) * mm, "radius": 2 * mm});
            skCircle(sketch, "E1.27.23.0", {"center": v(135, 115) * mm, "radius": 2 * mm});
            skCircle(sketch, "E1.27.24.0", {"center": v(135, 120) * mm, "radius": 2 * mm});
            skCircle(sketch, "E1.27.25.0", {"center": v(135, 125) * mm, "radius": 2 * mm});
            skCircle(sketch, "E1.27.26.0", {"center": v(135, 130) * mm, "radius": 2 * mm});
            skCircle(sketch, "E1.27.27.0", {"center": v(135, 135) * mm, "radius": 2 * mm});
            skCircle(sketch, "E1.27.28.0", {"center": v(135, 140) * mm, "radius": 2 * mm});
            skCircle(sketch, "E1.27.29.0", {"center": v(135, 145) * mm, "radius": 2 * mm});
            skCircle(sketch, "E1.28.0.0", {"center": v(140, 0) * mm, "radius": 2 * mm});
            skCircle(sketch, "E1.28.1.0", {"center": v(140, 5) * mm, "radius": 2 * mm});
            skCircle(sketch, "E1.28.2.0", {"center": v(140, 10) * mm, "radius": 2 * mm});
            skCircle(sketch, "E1.28.3.0", {"center": v(140, 15) * mm, "radius": 2 * mm});
            skCircle(sketch, "E1.28.4.0", {"center": v(140, 20) * mm, "radius": 2 * mm});
            skCircle(sketch, "E1.28.5.0", {"center": v(140, 25) * mm, "radius": 2 * mm});
            skCircle(sketch, "E1.28.6.0", {"center": v(140, 30) * mm, "radius": 2 * mm});
            skCircle(sketch, "E1.28.7.0", {"center": v(140, 35) * mm, "radius": 2 * mm});
            skCircle(sketch, "E1.28.8.0", {"center": v(140, 40) * mm, "radius": 2 * mm});
            skCircle(sketch, "E1.28.9.0", {"center": v(140, 45) * mm, "radius": 2 * mm});
            skCircle(sketch, "E1.28.10.0", {"center": v(140, 50) * mm, "radius": 2 * mm});
            skCircle(sketch, "E1.28.11.0", {"center": v(140, 55) * mm, "radius": 2 * mm});
            skCircle(sketch, "E1.28.12.0", {"center": v(140, 60) * mm, "radius": 2 * mm});
            skCircle(sketch, "E1.28.13.0", {"center": v(140, 65) * mm, "radius": 2 * mm});
            skCircle(sketch, "E1.28.14.0", {"center": v(140, 70) * mm, "radius": 2 * mm});
            skCircle(sketch, "E1.28.15.0", {"center": v(140, 75) * mm, "radius": 2 * mm});
            skCircle(sketch, "E1.28.16.0", {"center": v(140, 80) * mm, "radius": 2 * mm});
            skCircle(sketch, "E1.28.17.0", {"center": v(140, 85) * mm, "radius": 2 * mm});
            skCircle(sketch, "E1.28.18.0", {"center": v(140, 90) * mm, "radius": 2 * mm});
            skCircle(sketch, "E1.28.19.0", {"center": v(140, 95) * mm, "radius": 2 * mm});
            skCircle(sketch, "E1.28.20.0", {"center": v(140, 100) * mm, "radius": 2 * mm});
            skCircle(sketch, "E1.28.21.0", {"center": v(140, 105) * mm, "radius": 2 * mm});
            skCircle(sketch, "E1.28.22.0", {"center": v(140, 110) * mm, "radius": 2 * mm});
            skCircle(sketch, "E1.28.23.0", {"center": v(140, 115) * mm, "radius": 2 * mm});
            skCircle(sketch, "E1.28.24.0", {"center": v(140, 120) * mm, "radius": 2 * mm});
            skCircle(sketch, "E1.28.25.0", {"center": v(140, 125) * mm, "radius": 2 * mm});
            skCircle(sketch, "E1.28.26.0", {"center": v(140, 130) * mm, "radius": 2 * mm});
            skCircle(sketch, "E1.28.27.0", {"center": v(140, 135) * mm, "radius": 2 * mm});
            skCircle(sketch, "E1.28.28.0", {"center": v(140, 140) * mm, "radius": 2 * mm});
            skCircle(sketch, "E1.28.29.0", {"center": v(140, 145) * mm, "radius": 2 * mm});
            skCircle(sketch, "E1.29.0.0", {"center": v(145, 0) * mm, "radius": 2 * mm});
            skCircle(sketch, "E1.29.1.0", {"center": v(145, 5) * mm, "radius": 2 * mm});
            skCircle(sketch, "E1.29.2.0", {"center": v(145, 10) * mm, "radius": 2 * mm});
            skCircle(sketch, "E1.29.3.0", {"center": v(145, 15) * mm, "radius": 2 * mm});
            skCircle(sketch, "E1.29.4.0", {"center": v(145, 20) * mm, "radius": 2 * mm});
            skCircle(sketch, "E1.29.5.0", {"center": v(145, 25) * mm, "radius": 2 * mm});
            skCircle(sketch, "E1.29.6.0", {"center": v(145, 30) * mm, "radius": 2 * mm});
            skCircle(sketch, "E1.29.7.0", {"center": v(145, 35) * mm, "radius": 2 * mm});
            skCircle(sketch, "E1.29.8.0", {"center": v(145, 40) * mm, "radius": 2 * mm});
            skCircle(sketch, "E1.29.9.0", {"center": v(145, 45) * mm, "radius": 2 * mm});
            skCircle(sketch, "E1.29.10.0", {"center": v(145, 50) * mm, "radius": 2 * mm});
            skCircle(sketch, "E1.29.11.0", {"center": v(145, 55) * mm, "radius": 2 * mm});
            skCircle(sketch, "E1.29.12.0", {"center": v(145, 60) * mm, "radius": 2 * mm});
            skCircle(sketch, "E1.29.13.0", {"center": v(145, 65) * mm, "radius": 2 * mm});
            skCircle(sketch, "E1.29.14.0", {"center": v(145, 70) * mm, "radius": 2 * mm});
            skCircle(sketch, "E1.29.15.0", {"center": v(145, 75) * mm, "radius": 2 * mm});
            skCircle(sketch, "E1.29.16.0", {"center": v(145, 80) * mm, "radius": 2 * mm});
            skCircle(sketch, "E1.29.17.0", {"center": v(145, 85) * mm, "radius": 2 * mm});
            skCircle(sketch, "E1.29.18.0", {"center": v(145, 90) * mm, "radius": 2 * mm});
            skCircle(sketch, "E1.29.19.0", {"center": v(145, 95) * mm, "radius": 2 * mm});
            skCircle(sketch, "E1.29.20.0", {"center": v(145, 100) * mm, "radius": 2 * mm});
            skCircle(sketch, "E1.29.21.0", {"center": v(145, 105) * mm, "radius": 2 * mm});
            skCircle(sketch, "E1.29.22.0", {"center": v(145, 110) * mm, "radius": 2 * mm});
            skCircle(sketch, "E1.29.23.0", {"center": v(145, 115) * mm, "radius": 2 * mm});
            skCircle(sketch, "E1.29.24.0", {"center": v(145, 120) * mm, "radius": 2 * mm});
            skCircle(sketch, "E1.29.25.0", {"center": v(145, 125) * mm, "radius": 2 * mm});
            skCircle(sketch, "E1.29.26.0", {"center": v(145, 130) * mm, "radius": 2 * mm});
            skCircle(sketch, "E1.29.27.0", {"center": v(145, 135) * mm, "radius": 2 * mm});
            skCircle(sketch, "E1.29.28.0", {"center": v(145, 140) * mm, "radius": 2 * mm});
            skCircle(sketch, "E1.29.29.0", {"center": v(145, 145) * mm, "radius": 2 * mm});
            skLineSegment(sketch, "E1.direction1", {"start": v(0, 0) * mm, "end": v(5, 0) * mm, "construction": true});
            skLineSegment(sketch, "E1.direction2", {"start": v(0, 0) * mm, "end": v(0, 5) * mm, "construction": true});
            skLineSegment(sketch, "E2.bottom", {"start": v(-4, 149) * mm, "end": v(149, 149) * mm});
            skLineSegment(sketch, "E2.top", {"start": v(-4, -4) * mm, "end": v(149, -4) * mm});
            skLineSegment(sketch, "E2.left", {"start": v(-4, 149) * mm, "end": v(-4, -4) * mm});
            skLineSegment(sketch, "E2.right", {"start": v(149, 149) * mm, "end": v(149, -4) * mm});
            skSolve(sketch);
        }
        {
            var Q0;
            Q0=makeQuery(id+"F0.imprint","IMPRINT",FACE,{"disambiguationData":[TD([[makeQuery(id+"F0.imprint","IMPRINT",EDGE,{"derivedFrom":sQuery(id+"F0.wireOp",EDGE,"E0")}),-1.0]])]});
            extrude(context, id + "F1", {"entities" : qUnion([Q0]), "depth" : 1.2 * mm, "offsetDistance" : 25 * mm});
        }
        {
            var Q0;
            Q0=makeQuery(id+"F1.opExtrude","CAP_FACE",FACE,{"disambiguationData":[OSD([sQuery(id+"F0.wireOp",EDGE,"E0"),sQuery(id+"F0.wireOp",EDGE,"E1.0.1.0"),sQuery(id+"F0.wireOp",EDGE,"E1.0.2.0"),sQuery(id+"F0.wireOp",EDGE,"E1.0.3.0"),sQuery(id+"F0.wireOp",EDGE,"E1.0.4.0"),sQuery(id+"F0.wireOp",EDGE,"E1.0.5.0"),sQuery(id+"F0.wireOp",EDGE,"E1.0.6.0"),sQuery(id+"F0.wireOp",EDGE,"E1.0.7.0"),sQuery(id+"F0.wireOp",EDGE,"E1.0.8.0"),sQuery(id+"F0.wireOp",EDGE,"E1.0.9.0"),sQuery(id+"F0.wireOp",EDGE,"E1.0.10.0"),sQuery(id+"F0.wireOp",EDGE,"E1.0.11.0"),sQuery(id+"F0.wireOp",EDGE,"E1.0.12.0"),sQuery(id+"F0.wireOp",EDGE,"E1.0.13.0"),sQuery(id+"F0.wireOp",EDGE,"E1.0.14.0"),sQuery(id+"F0.wireOp",EDGE,"E1.0.15.0"),sQuery(id+"F0.wireOp",EDGE,"E1.0.16.0"),sQuery(id+"F0.wireOp",EDGE,"E1.0.17.0"),sQuery(id+"F0.wireOp",EDGE,"E1.0.18.0"),sQuery(id+"F0.wireOp",EDGE,"E1.0.19.0"),sQuery(id+"F0.wireOp",EDGE,"E1.0.20.0"),sQuery(id+"F0.wireOp",EDGE,"E1.0.21.0"),sQuery(id+"F0.wireOp",EDGE,"E1.0.22.0"),sQuery(id+"F0.wireOp",EDGE,"E1.0.23.0"),sQuery(id+"F0.wireOp",EDGE,"E1.0.24.0"),sQuery(id+"F0.wireOp",EDGE,"E1.0.25.0"),sQuery(id+"F0.wireOp",EDGE,"E1.0.26.0"),sQuery(id+"F0.wireOp",EDGE,"E1.0.27.0"),sQuery(id+"F0.wireOp",EDGE,"E1.0.28.0"),sQuery(id+"F0.wireOp",EDGE,"E1.0.29.0"),sQuery(id+"F0.wireOp",EDGE,"E1.1.0.0"),sQuery(id+"F0.wireOp",EDGE,"E1.1.1.0"),sQuery(id+"F0.wireOp",EDGE,"E1.1.2.0"),sQuery(id+"F0.wireOp",EDGE,"E1.1.3.0"),sQuery(id+"F0.wireOp",EDGE,"E1.1.4.0"),sQuery(id+"F0.wireOp",EDGE,"E1.1.5.0"),sQuery(id+"F0.wireOp",EDGE,"E1.1.6.0"),sQuery(id+"F0.wireOp",EDGE,"E1.1.7.0"),sQuery(id+"F0.wireOp",EDGE,"E1.1.8.0"),sQuery(id+"F0.wireOp",EDGE,"E1.1.9.0"),sQuery(id+"F0.wireOp",EDGE,"E1.1.10.0"),sQuery(id+"F0.wireOp",EDGE,"E1.1.11.0"),sQuery(id+"F0.wireOp",EDGE,"E1.1.12.0"),sQuery(id+"F0.wireOp",EDGE,"E1.1.13.0"),sQuery(id+"F0.wireOp",EDGE,"E1.1.14.0"),sQuery(id+"F0.wireOp",EDGE,"E1.1.15.0"),sQuery(id+"F0.wireOp",EDGE,"E1.1.16.0"),sQuery(id+"F0.wireOp",EDGE,"E1.1.17.0"),sQuery(id+"F0.wireOp",EDGE,"E1.1.18.0"),sQuery(id+"F0.wireOp",EDGE,"E1.1.19.0"),sQuery(id+"F0.wireOp",EDGE,"E1.1.20.0"),sQuery(id+"F0.wireOp",EDGE,"E1.1.21.0"),sQuery(id+"F0.wireOp",EDGE,"E1.1.22.0"),sQuery(id+"F0.wireOp",EDGE,"E1.1.23.0"),sQuery(id+"F0.wireOp",EDGE,"E1.1.24.0"),sQuery(id+"F0.wireOp",EDGE,"E1.1.25.0"),sQuery(id+"F0.wireOp",EDGE,"E1.1.26.0"),sQuery(id+"F0.wireOp",EDGE,"E1.1.27.0"),sQuery(id+"F0.wireOp",EDGE,"E1.1.28.0"),sQuery(id+"F0.wireOp",EDGE,"E1.1.29.0"),sQuery(id+"F0.wireOp",EDGE,"E1.2.0.0"),sQuery(id+"F0.wireOp",EDGE,"E1.2.1.0"),sQuery(id+"F0.wireOp",EDGE,"E1.2.2.0"),sQuery(id+"F0.wireOp",EDGE,"E1.2.3.0"),sQuery(id+"F0.wireOp",EDGE,"E1.2.4.0"),sQuery(id+"F0.wireOp",EDGE,"E1.2.5.0"),sQuery(id+"F0.wireOp",EDGE,"E1.2.6.0"),sQuery(id+"F0.wireOp",EDGE,"E1.2.7.0"),sQuery(id+"F0.wireOp",EDGE,"E1.2.8.0"),sQuery(id+"F0.wireOp",EDGE,"E1.2.9.0"),sQuery(id+"F0.wireOp",EDGE,"E1.2.10.0"),sQuery(id+"F0.wireOp",EDGE,"E1.2.11.0"),sQuery(id+"F0.wireOp",EDGE,"E1.2.12.0"),sQuery(id+"F0.wireOp",EDGE,"E1.2.13.0"),sQuery(id+"F0.wireOp",EDGE,"E1.2.14.0"),sQuery(id+"F0.wireOp",EDGE,"E1.2.15.0"),sQuery(id+"F0.wireOp",EDGE,"E1.2.16.0"),sQuery(id+"F0.wireOp",EDGE,"E1.2.17.0"),sQuery(id+"F0.wireOp",EDGE,"E1.2.18.0"),sQuery(id+"F0.wireOp",EDGE,"E1.2.19.0"),sQuery(id+"F0.wireOp",EDGE,"E1.2.20.0"),sQuery(id+"F0.wireOp",EDGE,"E1.2.21.0"),sQuery(id+"F0.wireOp",EDGE,"E1.2.22.0"),sQuery(id+"F0.wireOp",EDGE,"E1.2.23.0"),sQuery(id+"F0.wireOp",EDGE,"E1.2.24.0"),sQuery(id+"F0.wireOp",EDGE,"E1.2.25.0"),sQuery(id+"F0.wireOp",EDGE,"E1.2.26.0"),sQuery(id+"F0.wireOp",EDGE,"E1.2.27.0"),sQuery(id+"F0.wireOp",EDGE,"E1.2.28.0"),sQuery(id+"F0.wireOp",EDGE,"E1.2.29.0"),sQuery(id+"F0.wireOp",EDGE,"E1.3.0.0"),sQuery(id+"F0.wireOp",EDGE,"E1.3.1.0"),sQuery(id+"F0.wireOp",EDGE,"E1.3.2.0"),sQuery(id+"F0.wireOp",EDGE,"E1.3.3.0"),sQuery(id+"F0.wireOp",EDGE,"E1.3.4.0"),sQuery(id+"F0.wireOp",EDGE,"E1.3.5.0"),sQuery(id+"F0.wireOp",EDGE,"E1.3.6.0"),sQuery(id+"F0.wireOp",EDGE,"E1.3.7.0"),sQuery(id+"F0.wireOp",EDGE,"E1.3.8.0"),sQuery(id+"F0.wireOp",EDGE,"E1.3.9.0"),sQuery(id+"F0.wireOp",EDGE,"E1.3.10.0"),sQuery(id+"F0.wireOp",EDGE,"E1.3.11.0"),sQuery(id+"F0.wireOp",EDGE,"E1.3.12.0"),sQuery(id+"F0.wireOp",EDGE,"E1.3.13.0"),sQuery(id+"F0.wireOp",EDGE,"E1.3.14.0"),sQuery(id+"F0.wireOp",EDGE,"E1.3.15.0"),sQuery(id+"F0.wireOp",EDGE,"E1.3.16.0"),sQuery(id+"F0.wireOp",EDGE,"E1.3.17.0"),sQuery(id+"F0.wireOp",EDGE,"E1.3.18.0"),sQuery(id+"F0.wireOp",EDGE,"E1.3.19.0"),sQuery(id+"F0.wireOp",EDGE,"E1.3.20.0"),sQuery(id+"F0.wireOp",EDGE,"E1.3.21.0"),sQuery(id+"F0.wireOp",EDGE,"E1.3.22.0"),sQuery(id+"F0.wireOp",EDGE,"E1.3.23.0"),sQuery(id+"F0.wireOp",EDGE,"E1.3.24.0"),sQuery(id+"F0.wireOp",EDGE,"E1.3.25.0"),sQuery(id+"F0.wireOp",EDGE,"E1.3.26.0"),sQuery(id+"F0.wireOp",EDGE,"E1.3.27.0"),sQuery(id+"F0.wireOp",EDGE,"E1.3.28.0"),sQuery(id+"F0.wireOp",EDGE,"E1.3.29.0"),sQuery(id+"F0.wireOp",EDGE,"E1.4.0.0"),sQuery(id+"F0.wireOp",EDGE,"E1.4.1.0"),sQuery(id+"F0.wireOp",EDGE,"E1.4.2.0"),sQuery(id+"F0.wireOp",EDGE,"E1.4.3.0"),sQuery(id+"F0.wireOp",EDGE,"E1.4.4.0"),sQuery(id+"F0.wireOp",EDGE,"E1.4.5.0"),sQuery(id+"F0.wireOp",EDGE,"E1.4.6.0"),sQuery(id+"F0.wireOp",EDGE,"E1.4.7.0"),sQuery(id+"F0.wireOp",EDGE,"E1.4.8.0"),sQuery(id+"F0.wireOp",EDGE,"E1.4.9.0"),sQuery(id+"F0.wireOp",EDGE,"E1.4.10.0"),sQuery(id+"F0.wireOp",EDGE,"E1.4.11.0"),sQuery(id+"F0.wireOp",EDGE,"E1.4.12.0"),sQuery(id+"F0.wireOp",EDGE,"E1.4.13.0"),sQuery(id+"F0.wireOp",EDGE,"E1.4.14.0"),sQuery(id+"F0.wireOp",EDGE,"E1.4.15.0"),sQuery(id+"F0.wireOp",EDGE,"E1.4.16.0"),sQuery(id+"F0.wireOp",EDGE,"E1.4.17.0"),sQuery(id+"F0.wireOp",EDGE,"E1.4.18.0"),sQuery(id+"F0.wireOp",EDGE,"E1.4.19.0"),sQuery(id+"F0.wireOp",EDGE,"E1.4.20.0"),sQuery(id+"F0.wireOp",EDGE,"E1.4.21.0"),sQuery(id+"F0.wireOp",EDGE,"E1.4.22.0"),sQuery(id+"F0.wireOp",EDGE,"E1.4.23.0"),sQuery(id+"F0.wireOp",EDGE,"E1.4.24.0"),sQuery(id+"F0.wireOp",EDGE,"E1.4.25.0"),sQuery(id+"F0.wireOp",EDGE,"E1.4.26.0"),sQuery(id+"F0.wireOp",EDGE,"E1.4.27.0"),sQuery(id+"F0.wireOp",EDGE,"E1.4.28.0"),sQuery(id+"F0.wireOp",EDGE,"E1.4.29.0"),sQuery(id+"F0.wireOp",EDGE,"E1.5.0.0"),sQuery(id+"F0.wireOp",EDGE,"E1.5.1.0"),sQuery(id+"F0.wireOp",EDGE,"E1.5.2.0"),sQuery(id+"F0.wireOp",EDGE,"E1.5.3.0"),sQuery(id+"F0.wireOp",EDGE,"E1.5.4.0"),sQuery(id+"F0.wireOp",EDGE,"E1.5.5.0"),sQuery(id+"F0.wireOp",EDGE,"E1.5.6.0"),sQuery(id+"F0.wireOp",EDGE,"E1.5.7.0"),sQuery(id+"F0.wireOp",EDGE,"E1.5.8.0"),sQuery(id+"F0.wireOp",EDGE,"E1.5.9.0"),sQuery(id+"F0.wireOp",EDGE,"E1.5.10.0"),sQuery(id+"F0.wireOp",EDGE,"E1.5.11.0"),sQuery(id+"F0.wireOp",EDGE,"E1.5.12.0"),sQuery(id+"F0.wireOp",EDGE,"E1.5.13.0"),sQuery(id+"F0.wireOp",EDGE,"E1.5.14.0"),sQuery(id+"F0.wireOp",EDGE,"E1.5.15.0"),sQuery(id+"F0.wireOp",EDGE,"E1.5.16.0"),sQuery(id+"F0.wireOp",EDGE,"E1.5.17.0"),sQuery(id+"F0.wireOp",EDGE,"E1.5.18.0"),sQuery(id+"F0.wireOp",EDGE,"E1.5.19.0"),sQuery(id+"F0.wireOp",EDGE,"E1.5.20.0"),sQuery(id+"F0.wireOp",EDGE,"E1.5.21.0"),sQuery(id+"F0.wireOp",EDGE,"E1.5.22.0"),sQuery(id+"F0.wireOp",EDGE,"E1.5.23.0"),sQuery(id+"F0.wireOp",EDGE,"E1.5.24.0"),sQuery(id+"F0.wireOp",EDGE,"E1.5.25.0"),sQuery(id+"F0.wireOp",EDGE,"E1.5.26.0"),sQuery(id+"F0.wireOp",EDGE,"E1.5.27.0"),sQuery(id+"F0.wireOp",EDGE,"E1.5.28.0"),sQuery(id+"F0.wireOp",EDGE,"E1.5.29.0"),sQuery(id+"F0.wireOp",EDGE,"E1.6.0.0"),sQuery(id+"F0.wireOp",EDGE,"E1.6.1.0"),sQuery(id+"F0.wireOp",EDGE,"E1.6.2.0"),sQuery(id+"F0.wireOp",EDGE,"E1.6.3.0"),sQuery(id+"F0.wireOp",EDGE,"E1.6.4.0"),sQuery(id+"F0.wireOp",EDGE,"E1.6.5.0"),sQuery(id+"F0.wireOp",EDGE,"E1.6.6.0"),sQuery(id+"F0.wireOp",EDGE,"E1.6.7.0"),sQuery(id+"F0.wireOp",EDGE,"E1.6.8.0"),sQuery(id+"F0.wireOp",EDGE,"E1.6.9.0"),sQuery(id+"F0.wireOp",EDGE,"E1.6.10.0"),sQuery(id+"F0.wireOp",EDGE,"E1.6.11.0"),sQuery(id+"F0.wireOp",EDGE,"E1.6.12.0"),sQuery(id+"F0.wireOp",EDGE,"E1.6.13.0"),sQuery(id+"F0.wireOp",EDGE,"E1.6.14.0"),sQuery(id+"F0.wireOp",EDGE,"E1.6.15.0"),sQuery(id+"F0.wireOp",EDGE,"E1.6.16.0"),sQuery(id+"F0.wireOp",EDGE,"E1.6.17.0"),sQuery(id+"F0.wireOp",EDGE,"E1.6.18.0"),sQuery(id+"F0.wireOp",EDGE,"E1.6.19.0"),sQuery(id+"F0.wireOp",EDGE,"E1.6.20.0"),sQuery(id+"F0.wireOp",EDGE,"E1.6.21.0"),sQuery(id+"F0.wireOp",EDGE,"E1.6.22.0"),sQuery(id+"F0.wireOp",EDGE,"E1.6.23.0"),sQuery(id+"F0.wireOp",EDGE,"E1.6.24.0"),sQuery(id+"F0.wireOp",EDGE,"E1.6.25.0"),sQuery(id+"F0.wireOp",EDGE,"E1.6.26.0"),sQuery(id+"F0.wireOp",EDGE,"E1.6.27.0"),sQuery(id+"F0.wireOp",EDGE,"E1.6.28.0"),sQuery(id+"F0.wireOp",EDGE,"E1.6.29.0"),sQuery(id+"F0.wireOp",EDGE,"E1.7.0.0"),sQuery(id+"F0.wireOp",EDGE,"E1.7.1.0"),sQuery(id+"F0.wireOp",EDGE,"E1.7.2.0"),sQuery(id+"F0.wireOp",EDGE,"E1.7.3.0"),sQuery(id+"F0.wireOp",EDGE,"E1.7.4.0"),sQuery(id+"F0.wireOp",EDGE,"E1.7.5.0"),sQuery(id+"F0.wireOp",EDGE,"E1.7.6.0"),sQuery(id+"F0.wireOp",EDGE,"E1.7.7.0"),sQuery(id+"F0.wireOp",EDGE,"E1.7.8.0"),sQuery(id+"F0.wireOp",EDGE,"E1.7.9.0"),sQuery(id+"F0.wireOp",EDGE,"E1.7.10.0"),sQuery(id+"F0.wireOp",EDGE,"E1.7.11.0"),sQuery(id+"F0.wireOp",EDGE,"E1.7.12.0"),sQuery(id+"F0.wireOp",EDGE,"E1.7.13.0"),sQuery(id+"F0.wireOp",EDGE,"E1.7.14.0"),sQuery(id+"F0.wireOp",EDGE,"E1.7.15.0"),sQuery(id+"F0.wireOp",EDGE,"E1.7.16.0"),sQuery(id+"F0.wireOp",EDGE,"E1.7.17.0"),sQuery(id+"F0.wireOp",EDGE,"E1.7.18.0"),sQuery(id+"F0.wireOp",EDGE,"E1.7.19.0"),sQuery(id+"F0.wireOp",EDGE,"E1.7.20.0"),sQuery(id+"F0.wireOp",EDGE,"E1.7.21.0"),sQuery(id+"F0.wireOp",EDGE,"E1.7.22.0"),sQuery(id+"F0.wireOp",EDGE,"E1.7.23.0"),sQuery(id+"F0.wireOp",EDGE,"E1.7.24.0"),sQuery(id+"F0.wireOp",EDGE,"E1.7.25.0"),sQuery(id+"F0.wireOp",EDGE,"E1.7.26.0"),sQuery(id+"F0.wireOp",EDGE,"E1.7.27.0"),sQuery(id+"F0.wireOp",EDGE,"E1.7.28.0"),sQuery(id+"F0.wireOp",EDGE,"E1.7.29.0"),sQuery(id+"F0.wireOp",EDGE,"E1.8.0.0"),sQuery(id+"F0.wireOp",EDGE,"E1.8.1.0"),sQuery(id+"F0.wireOp",EDGE,"E1.8.2.0"),sQuery(id+"F0.wireOp",EDGE,"E1.8.3.0"),sQuery(id+"F0.wireOp",EDGE,"E1.8.4.0"),sQuery(id+"F0.wireOp",EDGE,"E1.8.5.0"),sQuery(id+"F0.wireOp",EDGE,"E1.8.6.0"),sQuery(id+"F0.wireOp",EDGE,"E1.8.7.0"),sQuery(id+"F0.wireOp",EDGE,"E1.8.8.0"),sQuery(id+"F0.wireOp",EDGE,"E1.8.9.0"),sQuery(id+"F0.wireOp",EDGE,"E1.8.10.0"),sQuery(id+"F0.wireOp",EDGE,"E1.8.11.0"),sQuery(id+"F0.wireOp",EDGE,"E1.8.12.0"),sQuery(id+"F0.wireOp",EDGE,"E1.8.13.0"),sQuery(id+"F0.wireOp",EDGE,"E1.8.14.0"),sQuery(id+"F0.wireOp",EDGE,"E1.8.15.0"),sQuery(id+"F0.wireOp",EDGE,"E1.8.16.0"),sQuery(id+"F0.wireOp",EDGE,"E1.8.17.0"),sQuery(id+"F0.wireOp",EDGE,"E1.8.18.0"),sQuery(id+"F0.wireOp",EDGE,"E1.8.19.0"),sQuery(id+"F0.wireOp",EDGE,"E1.8.20.0"),sQuery(id+"F0.wireOp",EDGE,"E1.8.21.0"),sQuery(id+"F0.wireOp",EDGE,"E1.8.22.0"),sQuery(id+"F0.wireOp",EDGE,"E1.8.23.0"),sQuery(id+"F0.wireOp",EDGE,"E1.8.24.0"),sQuery(id+"F0.wireOp",EDGE,"E1.8.25.0"),sQuery(id+"F0.wireOp",EDGE,"E1.8.26.0"),sQuery(id+"F0.wireOp",EDGE,"E1.8.27.0"),sQuery(id+"F0.wireOp",EDGE,"E1.8.28.0"),sQuery(id+"F0.wireOp",EDGE,"E1.8.29.0"),sQuery(id+"F0.wireOp",EDGE,"E1.9.0.0"),sQuery(id+"F0.wireOp",EDGE,"E1.9.1.0"),sQuery(id+"F0.wireOp",EDGE,"E1.9.2.0"),sQuery(id+"F0.wireOp",EDGE,"E1.9.3.0"),sQuery(id+"F0.wireOp",EDGE,"E1.9.4.0"),sQuery(id+"F0.wireOp",EDGE,"E1.9.5.0"),sQuery(id+"F0.wireOp",EDGE,"E1.9.6.0"),sQuery(id+"F0.wireOp",EDGE,"E1.9.7.0"),sQuery(id+"F0.wireOp",EDGE,"E1.9.8.0"),sQuery(id+"F0.wireOp",EDGE,"E1.9.9.0"),sQuery(id+"F0.wireOp",EDGE,"E1.9.10.0"),sQuery(id+"F0.wireOp",EDGE,"E1.9.11.0"),sQuery(id+"F0.wireOp",EDGE,"E1.9.12.0"),sQuery(id+"F0.wireOp",EDGE,"E1.9.13.0"),sQuery(id+"F0.wireOp",EDGE,"E1.9.14.0"),sQuery(id+"F0.wireOp",EDGE,"E1.9.15.0"),sQuery(id+"F0.wireOp",EDGE,"E1.9.16.0"),sQuery(id+"F0.wireOp",EDGE,"E1.9.17.0"),sQuery(id+"F0.wireOp",EDGE,"E1.9.18.0"),sQuery(id+"F0.wireOp",EDGE,"E1.9.19.0"),sQuery(id+"F0.wireOp",EDGE,"E1.9.20.0"),sQuery(id+"F0.wireOp",EDGE,"E1.9.21.0"),sQuery(id+"F0.wireOp",EDGE,"E1.9.22.0"),sQuery(id+"F0.wireOp",EDGE,"E1.9.23.0"),sQuery(id+"F0.wireOp",EDGE,"E1.9.24.0"),sQuery(id+"F0.wireOp",EDGE,"E1.9.25.0"),sQuery(id+"F0.wireOp",EDGE,"E1.9.26.0"),sQuery(id+"F0.wireOp",EDGE,"E1.9.27.0"),sQuery(id+"F0.wireOp",EDGE,"E1.9.28.0"),sQuery(id+"F0.wireOp",EDGE,"E1.9.29.0"),sQuery(id+"F0.wireOp",EDGE,"E1.10.0.0"),sQuery(id+"F0.wireOp",EDGE,"E1.10.1.0"),sQuery(id+"F0.wireOp",EDGE,"E1.10.2.0"),sQuery(id+"F0.wireOp",EDGE,"E1.10.3.0"),sQuery(id+"F0.wireOp",EDGE,"E1.10.4.0"),sQuery(id+"F0.wireOp",EDGE,"E1.10.5.0"),sQuery(id+"F0.wireOp",EDGE,"E1.10.6.0"),sQuery(id+"F0.wireOp",EDGE,"E1.10.7.0"),sQuery(id+"F0.wireOp",EDGE,"E1.10.8.0"),sQuery(id+"F0.wireOp",EDGE,"E1.10.9.0"),sQuery(id+"F0.wireOp",EDGE,"E1.10.10.0"),sQuery(id+"F0.wireOp",EDGE,"E1.10.11.0"),sQuery(id+"F0.wireOp",EDGE,"E1.10.12.0"),sQuery(id+"F0.wireOp",EDGE,"E1.10.13.0"),sQuery(id+"F0.wireOp",EDGE,"E1.10.14.0"),sQuery(id+"F0.wireOp",EDGE,"E1.10.15.0"),sQuery(id+"F0.wireOp",EDGE,"E1.10.16.0"),sQuery(id+"F0.wireOp",EDGE,"E1.10.17.0"),sQuery(id+"F0.wireOp",EDGE,"E1.10.18.0"),sQuery(id+"F0.wireOp",EDGE,"E1.10.19.0"),sQuery(id+"F0.wireOp",EDGE,"E1.10.20.0"),sQuery(id+"F0.wireOp",EDGE,"E1.10.21.0"),sQuery(id+"F0.wireOp",EDGE,"E1.10.22.0"),sQuery(id+"F0.wireOp",EDGE,"E1.10.23.0"),sQuery(id+"F0.wireOp",EDGE,"E1.10.24.0"),sQuery(id+"F0.wireOp",EDGE,"E1.10.25.0"),sQuery(id+"F0.wireOp",EDGE,"E1.10.26.0"),sQuery(id+"F0.wireOp",EDGE,"E1.10.27.0"),sQuery(id+"F0.wireOp",EDGE,"E1.10.28.0"),sQuery(id+"F0.wireOp",EDGE,"E1.10.29.0"),sQuery(id+"F0.wireOp",EDGE,"E1.11.0.0"),sQuery(id+"F0.wireOp",EDGE,"E1.11.1.0"),sQuery(id+"F0.wireOp",EDGE,"E1.11.2.0"),sQuery(id+"F0.wireOp",EDGE,"E1.11.3.0"),sQuery(id+"F0.wireOp",EDGE,"E1.11.4.0"),sQuery(id+"F0.wireOp",EDGE,"E1.11.5.0"),sQuery(id+"F0.wireOp",EDGE,"E1.11.6.0"),sQuery(id+"F0.wireOp",EDGE,"E1.11.7.0"),sQuery(id+"F0.wireOp",EDGE,"E1.11.8.0"),sQuery(id+"F0.wireOp",EDGE,"E1.11.9.0"),sQuery(id+"F0.wireOp",EDGE,"E1.11.10.0"),sQuery(id+"F0.wireOp",EDGE,"E1.11.11.0"),sQuery(id+"F0.wireOp",EDGE,"E1.11.12.0"),sQuery(id+"F0.wireOp",EDGE,"E1.11.13.0"),sQuery(id+"F0.wireOp",EDGE,"E1.11.14.0"),sQuery(id+"F0.wireOp",EDGE,"E1.11.15.0"),sQuery(id+"F0.wireOp",EDGE,"E1.11.16.0"),sQuery(id+"F0.wireOp",EDGE,"E1.11.17.0"),sQuery(id+"F0.wireOp",EDGE,"E1.11.18.0"),sQuery(id+"F0.wireOp",EDGE,"E1.11.19.0"),sQuery(id+"F0.wireOp",EDGE,"E1.11.20.0"),sQuery(id+"F0.wireOp",EDGE,"E1.11.21.0"),sQuery(id+"F0.wireOp",EDGE,"E1.11.22.0"),sQuery(id+"F0.wireOp",EDGE,"E1.11.23.0"),sQuery(id+"F0.wireOp",EDGE,"E1.11.24.0"),sQuery(id+"F0.wireOp",EDGE,"E1.11.25.0"),sQuery(id+"F0.wireOp",EDGE,"E1.11.26.0"),sQuery(id+"F0.wireOp",EDGE,"E1.11.27.0"),sQuery(id+"F0.wireOp",EDGE,"E1.11.28.0"),sQuery(id+"F0.wireOp",EDGE,"E1.11.29.0"),sQuery(id+"F0.wireOp",EDGE,"E1.12.0.0"),sQuery(id+"F0.wireOp",EDGE,"E1.12.1.0"),sQuery(id+"F0.wireOp",EDGE,"E1.12.2.0"),sQuery(id+"F0.wireOp",EDGE,"E1.12.3.0"),sQuery(id+"F0.wireOp",EDGE,"E1.12.4.0"),sQuery(id+"F0.wireOp",EDGE,"E1.12.5.0"),sQuery(id+"F0.wireOp",EDGE,"E1.12.6.0"),sQuery(id+"F0.wireOp",EDGE,"E1.12.7.0"),sQuery(id+"F0.wireOp",EDGE,"E1.12.8.0"),sQuery(id+"F0.wireOp",EDGE,"E1.12.9.0"),sQuery(id+"F0.wireOp",EDGE,"E1.12.10.0"),sQuery(id+"F0.wireOp",EDGE,"E1.12.11.0"),sQuery(id+"F0.wireOp",EDGE,"E1.12.12.0"),sQuery(id+"F0.wireOp",EDGE,"E1.12.13.0"),sQuery(id+"F0.wireOp",EDGE,"E1.12.14.0"),sQuery(id+"F0.wireOp",EDGE,"E1.12.15.0"),sQuery(id+"F0.wireOp",EDGE,"E1.12.16.0"),sQuery(id+"F0.wireOp",EDGE,"E1.12.17.0"),sQuery(id+"F0.wireOp",EDGE,"E1.12.18.0"),sQuery(id+"F0.wireOp",EDGE,"E1.12.19.0"),sQuery(id+"F0.wireOp",EDGE,"E1.12.20.0"),sQuery(id+"F0.wireOp",EDGE,"E1.12.21.0"),sQuery(id+"F0.wireOp",EDGE,"E1.12.22.0"),sQuery(id+"F0.wireOp",EDGE,"E1.12.23.0"),sQuery(id+"F0.wireOp",EDGE,"E1.12.24.0"),sQuery(id+"F0.wireOp",EDGE,"E1.12.25.0"),sQuery(id+"F0.wireOp",EDGE,"E1.12.26.0"),sQuery(id+"F0.wireOp",EDGE,"E1.12.27.0"),sQuery(id+"F0.wireOp",EDGE,"E1.12.28.0"),sQuery(id+"F0.wireOp",EDGE,"E1.12.29.0"),sQuery(id+"F0.wireOp",EDGE,"E1.13.0.0"),sQuery(id+"F0.wireOp",EDGE,"E1.13.1.0"),sQuery(id+"F0.wireOp",EDGE,"E1.13.2.0"),sQuery(id+"F0.wireOp",EDGE,"E1.13.3.0"),sQuery(id+"F0.wireOp",EDGE,"E1.13.4.0"),sQuery(id+"F0.wireOp",EDGE,"E1.13.5.0"),sQuery(id+"F0.wireOp",EDGE,"E1.13.6.0"),sQuery(id+"F0.wireOp",EDGE,"E1.13.7.0"),sQuery(id+"F0.wireOp",EDGE,"E1.13.8.0"),sQuery(id+"F0.wireOp",EDGE,"E1.13.9.0"),sQuery(id+"F0.wireOp",EDGE,"E1.13.10.0"),sQuery(id+"F0.wireOp",EDGE,"E1.13.11.0"),sQuery(id+"F0.wireOp",EDGE,"E1.13.12.0"),sQuery(id+"F0.wireOp",EDGE,"E1.13.13.0"),sQuery(id+"F0.wireOp",EDGE,"E1.13.14.0"),sQuery(id+"F0.wireOp",EDGE,"E1.13.15.0"),sQuery(id+"F0.wireOp",EDGE,"E1.13.16.0"),sQuery(id+"F0.wireOp",EDGE,"E1.13.17.0"),sQuery(id+"F0.wireOp",EDGE,"E1.13.18.0"),sQuery(id+"F0.wireOp",EDGE,"E1.13.19.0"),sQuery(id+"F0.wireOp",EDGE,"E1.13.20.0"),sQuery(id+"F0.wireOp",EDGE,"E1.13.21.0"),sQuery(id+"F0.wireOp",EDGE,"E1.13.22.0"),sQuery(id+"F0.wireOp",EDGE,"E1.13.23.0"),sQuery(id+"F0.wireOp",EDGE,"E1.13.24.0"),sQuery(id+"F0.wireOp",EDGE,"E1.13.25.0"),sQuery(id+"F0.wireOp",EDGE,"E1.13.26.0"),sQuery(id+"F0.wireOp",EDGE,"E1.13.27.0"),sQuery(id+"F0.wireOp",EDGE,"E1.13.28.0"),sQuery(id+"F0.wireOp",EDGE,"E1.13.29.0"),sQuery(id+"F0.wireOp",EDGE,"E1.14.0.0"),sQuery(id+"F0.wireOp",EDGE,"E1.14.1.0"),sQuery(id+"F0.wireOp",EDGE,"E1.14.2.0"),sQuery(id+"F0.wireOp",EDGE,"E1.14.3.0"),sQuery(id+"F0.wireOp",EDGE,"E1.14.4.0"),sQuery(id+"F0.wireOp",EDGE,"E1.14.5.0"),sQuery(id+"F0.wireOp",EDGE,"E1.14.6.0"),sQuery(id+"F0.wireOp",EDGE,"E1.14.7.0"),sQuery(id+"F0.wireOp",EDGE,"E1.14.8.0"),sQuery(id+"F0.wireOp",EDGE,"E1.14.9.0"),sQuery(id+"F0.wireOp",EDGE,"E1.14.10.0"),sQuery(id+"F0.wireOp",EDGE,"E1.14.11.0"),sQuery(id+"F0.wireOp",EDGE,"E1.14.12.0"),sQuery(id+"F0.wireOp",EDGE,"E1.14.13.0"),sQuery(id+"F0.wireOp",EDGE,"E1.14.14.0"),sQuery(id+"F0.wireOp",EDGE,"E1.14.15.0"),sQuery(id+"F0.wireOp",EDGE,"E1.14.16.0"),sQuery(id+"F0.wireOp",EDGE,"E1.14.17.0"),sQuery(id+"F0.wireOp",EDGE,"E1.14.18.0"),sQuery(id+"F0.wireOp",EDGE,"E1.14.19.0"),sQuery(id+"F0.wireOp",EDGE,"E1.14.20.0"),sQuery(id+"F0.wireOp",EDGE,"E1.14.21.0"),sQuery(id+"F0.wireOp",EDGE,"E1.14.22.0"),sQuery(id+"F0.wireOp",EDGE,"E1.14.23.0"),sQuery(id+"F0.wireOp",EDGE,"E1.14.24.0"),sQuery(id+"F0.wireOp",EDGE,"E1.14.25.0"),sQuery(id+"F0.wireOp",EDGE,"E1.14.26.0"),sQuery(id+"F0.wireOp",EDGE,"E1.14.27.0"),sQuery(id+"F0.wireOp",EDGE,"E1.14.28.0"),sQuery(id+"F0.wireOp",EDGE,"E1.14.29.0"),sQuery(id+"F0.wireOp",EDGE,"E1.15.0.0"),sQuery(id+"F0.wireOp",EDGE,"E1.15.1.0"),sQuery(id+"F0.wireOp",EDGE,"E1.15.2.0"),sQuery(id+"F0.wireOp",EDGE,"E1.15.3.0"),sQuery(id+"F0.wireOp",EDGE,"E1.15.4.0"),sQuery(id+"F0.wireOp",EDGE,"E1.15.5.0"),sQuery(id+"F0.wireOp",EDGE,"E1.15.6.0"),sQuery(id+"F0.wireOp",EDGE,"E1.15.7.0"),sQuery(id+"F0.wireOp",EDGE,"E1.15.8.0"),sQuery(id+"F0.wireOp",EDGE,"E1.15.9.0"),sQuery(id+"F0.wireOp",EDGE,"E1.15.10.0"),sQuery(id+"F0.wireOp",EDGE,"E1.15.11.0"),sQuery(id+"F0.wireOp",EDGE,"E1.15.12.0"),sQuery(id+"F0.wireOp",EDGE,"E1.15.13.0"),sQuery(id+"F0.wireOp",EDGE,"E1.15.14.0"),sQuery(id+"F0.wireOp",EDGE,"E1.15.15.0"),sQuery(id+"F0.wireOp",EDGE,"E1.15.16.0"),sQuery(id+"F0.wireOp",EDGE,"E1.15.17.0"),sQuery(id+"F0.wireOp",EDGE,"E1.15.18.0"),sQuery(id+"F0.wireOp",EDGE,"E1.15.19.0"),sQuery(id+"F0.wireOp",EDGE,"E1.15.20.0"),sQuery(id+"F0.wireOp",EDGE,"E1.15.21.0"),sQuery(id+"F0.wireOp",EDGE,"E1.15.22.0"),sQuery(id+"F0.wireOp",EDGE,"E1.15.23.0"),sQuery(id+"F0.wireOp",EDGE,"E1.15.24.0"),sQuery(id+"F0.wireOp",EDGE,"E1.15.25.0"),sQuery(id+"F0.wireOp",EDGE,"E1.15.26.0"),sQuery(id+"F0.wireOp",EDGE,"E1.15.27.0"),sQuery(id+"F0.wireOp",EDGE,"E1.15.28.0"),sQuery(id+"F0.wireOp",EDGE,"E1.15.29.0"),sQuery(id+"F0.wireOp",EDGE,"E1.16.0.0"),sQuery(id+"F0.wireOp",EDGE,"E1.16.1.0"),sQuery(id+"F0.wireOp",EDGE,"E1.16.2.0"),sQuery(id+"F0.wireOp",EDGE,"E1.16.3.0"),sQuery(id+"F0.wireOp",EDGE,"E1.16.4.0"),sQuery(id+"F0.wireOp",EDGE,"E1.16.5.0"),sQuery(id+"F0.wireOp",EDGE,"E1.16.6.0"),sQuery(id+"F0.wireOp",EDGE,"E1.16.7.0"),sQuery(id+"F0.wireOp",EDGE,"E1.16.8.0"),sQuery(id+"F0.wireOp",EDGE,"E1.16.9.0"),sQuery(id+"F0.wireOp",EDGE,"E1.16.10.0"),sQuery(id+"F0.wireOp",EDGE,"E1.16.11.0"),sQuery(id+"F0.wireOp",EDGE,"E1.16.12.0"),sQuery(id+"F0.wireOp",EDGE,"E1.16.13.0"),sQuery(id+"F0.wireOp",EDGE,"E1.16.14.0"),sQuery(id+"F0.wireOp",EDGE,"E1.16.15.0"),sQuery(id+"F0.wireOp",EDGE,"E1.16.16.0"),sQuery(id+"F0.wireOp",EDGE,"E1.16.17.0"),sQuery(id+"F0.wireOp",EDGE,"E1.16.18.0"),sQuery(id+"F0.wireOp",EDGE,"E1.16.19.0"),sQuery(id+"F0.wireOp",EDGE,"E1.16.20.0"),sQuery(id+"F0.wireOp",EDGE,"E1.16.21.0"),sQuery(id+"F0.wireOp",EDGE,"E1.16.22.0"),sQuery(id+"F0.wireOp",EDGE,"E1.16.23.0"),sQuery(id+"F0.wireOp",EDGE,"E1.16.24.0"),sQuery(id+"F0.wireOp",EDGE,"E1.16.25.0"),sQuery(id+"F0.wireOp",EDGE,"E1.16.26.0"),sQuery(id+"F0.wireOp",EDGE,"E1.16.27.0"),sQuery(id+"F0.wireOp",EDGE,"E1.16.28.0"),sQuery(id+"F0.wireOp",EDGE,"E1.16.29.0"),sQuery(id+"F0.wireOp",EDGE,"E1.17.0.0"),sQuery(id+"F0.wireOp",EDGE,"E1.17.1.0"),sQuery(id+"F0.wireOp",EDGE,"E1.17.2.0"),sQuery(id+"F0.wireOp",EDGE,"E1.17.3.0"),sQuery(id+"F0.wireOp",EDGE,"E1.17.4.0"),sQuery(id+"F0.wireOp",EDGE,"E1.17.5.0"),sQuery(id+"F0.wireOp",EDGE,"E1.17.6.0"),sQuery(id+"F0.wireOp",EDGE,"E1.17.7.0"),sQuery(id+"F0.wireOp",EDGE,"E1.17.8.0"),sQuery(id+"F0.wireOp",EDGE,"E1.17.9.0"),sQuery(id+"F0.wireOp",EDGE,"E1.17.10.0"),sQuery(id+"F0.wireOp",EDGE,"E1.17.11.0"),sQuery(id+"F0.wireOp",EDGE,"E1.17.12.0"),sQuery(id+"F0.wireOp",EDGE,"E1.17.13.0"),sQuery(id+"F0.wireOp",EDGE,"E1.17.14.0"),sQuery(id+"F0.wireOp",EDGE,"E1.17.15.0"),sQuery(id+"F0.wireOp",EDGE,"E1.17.16.0"),sQuery(id+"F0.wireOp",EDGE,"E1.17.17.0"),sQuery(id+"F0.wireOp",EDGE,"E1.17.18.0"),sQuery(id+"F0.wireOp",EDGE,"E1.17.19.0"),sQuery(id+"F0.wireOp",EDGE,"E1.17.20.0"),sQuery(id+"F0.wireOp",EDGE,"E1.17.21.0"),sQuery(id+"F0.wireOp",EDGE,"E1.17.22.0"),sQuery(id+"F0.wireOp",EDGE,"E1.17.23.0"),sQuery(id+"F0.wireOp",EDGE,"E1.17.24.0"),sQuery(id+"F0.wireOp",EDGE,"E1.17.25.0"),sQuery(id+"F0.wireOp",EDGE,"E1.17.26.0"),sQuery(id+"F0.wireOp",EDGE,"E1.17.27.0"),sQuery(id+"F0.wireOp",EDGE,"E1.17.28.0"),sQuery(id+"F0.wireOp",EDGE,"E1.17.29.0"),sQuery(id+"F0.wireOp",EDGE,"E1.18.0.0"),sQuery(id+"F0.wireOp",EDGE,"E1.18.1.0"),sQuery(id+"F0.wireOp",EDGE,"E1.18.2.0"),sQuery(id+"F0.wireOp",EDGE,"E1.18.3.0"),sQuery(id+"F0.wireOp",EDGE,"E1.18.4.0"),sQuery(id+"F0.wireOp",EDGE,"E1.18.5.0"),sQuery(id+"F0.wireOp",EDGE,"E1.18.6.0"),sQuery(id+"F0.wireOp",EDGE,"E1.18.7.0"),sQuery(id+"F0.wireOp",EDGE,"E1.18.8.0"),sQuery(id+"F0.wireOp",EDGE,"E1.18.9.0"),sQuery(id+"F0.wireOp",EDGE,"E1.18.10.0"),sQuery(id+"F0.wireOp",EDGE,"E1.18.11.0"),sQuery(id+"F0.wireOp",EDGE,"E1.18.12.0"),sQuery(id+"F0.wireOp",EDGE,"E1.18.13.0"),sQuery(id+"F0.wireOp",EDGE,"E1.18.14.0"),sQuery(id+"F0.wireOp",EDGE,"E1.18.15.0"),sQuery(id+"F0.wireOp",EDGE,"E1.18.16.0"),sQuery(id+"F0.wireOp",EDGE,"E1.18.17.0"),sQuery(id+"F0.wireOp",EDGE,"E1.18.18.0"),sQuery(id+"F0.wireOp",EDGE,"E1.18.19.0"),sQuery(id+"F0.wireOp",EDGE,"E1.18.20.0"),sQuery(id+"F0.wireOp",EDGE,"E1.18.21.0"),sQuery(id+"F0.wireOp",EDGE,"E1.18.22.0"),sQuery(id+"F0.wireOp",EDGE,"E1.18.23.0"),sQuery(id+"F0.wireOp",EDGE,"E1.18.24.0"),sQuery(id+"F0.wireOp",EDGE,"E1.18.25.0"),sQuery(id+"F0.wireOp",EDGE,"E1.18.26.0"),sQuery(id+"F0.wireOp",EDGE,"E1.18.27.0"),sQuery(id+"F0.wireOp",EDGE,"E1.18.28.0"),sQuery(id+"F0.wireOp",EDGE,"E1.18.29.0"),sQuery(id+"F0.wireOp",EDGE,"E1.19.0.0"),sQuery(id+"F0.wireOp",EDGE,"E1.19.1.0"),sQuery(id+"F0.wireOp",EDGE,"E1.19.2.0"),sQuery(id+"F0.wireOp",EDGE,"E1.19.3.0"),sQuery(id+"F0.wireOp",EDGE,"E1.19.4.0"),sQuery(id+"F0.wireOp",EDGE,"E1.19.5.0"),sQuery(id+"F0.wireOp",EDGE,"E1.19.6.0"),sQuery(id+"F0.wireOp",EDGE,"E1.19.7.0"),sQuery(id+"F0.wireOp",EDGE,"E1.19.8.0"),sQuery(id+"F0.wireOp",EDGE,"E1.19.9.0"),sQuery(id+"F0.wireOp",EDGE,"E1.19.10.0"),sQuery(id+"F0.wireOp",EDGE,"E1.19.11.0"),sQuery(id+"F0.wireOp",EDGE,"E1.19.12.0"),sQuery(id+"F0.wireOp",EDGE,"E1.19.13.0"),sQuery(id+"F0.wireOp",EDGE,"E1.19.14.0"),sQuery(id+"F0.wireOp",EDGE,"E1.19.15.0"),sQuery(id+"F0.wireOp",EDGE,"E1.19.16.0"),sQuery(id+"F0.wireOp",EDGE,"E1.19.17.0"),sQuery(id+"F0.wireOp",EDGE,"E1.19.18.0"),sQuery(id+"F0.wireOp",EDGE,"E1.19.19.0"),sQuery(id+"F0.wireOp",EDGE,"E1.19.20.0"),sQuery(id+"F0.wireOp",EDGE,"E1.19.21.0"),sQuery(id+"F0.wireOp",EDGE,"E1.19.22.0"),sQuery(id+"F0.wireOp",EDGE,"E1.19.23.0"),sQuery(id+"F0.wireOp",EDGE,"E1.19.24.0"),sQuery(id+"F0.wireOp",EDGE,"E1.19.25.0"),sQuery(id+"F0.wireOp",EDGE,"E1.19.26.0"),sQuery(id+"F0.wireOp",EDGE,"E1.19.27.0"),sQuery(id+"F0.wireOp",EDGE,"E1.19.28.0"),sQuery(id+"F0.wireOp",EDGE,"E1.19.29.0"),sQuery(id+"F0.wireOp",EDGE,"E1.20.0.0"),sQuery(id+"F0.wireOp",EDGE,"E1.20.1.0"),sQuery(id+"F0.wireOp",EDGE,"E1.20.2.0"),sQuery(id+"F0.wireOp",EDGE,"E1.20.3.0"),sQuery(id+"F0.wireOp",EDGE,"E1.20.4.0"),sQuery(id+"F0.wireOp",EDGE,"E1.20.5.0"),sQuery(id+"F0.wireOp",EDGE,"E1.20.6.0"),sQuery(id+"F0.wireOp",EDGE,"E1.20.7.0"),sQuery(id+"F0.wireOp",EDGE,"E1.20.8.0"),sQuery(id+"F0.wireOp",EDGE,"E1.20.9.0"),sQuery(id+"F0.wireOp",EDGE,"E1.20.10.0"),sQuery(id+"F0.wireOp",EDGE,"E1.20.11.0"),sQuery(id+"F0.wireOp",EDGE,"E1.20.12.0"),sQuery(id+"F0.wireOp",EDGE,"E1.20.13.0"),sQuery(id+"F0.wireOp",EDGE,"E1.20.14.0"),sQuery(id+"F0.wireOp",EDGE,"E1.20.15.0"),sQuery(id+"F0.wireOp",EDGE,"E1.20.16.0"),sQuery(id+"F0.wireOp",EDGE,"E1.20.17.0"),sQuery(id+"F0.wireOp",EDGE,"E1.20.18.0"),sQuery(id+"F0.wireOp",EDGE,"E1.20.19.0"),sQuery(id+"F0.wireOp",EDGE,"E1.20.20.0"),sQuery(id+"F0.wireOp",EDGE,"E1.20.21.0"),sQuery(id+"F0.wireOp",EDGE,"E1.20.22.0"),sQuery(id+"F0.wireOp",EDGE,"E1.20.23.0"),sQuery(id+"F0.wireOp",EDGE,"E1.20.24.0"),sQuery(id+"F0.wireOp",EDGE,"E1.20.25.0"),sQuery(id+"F0.wireOp",EDGE,"E1.20.26.0"),sQuery(id+"F0.wireOp",EDGE,"E1.20.27.0"),sQuery(id+"F0.wireOp",EDGE,"E1.20.28.0"),sQuery(id+"F0.wireOp",EDGE,"E1.20.29.0"),sQuery(id+"F0.wireOp",EDGE,"E1.21.0.0"),sQuery(id+"F0.wireOp",EDGE,"E1.21.1.0"),sQuery(id+"F0.wireOp",EDGE,"E1.21.2.0"),sQuery(id+"F0.wireOp",EDGE,"E1.21.3.0"),sQuery(id+"F0.wireOp",EDGE,"E1.21.4.0"),sQuery(id+"F0.wireOp",EDGE,"E1.21.5.0"),sQuery(id+"F0.wireOp",EDGE,"E1.21.6.0"),sQuery(id+"F0.wireOp",EDGE,"E1.21.7.0"),sQuery(id+"F0.wireOp",EDGE,"E1.21.8.0"),sQuery(id+"F0.wireOp",EDGE,"E1.21.9.0"),sQuery(id+"F0.wireOp",EDGE,"E1.21.10.0"),sQuery(id+"F0.wireOp",EDGE,"E1.21.11.0"),sQuery(id+"F0.wireOp",EDGE,"E1.21.12.0"),sQuery(id+"F0.wireOp",EDGE,"E1.21.13.0"),sQuery(id+"F0.wireOp",EDGE,"E1.21.14.0"),sQuery(id+"F0.wireOp",EDGE,"E1.21.15.0"),sQuery(id+"F0.wireOp",EDGE,"E1.21.16.0"),sQuery(id+"F0.wireOp",EDGE,"E1.21.17.0"),sQuery(id+"F0.wireOp",EDGE,"E1.21.18.0"),sQuery(id+"F0.wireOp",EDGE,"E1.21.19.0"),sQuery(id+"F0.wireOp",EDGE,"E1.21.20.0"),sQuery(id+"F0.wireOp",EDGE,"E1.21.21.0"),sQuery(id+"F0.wireOp",EDGE,"E1.21.22.0"),sQuery(id+"F0.wireOp",EDGE,"E1.21.23.0"),sQuery(id+"F0.wireOp",EDGE,"E1.21.24.0"),sQuery(id+"F0.wireOp",EDGE,"E1.21.25.0"),sQuery(id+"F0.wireOp",EDGE,"E1.21.26.0"),sQuery(id+"F0.wireOp",EDGE,"E1.21.27.0"),sQuery(id+"F0.wireOp",EDGE,"E1.21.28.0"),sQuery(id+"F0.wireOp",EDGE,"E1.21.29.0"),sQuery(id+"F0.wireOp",EDGE,"E1.22.0.0"),sQuery(id+"F0.wireOp",EDGE,"E1.22.1.0"),sQuery(id+"F0.wireOp",EDGE,"E1.22.2.0"),sQuery(id+"F0.wireOp",EDGE,"E1.22.3.0"),sQuery(id+"F0.wireOp",EDGE,"E1.22.4.0"),sQuery(id+"F0.wireOp",EDGE,"E1.22.5.0"),sQuery(id+"F0.wireOp",EDGE,"E1.22.6.0"),sQuery(id+"F0.wireOp",EDGE,"E1.22.7.0"),sQuery(id+"F0.wireOp",EDGE,"E1.22.8.0"),sQuery(id+"F0.wireOp",EDGE,"E1.22.9.0"),sQuery(id+"F0.wireOp",EDGE,"E1.22.10.0"),sQuery(id+"F0.wireOp",EDGE,"E1.22.11.0"),sQuery(id+"F0.wireOp",EDGE,"E1.22.12.0"),sQuery(id+"F0.wireOp",EDGE,"E1.22.13.0"),sQuery(id+"F0.wireOp",EDGE,"E1.22.14.0"),sQuery(id+"F0.wireOp",EDGE,"E1.22.15.0"),sQuery(id+"F0.wireOp",EDGE,"E1.22.16.0"),sQuery(id+"F0.wireOp",EDGE,"E1.22.17.0"),sQuery(id+"F0.wireOp",EDGE,"E1.22.18.0"),sQuery(id+"F0.wireOp",EDGE,"E1.22.19.0"),sQuery(id+"F0.wireOp",EDGE,"E1.22.20.0"),sQuery(id+"F0.wireOp",EDGE,"E1.22.21.0"),sQuery(id+"F0.wireOp",EDGE,"E1.22.22.0"),sQuery(id+"F0.wireOp",EDGE,"E1.22.23.0"),sQuery(id+"F0.wireOp",EDGE,"E1.22.24.0"),sQuery(id+"F0.wireOp",EDGE,"E1.22.25.0"),sQuery(id+"F0.wireOp",EDGE,"E1.22.26.0"),sQuery(id+"F0.wireOp",EDGE,"E1.22.27.0"),sQuery(id+"F0.wireOp",EDGE,"E1.22.28.0"),sQuery(id+"F0.wireOp",EDGE,"E1.22.29.0"),sQuery(id+"F0.wireOp",EDGE,"E1.23.0.0"),sQuery(id+"F0.wireOp",EDGE,"E1.23.1.0"),sQuery(id+"F0.wireOp",EDGE,"E1.23.2.0"),sQuery(id+"F0.wireOp",EDGE,"E1.23.3.0"),sQuery(id+"F0.wireOp",EDGE,"E1.23.4.0"),sQuery(id+"F0.wireOp",EDGE,"E1.23.5.0"),sQuery(id+"F0.wireOp",EDGE,"E1.23.6.0"),sQuery(id+"F0.wireOp",EDGE,"E1.23.7.0"),sQuery(id+"F0.wireOp",EDGE,"E1.23.8.0"),sQuery(id+"F0.wireOp",EDGE,"E1.23.9.0"),sQuery(id+"F0.wireOp",EDGE,"E1.23.10.0"),sQuery(id+"F0.wireOp",EDGE,"E1.23.11.0"),sQuery(id+"F0.wireOp",EDGE,"E1.23.12.0"),sQuery(id+"F0.wireOp",EDGE,"E1.23.13.0"),sQuery(id+"F0.wireOp",EDGE,"E1.23.14.0"),sQuery(id+"F0.wireOp",EDGE,"E1.23.15.0"),sQuery(id+"F0.wireOp",EDGE,"E1.23.16.0"),sQuery(id+"F0.wireOp",EDGE,"E1.23.17.0"),sQuery(id+"F0.wireOp",EDGE,"E1.23.18.0"),sQuery(id+"F0.wireOp",EDGE,"E1.23.19.0"),sQuery(id+"F0.wireOp",EDGE,"E1.23.20.0"),sQuery(id+"F0.wireOp",EDGE,"E1.23.21.0"),sQuery(id+"F0.wireOp",EDGE,"E1.23.22.0"),sQuery(id+"F0.wireOp",EDGE,"E1.23.23.0"),sQuery(id+"F0.wireOp",EDGE,"E1.23.24.0"),sQuery(id+"F0.wireOp",EDGE,"E1.23.25.0"),sQuery(id+"F0.wireOp",EDGE,"E1.23.26.0"),sQuery(id+"F0.wireOp",EDGE,"E1.23.27.0"),sQuery(id+"F0.wireOp",EDGE,"E1.23.28.0"),sQuery(id+"F0.wireOp",EDGE,"E1.23.29.0"),sQuery(id+"F0.wireOp",EDGE,"E1.24.0.0"),sQuery(id+"F0.wireOp",EDGE,"E1.24.1.0"),sQuery(id+"F0.wireOp",EDGE,"E1.24.2.0"),sQuery(id+"F0.wireOp",EDGE,"E1.24.3.0"),sQuery(id+"F0.wireOp",EDGE,"E1.24.4.0"),sQuery(id+"F0.wireOp",EDGE,"E1.24.5.0"),sQuery(id+"F0.wireOp",EDGE,"E1.24.6.0"),sQuery(id+"F0.wireOp",EDGE,"E1.24.7.0"),sQuery(id+"F0.wireOp",EDGE,"E1.24.8.0"),sQuery(id+"F0.wireOp",EDGE,"E1.24.9.0"),sQuery(id+"F0.wireOp",EDGE,"E1.24.10.0"),sQuery(id+"F0.wireOp",EDGE,"E1.24.11.0"),sQuery(id+"F0.wireOp",EDGE,"E1.24.12.0"),sQuery(id+"F0.wireOp",EDGE,"E1.24.13.0"),sQuery(id+"F0.wireOp",EDGE,"E1.24.14.0"),sQuery(id+"F0.wireOp",EDGE,"E1.24.15.0"),sQuery(id+"F0.wireOp",EDGE,"E1.24.16.0"),sQuery(id+"F0.wireOp",EDGE,"E1.24.17.0"),sQuery(id+"F0.wireOp",EDGE,"E1.24.18.0"),sQuery(id+"F0.wireOp",EDGE,"E1.24.19.0"),sQuery(id+"F0.wireOp",EDGE,"E1.24.20.0"),sQuery(id+"F0.wireOp",EDGE,"E1.24.21.0"),sQuery(id+"F0.wireOp",EDGE,"E1.24.22.0"),sQuery(id+"F0.wireOp",EDGE,"E1.24.23.0"),sQuery(id+"F0.wireOp",EDGE,"E1.24.24.0"),sQuery(id+"F0.wireOp",EDGE,"E1.24.25.0"),sQuery(id+"F0.wireOp",EDGE,"E1.24.26.0"),sQuery(id+"F0.wireOp",EDGE,"E1.24.27.0"),sQuery(id+"F0.wireOp",EDGE,"E1.24.28.0"),sQuery(id+"F0.wireOp",EDGE,"E1.24.29.0"),sQuery(id+"F0.wireOp",EDGE,"E1.25.0.0"),sQuery(id+"F0.wireOp",EDGE,"E1.25.1.0"),sQuery(id+"F0.wireOp",EDGE,"E1.25.2.0"),sQuery(id+"F0.wireOp",EDGE,"E1.25.3.0"),sQuery(id+"F0.wireOp",EDGE,"E1.25.4.0"),sQuery(id+"F0.wireOp",EDGE,"E1.25.5.0"),sQuery(id+"F0.wireOp",EDGE,"E1.25.6.0"),sQuery(id+"F0.wireOp",EDGE,"E1.25.7.0"),sQuery(id+"F0.wireOp",EDGE,"E1.25.8.0"),sQuery(id+"F0.wireOp",EDGE,"E1.25.9.0"),sQuery(id+"F0.wireOp",EDGE,"E1.25.10.0"),sQuery(id+"F0.wireOp",EDGE,"E1.25.11.0"),sQuery(id+"F0.wireOp",EDGE,"E1.25.12.0"),sQuery(id+"F0.wireOp",EDGE,"E1.25.13.0"),sQuery(id+"F0.wireOp",EDGE,"E1.25.14.0"),sQuery(id+"F0.wireOp",EDGE,"E1.25.15.0"),sQuery(id+"F0.wireOp",EDGE,"E1.25.16.0"),sQuery(id+"F0.wireOp",EDGE,"E1.25.17.0"),sQuery(id+"F0.wireOp",EDGE,"E1.25.18.0"),sQuery(id+"F0.wireOp",EDGE,"E1.25.19.0"),sQuery(id+"F0.wireOp",EDGE,"E1.25.20.0"),sQuery(id+"F0.wireOp",EDGE,"E1.25.21.0"),sQuery(id+"F0.wireOp",EDGE,"E1.25.22.0"),sQuery(id+"F0.wireOp",EDGE,"E1.25.23.0"),sQuery(id+"F0.wireOp",EDGE,"E1.25.24.0"),sQuery(id+"F0.wireOp",EDGE,"E1.25.25.0"),sQuery(id+"F0.wireOp",EDGE,"E1.25.26.0"),sQuery(id+"F0.wireOp",EDGE,"E1.25.27.0"),sQuery(id+"F0.wireOp",EDGE,"E1.25.28.0"),sQuery(id+"F0.wireOp",EDGE,"E1.25.29.0"),sQuery(id+"F0.wireOp",EDGE,"E1.26.0.0"),sQuery(id+"F0.wireOp",EDGE,"E1.26.1.0"),sQuery(id+"F0.wireOp",EDGE,"E1.26.2.0"),sQuery(id+"F0.wireOp",EDGE,"E1.26.3.0"),sQuery(id+"F0.wireOp",EDGE,"E1.26.4.0"),sQuery(id+"F0.wireOp",EDGE,"E1.26.5.0"),sQuery(id+"F0.wireOp",EDGE,"E1.26.6.0"),sQuery(id+"F0.wireOp",EDGE,"E1.26.7.0"),sQuery(id+"F0.wireOp",EDGE,"E1.26.8.0"),sQuery(id+"F0.wireOp",EDGE,"E1.26.9.0"),sQuery(id+"F0.wireOp",EDGE,"E1.26.10.0"),sQuery(id+"F0.wireOp",EDGE,"E1.26.11.0"),sQuery(id+"F0.wireOp",EDGE,"E1.26.12.0"),sQuery(id+"F0.wireOp",EDGE,"E1.26.13.0"),sQuery(id+"F0.wireOp",EDGE,"E1.26.14.0"),sQuery(id+"F0.wireOp",EDGE,"E1.26.15.0"),sQuery(id+"F0.wireOp",EDGE,"E1.26.16.0"),sQuery(id+"F0.wireOp",EDGE,"E1.26.17.0"),sQuery(id+"F0.wireOp",EDGE,"E1.26.18.0"),sQuery(id+"F0.wireOp",EDGE,"E1.26.19.0"),sQuery(id+"F0.wireOp",EDGE,"E1.26.20.0"),sQuery(id+"F0.wireOp",EDGE,"E1.26.21.0"),sQuery(id+"F0.wireOp",EDGE,"E1.26.22.0"),sQuery(id+"F0.wireOp",EDGE,"E1.26.23.0"),sQuery(id+"F0.wireOp",EDGE,"E1.26.24.0"),sQuery(id+"F0.wireOp",EDGE,"E1.26.25.0"),sQuery(id+"F0.wireOp",EDGE,"E1.26.26.0"),sQuery(id+"F0.wireOp",EDGE,"E1.26.27.0"),sQuery(id+"F0.wireOp",EDGE,"E1.26.28.0"),sQuery(id+"F0.wireOp",EDGE,"E1.26.29.0"),sQuery(id+"F0.wireOp",EDGE,"E1.27.0.0"),sQuery(id+"F0.wireOp",EDGE,"E1.27.1.0"),sQuery(id+"F0.wireOp",EDGE,"E1.27.2.0"),sQuery(id+"F0.wireOp",EDGE,"E1.27.3.0"),sQuery(id+"F0.wireOp",EDGE,"E1.27.4.0"),sQuery(id+"F0.wireOp",EDGE,"E1.27.5.0"),sQuery(id+"F0.wireOp",EDGE,"E1.27.6.0"),sQuery(id+"F0.wireOp",EDGE,"E1.27.7.0"),sQuery(id+"F0.wireOp",EDGE,"E1.27.8.0"),sQuery(id+"F0.wireOp",EDGE,"E1.27.9.0"),sQuery(id+"F0.wireOp",EDGE,"E1.27.10.0"),sQuery(id+"F0.wireOp",EDGE,"E1.27.11.0"),sQuery(id+"F0.wireOp",EDGE,"E1.27.12.0"),sQuery(id+"F0.wireOp",EDGE,"E1.27.13.0"),sQuery(id+"F0.wireOp",EDGE,"E1.27.14.0"),sQuery(id+"F0.wireOp",EDGE,"E1.27.15.0"),sQuery(id+"F0.wireOp",EDGE,"E1.27.16.0"),sQuery(id+"F0.wireOp",EDGE,"E1.27.17.0"),sQuery(id+"F0.wireOp",EDGE,"E1.27.18.0"),sQuery(id+"F0.wireOp",EDGE,"E1.27.19.0"),sQuery(id+"F0.wireOp",EDGE,"E1.27.20.0"),sQuery(id+"F0.wireOp",EDGE,"E1.27.21.0"),sQuery(id+"F0.wireOp",EDGE,"E1.27.22.0"),sQuery(id+"F0.wireOp",EDGE,"E1.27.23.0"),sQuery(id+"F0.wireOp",EDGE,"E1.27.24.0"),sQuery(id+"F0.wireOp",EDGE,"E1.27.25.0"),sQuery(id+"F0.wireOp",EDGE,"E1.27.26.0"),sQuery(id+"F0.wireOp",EDGE,"E1.27.27.0"),sQuery(id+"F0.wireOp",EDGE,"E1.27.28.0"),sQuery(id+"F0.wireOp",EDGE,"E1.27.29.0"),sQuery(id+"F0.wireOp",EDGE,"E1.28.0.0"),sQuery(id+"F0.wireOp",EDGE,"E1.28.1.0"),sQuery(id+"F0.wireOp",EDGE,"E1.28.2.0"),sQuery(id+"F0.wireOp",EDGE,"E1.28.3.0"),sQuery(id+"F0.wireOp",EDGE,"E1.28.4.0"),sQuery(id+"F0.wireOp",EDGE,"E1.28.5.0"),sQuery(id+"F0.wireOp",EDGE,"E1.28.6.0"),sQuery(id+"F0.wireOp",EDGE,"E1.28.7.0"),sQuery(id+"F0.wireOp",EDGE,"E1.28.8.0"),sQuery(id+"F0.wireOp",EDGE,"E1.28.9.0"),sQuery(id+"F0.wireOp",EDGE,"E1.28.10.0"),sQuery(id+"F0.wireOp",EDGE,"E1.28.11.0"),sQuery(id+"F0.wireOp",EDGE,"E1.28.12.0"),sQuery(id+"F0.wireOp",EDGE,"E1.28.13.0"),sQuery(id+"F0.wireOp",EDGE,"E1.28.14.0"),sQuery(id+"F0.wireOp",EDGE,"E1.28.15.0"),sQuery(id+"F0.wireOp",EDGE,"E1.28.16.0"),sQuery(id+"F0.wireOp",EDGE,"E1.28.17.0"),sQuery(id+"F0.wireOp",EDGE,"E1.28.18.0"),sQuery(id+"F0.wireOp",EDGE,"E1.28.19.0"),sQuery(id+"F0.wireOp",EDGE,"E1.28.20.0"),sQuery(id+"F0.wireOp",EDGE,"E1.28.21.0"),sQuery(id+"F0.wireOp",EDGE,"E1.28.22.0"),sQuery(id+"F0.wireOp",EDGE,"E1.28.23.0"),sQuery(id+"F0.wireOp",EDGE,"E1.28.24.0"),sQuery(id+"F0.wireOp",EDGE,"E1.28.25.0"),sQuery(id+"F0.wireOp",EDGE,"E1.28.26.0"),sQuery(id+"F0.wireOp",EDGE,"E1.28.27.0"),sQuery(id+"F0.wireOp",EDGE,"E1.28.28.0"),sQuery(id+"F0.wireOp",EDGE,"E1.28.29.0"),sQuery(id+"F0.wireOp",EDGE,"E1.29.0.0"),sQuery(id+"F0.wireOp",EDGE,"E1.29.1.0"),sQuery(id+"F0.wireOp",EDGE,"E1.29.2.0"),sQuery(id+"F0.wireOp",EDGE,"E1.29.3.0"),sQuery(id+"F0.wireOp",EDGE,"E1.29.4.0"),sQuery(id+"F0.wireOp",EDGE,"E1.29.5.0"),sQuery(id+"F0.wireOp",EDGE,"E1.29.6.0"),sQuery(id+"F0.wireOp",EDGE,"E1.29.7.0"),sQuery(id+"F0.wireOp",EDGE,"E1.29.8.0"),sQuery(id+"F0.wireOp",EDGE,"E1.29.9.0"),sQuery(id+"F0.wireOp",EDGE,"E1.29.10.0"),sQuery(id+"F0.wireOp",EDGE,"E1.29.11.0"),sQuery(id+"F0.wireOp",EDGE,"E1.29.12.0"),sQuery(id+"F0.wireOp",EDGE,"E1.29.13.0"),sQuery(id+"F0.wireOp",EDGE,"E1.29.14.0"),sQuery(id+"F0.wireOp",EDGE,"E1.29.15.0"),sQuery(id+"F0.wireOp",EDGE,"E1.29.16.0"),sQuery(id+"F0.wireOp",EDGE,"E1.29.17.0"),sQuery(id+"F0.wireOp",EDGE,"E1.29.18.0"),sQuery(id+"F0.wireOp",EDGE,"E1.29.19.0"),sQuery(id+"F0.wireOp",EDGE,"E1.29.20.0"),sQuery(id+"F0.wireOp",EDGE,"E1.29.21.0"),sQuery(id+"F0.wireOp",EDGE,"E1.29.22.0"),sQuery(id+"F0.wireOp",EDGE,"E1.29.23.0"),sQuery(id+"F0.wireOp",EDGE,"E1.29.24.0"),sQuery(id+"F0.wireOp",EDGE,"E1.29.25.0"),sQuery(id+"F0.wireOp",EDGE,"E1.29.26.0"),sQuery(id+"F0.wireOp",EDGE,"E1.29.27.0"),sQuery(id+"F0.wireOp",EDGE,"E1.29.28.0"),sQuery(id+"F0.wireOp",EDGE,"E1.29.29.0"),sQuery(id+"F0.wireOp",EDGE,"E2.bottom"),sQuery(id+"F0.wireOp",EDGE,"E2.top"),sQuery(id+"F0.wireOp",EDGE,"E2.left"),sQuery(id+"F0.wireOp",EDGE,"E2.right")])],"isStart":false});
            var sketch = newSketch(context, id + "F2", { "sketchPlane" : qUnion([Q0])});
            skLineSegment(sketch, "E3.bottom", {"start": v(-5.5, 150.5) * mm, "end": v(150.5, 150.5) * mm});
            skLineSegment(sketch, "E3.top", {"start": v(-5.5, -5.5) * mm, "end": v(150.5, -5.5) * mm});
            skLineSegment(sketch, "E3.left", {"start": v(-5.5, 150.5) * mm, "end": v(-5.5, -5.5) * mm});
            skLineSegment(sketch, "E3.right", {"start": v(150.5, 150.5) * mm, "end": v(150.5, -5.5) * mm});
            skLineSegment(sketch, "E4.0", {"start": v(149, 149) * mm, "end": v(149, -4) * mm});
            skLineSegment(sketch, "E5.1", {"start": v(-4, 149) * mm, "end": v(149, 149) * mm});
            skLineSegment(sketch, "E6.0", {"start": v(-4, 149) * mm, "end": v(-4, -4) * mm});
            skSolve(sketch);
        }
        {
            var Q0;
            Q0=makeQuery(id+"F2.imprint","IMPRINT",FACE,{"disambiguationData":[TD([[makeQuery(id+"F2.imprint","IMPRINT",EDGE,{"derivedFrom":sQuery(id+"F2.wireOp",EDGE,"E3.bottom")}),-1.0]])]});
            var Q1;
            Q1=makeQuery(id+"F1.opExtrude","CAP_FACE",FACE,{"disambiguationData":[OSD([sQuery(id+"F0.wireOp",EDGE,"E0"),sQuery(id+"F0.wireOp",EDGE,"E1.0.1.0"),sQuery(id+"F0.wireOp",EDGE,"E1.0.2.0"),sQuery(id+"F0.wireOp",EDGE,"E1.0.3.0"),sQuery(id+"F0.wireOp",EDGE,"E1.0.4.0"),sQuery(id+"F0.wireOp",EDGE,"E1.0.5.0"),sQuery(id+"F0.wireOp",EDGE,"E1.0.6.0"),sQuery(id+"F0.wireOp",EDGE,"E1.0.7.0"),sQuery(id+"F0.wireOp",EDGE,"E1.0.8.0"),sQuery(id+"F0.wireOp",EDGE,"E1.0.9.0"),sQuery(id+"F0.wireOp",EDGE,"E1.0.10.0"),sQuery(id+"F0.wireOp",EDGE,"E1.0.11.0"),sQuery(id+"F0.wireOp",EDGE,"E1.0.12.0"),sQuery(id+"F0.wireOp",EDGE,"E1.0.13.0"),sQuery(id+"F0.wireOp",EDGE,"E1.0.14.0"),sQuery(id+"F0.wireOp",EDGE,"E1.0.15.0"),sQuery(id+"F0.wireOp",EDGE,"E1.0.16.0"),sQuery(id+"F0.wireOp",EDGE,"E1.0.17.0"),sQuery(id+"F0.wireOp",EDGE,"E1.0.18.0"),sQuery(id+"F0.wireOp",EDGE,"E1.0.19.0"),sQuery(id+"F0.wireOp",EDGE,"E1.0.20.0"),sQuery(id+"F0.wireOp",EDGE,"E1.0.21.0"),sQuery(id+"F0.wireOp",EDGE,"E1.0.22.0"),sQuery(id+"F0.wireOp",EDGE,"E1.0.23.0"),sQuery(id+"F0.wireOp",EDGE,"E1.0.24.0"),sQuery(id+"F0.wireOp",EDGE,"E1.0.25.0"),sQuery(id+"F0.wireOp",EDGE,"E1.0.26.0"),sQuery(id+"F0.wireOp",EDGE,"E1.0.27.0"),sQuery(id+"F0.wireOp",EDGE,"E1.0.28.0"),sQuery(id+"F0.wireOp",EDGE,"E1.0.29.0"),sQuery(id+"F0.wireOp",EDGE,"E1.1.0.0"),sQuery(id+"F0.wireOp",EDGE,"E1.1.1.0"),sQuery(id+"F0.wireOp",EDGE,"E1.1.2.0"),sQuery(id+"F0.wireOp",EDGE,"E1.1.3.0"),sQuery(id+"F0.wireOp",EDGE,"E1.1.4.0"),sQuery(id+"F0.wireOp",EDGE,"E1.1.5.0"),sQuery(id+"F0.wireOp",EDGE,"E1.1.6.0"),sQuery(id+"F0.wireOp",EDGE,"E1.1.7.0"),sQuery(id+"F0.wireOp",EDGE,"E1.1.8.0"),sQuery(id+"F0.wireOp",EDGE,"E1.1.9.0"),sQuery(id+"F0.wireOp",EDGE,"E1.1.10.0"),sQuery(id+"F0.wireOp",EDGE,"E1.1.11.0"),sQuery(id+"F0.wireOp",EDGE,"E1.1.12.0"),sQuery(id+"F0.wireOp",EDGE,"E1.1.13.0"),sQuery(id+"F0.wireOp",EDGE,"E1.1.14.0"),sQuery(id+"F0.wireOp",EDGE,"E1.1.15.0"),sQuery(id+"F0.wireOp",EDGE,"E1.1.16.0"),sQuery(id+"F0.wireOp",EDGE,"E1.1.17.0"),sQuery(id+"F0.wireOp",EDGE,"E1.1.18.0"),sQuery(id+"F0.wireOp",EDGE,"E1.1.19.0"),sQuery(id+"F0.wireOp",EDGE,"E1.1.20.0"),sQuery(id+"F0.wireOp",EDGE,"E1.1.21.0"),sQuery(id+"F0.wireOp",EDGE,"E1.1.22.0"),sQuery(id+"F0.wireOp",EDGE,"E1.1.23.0"),sQuery(id+"F0.wireOp",EDGE,"E1.1.24.0"),sQuery(id+"F0.wireOp",EDGE,"E1.1.25.0"),sQuery(id+"F0.wireOp",EDGE,"E1.1.26.0"),sQuery(id+"F0.wireOp",EDGE,"E1.1.27.0"),sQuery(id+"F0.wireOp",EDGE,"E1.1.28.0"),sQuery(id+"F0.wireOp",EDGE,"E1.1.29.0"),sQuery(id+"F0.wireOp",EDGE,"E1.2.0.0"),sQuery(id+"F0.wireOp",EDGE,"E1.2.1.0"),sQuery(id+"F0.wireOp",EDGE,"E1.2.2.0"),sQuery(id+"F0.wireOp",EDGE,"E1.2.3.0"),sQuery(id+"F0.wireOp",EDGE,"E1.2.4.0"),sQuery(id+"F0.wireOp",EDGE,"E1.2.5.0"),sQuery(id+"F0.wireOp",EDGE,"E1.2.6.0"),sQuery(id+"F0.wireOp",EDGE,"E1.2.7.0"),sQuery(id+"F0.wireOp",EDGE,"E1.2.8.0"),sQuery(id+"F0.wireOp",EDGE,"E1.2.9.0"),sQuery(id+"F0.wireOp",EDGE,"E1.2.10.0"),sQuery(id+"F0.wireOp",EDGE,"E1.2.11.0"),sQuery(id+"F0.wireOp",EDGE,"E1.2.12.0"),sQuery(id+"F0.wireOp",EDGE,"E1.2.13.0"),sQuery(id+"F0.wireOp",EDGE,"E1.2.14.0"),sQuery(id+"F0.wireOp",EDGE,"E1.2.15.0"),sQuery(id+"F0.wireOp",EDGE,"E1.2.16.0"),sQuery(id+"F0.wireOp",EDGE,"E1.2.17.0"),sQuery(id+"F0.wireOp",EDGE,"E1.2.18.0"),sQuery(id+"F0.wireOp",EDGE,"E1.2.19.0"),sQuery(id+"F0.wireOp",EDGE,"E1.2.20.0"),sQuery(id+"F0.wireOp",EDGE,"E1.2.21.0"),sQuery(id+"F0.wireOp",EDGE,"E1.2.22.0"),sQuery(id+"F0.wireOp",EDGE,"E1.2.23.0"),sQuery(id+"F0.wireOp",EDGE,"E1.2.24.0"),sQuery(id+"F0.wireOp",EDGE,"E1.2.25.0"),sQuery(id+"F0.wireOp",EDGE,"E1.2.26.0"),sQuery(id+"F0.wireOp",EDGE,"E1.2.27.0"),sQuery(id+"F0.wireOp",EDGE,"E1.2.28.0"),sQuery(id+"F0.wireOp",EDGE,"E1.2.29.0"),sQuery(id+"F0.wireOp",EDGE,"E1.3.0.0"),sQuery(id+"F0.wireOp",EDGE,"E1.3.1.0"),sQuery(id+"F0.wireOp",EDGE,"E1.3.2.0"),sQuery(id+"F0.wireOp",EDGE,"E1.3.3.0"),sQuery(id+"F0.wireOp",EDGE,"E1.3.4.0"),sQuery(id+"F0.wireOp",EDGE,"E1.3.5.0"),sQuery(id+"F0.wireOp",EDGE,"E1.3.6.0"),sQuery(id+"F0.wireOp",EDGE,"E1.3.7.0"),sQuery(id+"F0.wireOp",EDGE,"E1.3.8.0"),sQuery(id+"F0.wireOp",EDGE,"E1.3.9.0"),sQuery(id+"F0.wireOp",EDGE,"E1.3.10.0"),sQuery(id+"F0.wireOp",EDGE,"E1.3.11.0"),sQuery(id+"F0.wireOp",EDGE,"E1.3.12.0"),sQuery(id+"F0.wireOp",EDGE,"E1.3.13.0"),sQuery(id+"F0.wireOp",EDGE,"E1.3.14.0"),sQuery(id+"F0.wireOp",EDGE,"E1.3.15.0"),sQuery(id+"F0.wireOp",EDGE,"E1.3.16.0"),sQuery(id+"F0.wireOp",EDGE,"E1.3.17.0"),sQuery(id+"F0.wireOp",EDGE,"E1.3.18.0"),sQuery(id+"F0.wireOp",EDGE,"E1.3.19.0"),sQuery(id+"F0.wireOp",EDGE,"E1.3.20.0"),sQuery(id+"F0.wireOp",EDGE,"E1.3.21.0"),sQuery(id+"F0.wireOp",EDGE,"E1.3.22.0"),sQuery(id+"F0.wireOp",EDGE,"E1.3.23.0"),sQuery(id+"F0.wireOp",EDGE,"E1.3.24.0"),sQuery(id+"F0.wireOp",EDGE,"E1.3.25.0"),sQuery(id+"F0.wireOp",EDGE,"E1.3.26.0"),sQuery(id+"F0.wireOp",EDGE,"E1.3.27.0"),sQuery(id+"F0.wireOp",EDGE,"E1.3.28.0"),sQuery(id+"F0.wireOp",EDGE,"E1.3.29.0"),sQuery(id+"F0.wireOp",EDGE,"E1.4.0.0"),sQuery(id+"F0.wireOp",EDGE,"E1.4.1.0"),sQuery(id+"F0.wireOp",EDGE,"E1.4.2.0"),sQuery(id+"F0.wireOp",EDGE,"E1.4.3.0"),sQuery(id+"F0.wireOp",EDGE,"E1.4.4.0"),sQuery(id+"F0.wireOp",EDGE,"E1.4.5.0"),sQuery(id+"F0.wireOp",EDGE,"E1.4.6.0"),sQuery(id+"F0.wireOp",EDGE,"E1.4.7.0"),sQuery(id+"F0.wireOp",EDGE,"E1.4.8.0"),sQuery(id+"F0.wireOp",EDGE,"E1.4.9.0"),sQuery(id+"F0.wireOp",EDGE,"E1.4.10.0"),sQuery(id+"F0.wireOp",EDGE,"E1.4.11.0"),sQuery(id+"F0.wireOp",EDGE,"E1.4.12.0"),sQuery(id+"F0.wireOp",EDGE,"E1.4.13.0"),sQuery(id+"F0.wireOp",EDGE,"E1.4.14.0"),sQuery(id+"F0.wireOp",EDGE,"E1.4.15.0"),sQuery(id+"F0.wireOp",EDGE,"E1.4.16.0"),sQuery(id+"F0.wireOp",EDGE,"E1.4.17.0"),sQuery(id+"F0.wireOp",EDGE,"E1.4.18.0"),sQuery(id+"F0.wireOp",EDGE,"E1.4.19.0"),sQuery(id+"F0.wireOp",EDGE,"E1.4.20.0"),sQuery(id+"F0.wireOp",EDGE,"E1.4.21.0"),sQuery(id+"F0.wireOp",EDGE,"E1.4.22.0"),sQuery(id+"F0.wireOp",EDGE,"E1.4.23.0"),sQuery(id+"F0.wireOp",EDGE,"E1.4.24.0"),sQuery(id+"F0.wireOp",EDGE,"E1.4.25.0"),sQuery(id+"F0.wireOp",EDGE,"E1.4.26.0"),sQuery(id+"F0.wireOp",EDGE,"E1.4.27.0"),sQuery(id+"F0.wireOp",EDGE,"E1.4.28.0"),sQuery(id+"F0.wireOp",EDGE,"E1.4.29.0"),sQuery(id+"F0.wireOp",EDGE,"E1.5.0.0"),sQuery(id+"F0.wireOp",EDGE,"E1.5.1.0"),sQuery(id+"F0.wireOp",EDGE,"E1.5.2.0"),sQuery(id+"F0.wireOp",EDGE,"E1.5.3.0"),sQuery(id+"F0.wireOp",EDGE,"E1.5.4.0"),sQuery(id+"F0.wireOp",EDGE,"E1.5.5.0"),sQuery(id+"F0.wireOp",EDGE,"E1.5.6.0"),sQuery(id+"F0.wireOp",EDGE,"E1.5.7.0"),sQuery(id+"F0.wireOp",EDGE,"E1.5.8.0"),sQuery(id+"F0.wireOp",EDGE,"E1.5.9.0"),sQuery(id+"F0.wireOp",EDGE,"E1.5.10.0"),sQuery(id+"F0.wireOp",EDGE,"E1.5.11.0"),sQuery(id+"F0.wireOp",EDGE,"E1.5.12.0"),sQuery(id+"F0.wireOp",EDGE,"E1.5.13.0"),sQuery(id+"F0.wireOp",EDGE,"E1.5.14.0"),sQuery(id+"F0.wireOp",EDGE,"E1.5.15.0"),sQuery(id+"F0.wireOp",EDGE,"E1.5.16.0"),sQuery(id+"F0.wireOp",EDGE,"E1.5.17.0"),sQuery(id+"F0.wireOp",EDGE,"E1.5.18.0"),sQuery(id+"F0.wireOp",EDGE,"E1.5.19.0"),sQuery(id+"F0.wireOp",EDGE,"E1.5.20.0"),sQuery(id+"F0.wireOp",EDGE,"E1.5.21.0"),sQuery(id+"F0.wireOp",EDGE,"E1.5.22.0"),sQuery(id+"F0.wireOp",EDGE,"E1.5.23.0"),sQuery(id+"F0.wireOp",EDGE,"E1.5.24.0"),sQuery(id+"F0.wireOp",EDGE,"E1.5.25.0"),sQuery(id+"F0.wireOp",EDGE,"E1.5.26.0"),sQuery(id+"F0.wireOp",EDGE,"E1.5.27.0"),sQuery(id+"F0.wireOp",EDGE,"E1.5.28.0"),sQuery(id+"F0.wireOp",EDGE,"E1.5.29.0"),sQuery(id+"F0.wireOp",EDGE,"E1.6.0.0"),sQuery(id+"F0.wireOp",EDGE,"E1.6.1.0"),sQuery(id+"F0.wireOp",EDGE,"E1.6.2.0"),sQuery(id+"F0.wireOp",EDGE,"E1.6.3.0"),sQuery(id+"F0.wireOp",EDGE,"E1.6.4.0"),sQuery(id+"F0.wireOp",EDGE,"E1.6.5.0"),sQuery(id+"F0.wireOp",EDGE,"E1.6.6.0"),sQuery(id+"F0.wireOp",EDGE,"E1.6.7.0"),sQuery(id+"F0.wireOp",EDGE,"E1.6.8.0"),sQuery(id+"F0.wireOp",EDGE,"E1.6.9.0"),sQuery(id+"F0.wireOp",EDGE,"E1.6.10.0"),sQuery(id+"F0.wireOp",EDGE,"E1.6.11.0"),sQuery(id+"F0.wireOp",EDGE,"E1.6.12.0"),sQuery(id+"F0.wireOp",EDGE,"E1.6.13.0"),sQuery(id+"F0.wireOp",EDGE,"E1.6.14.0"),sQuery(id+"F0.wireOp",EDGE,"E1.6.15.0"),sQuery(id+"F0.wireOp",EDGE,"E1.6.16.0"),sQuery(id+"F0.wireOp",EDGE,"E1.6.17.0"),sQuery(id+"F0.wireOp",EDGE,"E1.6.18.0"),sQuery(id+"F0.wireOp",EDGE,"E1.6.19.0"),sQuery(id+"F0.wireOp",EDGE,"E1.6.20.0"),sQuery(id+"F0.wireOp",EDGE,"E1.6.21.0"),sQuery(id+"F0.wireOp",EDGE,"E1.6.22.0"),sQuery(id+"F0.wireOp",EDGE,"E1.6.23.0"),sQuery(id+"F0.wireOp",EDGE,"E1.6.24.0"),sQuery(id+"F0.wireOp",EDGE,"E1.6.25.0"),sQuery(id+"F0.wireOp",EDGE,"E1.6.26.0"),sQuery(id+"F0.wireOp",EDGE,"E1.6.27.0"),sQuery(id+"F0.wireOp",EDGE,"E1.6.28.0"),sQuery(id+"F0.wireOp",EDGE,"E1.6.29.0"),sQuery(id+"F0.wireOp",EDGE,"E1.7.0.0"),sQuery(id+"F0.wireOp",EDGE,"E1.7.1.0"),sQuery(id+"F0.wireOp",EDGE,"E1.7.2.0"),sQuery(id+"F0.wireOp",EDGE,"E1.7.3.0"),sQuery(id+"F0.wireOp",EDGE,"E1.7.4.0"),sQuery(id+"F0.wireOp",EDGE,"E1.7.5.0"),sQuery(id+"F0.wireOp",EDGE,"E1.7.6.0"),sQuery(id+"F0.wireOp",EDGE,"E1.7.7.0"),sQuery(id+"F0.wireOp",EDGE,"E1.7.8.0"),sQuery(id+"F0.wireOp",EDGE,"E1.7.9.0"),sQuery(id+"F0.wireOp",EDGE,"E1.7.10.0"),sQuery(id+"F0.wireOp",EDGE,"E1.7.11.0"),sQuery(id+"F0.wireOp",EDGE,"E1.7.12.0"),sQuery(id+"F0.wireOp",EDGE,"E1.7.13.0"),sQuery(id+"F0.wireOp",EDGE,"E1.7.14.0"),sQuery(id+"F0.wireOp",EDGE,"E1.7.15.0"),sQuery(id+"F0.wireOp",EDGE,"E1.7.16.0"),sQuery(id+"F0.wireOp",EDGE,"E1.7.17.0"),sQuery(id+"F0.wireOp",EDGE,"E1.7.18.0"),sQuery(id+"F0.wireOp",EDGE,"E1.7.19.0"),sQuery(id+"F0.wireOp",EDGE,"E1.7.20.0"),sQuery(id+"F0.wireOp",EDGE,"E1.7.21.0"),sQuery(id+"F0.wireOp",EDGE,"E1.7.22.0"),sQuery(id+"F0.wireOp",EDGE,"E1.7.23.0"),sQuery(id+"F0.wireOp",EDGE,"E1.7.24.0"),sQuery(id+"F0.wireOp",EDGE,"E1.7.25.0"),sQuery(id+"F0.wireOp",EDGE,"E1.7.26.0"),sQuery(id+"F0.wireOp",EDGE,"E1.7.27.0"),sQuery(id+"F0.wireOp",EDGE,"E1.7.28.0"),sQuery(id+"F0.wireOp",EDGE,"E1.7.29.0"),sQuery(id+"F0.wireOp",EDGE,"E1.8.0.0"),sQuery(id+"F0.wireOp",EDGE,"E1.8.1.0"),sQuery(id+"F0.wireOp",EDGE,"E1.8.2.0"),sQuery(id+"F0.wireOp",EDGE,"E1.8.3.0"),sQuery(id+"F0.wireOp",EDGE,"E1.8.4.0"),sQuery(id+"F0.wireOp",EDGE,"E1.8.5.0"),sQuery(id+"F0.wireOp",EDGE,"E1.8.6.0"),sQuery(id+"F0.wireOp",EDGE,"E1.8.7.0"),sQuery(id+"F0.wireOp",EDGE,"E1.8.8.0"),sQuery(id+"F0.wireOp",EDGE,"E1.8.9.0"),sQuery(id+"F0.wireOp",EDGE,"E1.8.10.0"),sQuery(id+"F0.wireOp",EDGE,"E1.8.11.0"),sQuery(id+"F0.wireOp",EDGE,"E1.8.12.0"),sQuery(id+"F0.wireOp",EDGE,"E1.8.13.0"),sQuery(id+"F0.wireOp",EDGE,"E1.8.14.0"),sQuery(id+"F0.wireOp",EDGE,"E1.8.15.0"),sQuery(id+"F0.wireOp",EDGE,"E1.8.16.0"),sQuery(id+"F0.wireOp",EDGE,"E1.8.17.0"),sQuery(id+"F0.wireOp",EDGE,"E1.8.18.0"),sQuery(id+"F0.wireOp",EDGE,"E1.8.19.0"),sQuery(id+"F0.wireOp",EDGE,"E1.8.20.0"),sQuery(id+"F0.wireOp",EDGE,"E1.8.21.0"),sQuery(id+"F0.wireOp",EDGE,"E1.8.22.0"),sQuery(id+"F0.wireOp",EDGE,"E1.8.23.0"),sQuery(id+"F0.wireOp",EDGE,"E1.8.24.0"),sQuery(id+"F0.wireOp",EDGE,"E1.8.25.0"),sQuery(id+"F0.wireOp",EDGE,"E1.8.26.0"),sQuery(id+"F0.wireOp",EDGE,"E1.8.27.0"),sQuery(id+"F0.wireOp",EDGE,"E1.8.28.0"),sQuery(id+"F0.wireOp",EDGE,"E1.8.29.0"),sQuery(id+"F0.wireOp",EDGE,"E1.9.0.0"),sQuery(id+"F0.wireOp",EDGE,"E1.9.1.0"),sQuery(id+"F0.wireOp",EDGE,"E1.9.2.0"),sQuery(id+"F0.wireOp",EDGE,"E1.9.3.0"),sQuery(id+"F0.wireOp",EDGE,"E1.9.4.0"),sQuery(id+"F0.wireOp",EDGE,"E1.9.5.0"),sQuery(id+"F0.wireOp",EDGE,"E1.9.6.0"),sQuery(id+"F0.wireOp",EDGE,"E1.9.7.0"),sQuery(id+"F0.wireOp",EDGE,"E1.9.8.0"),sQuery(id+"F0.wireOp",EDGE,"E1.9.9.0"),sQuery(id+"F0.wireOp",EDGE,"E1.9.10.0"),sQuery(id+"F0.wireOp",EDGE,"E1.9.11.0"),sQuery(id+"F0.wireOp",EDGE,"E1.9.12.0"),sQuery(id+"F0.wireOp",EDGE,"E1.9.13.0"),sQuery(id+"F0.wireOp",EDGE,"E1.9.14.0"),sQuery(id+"F0.wireOp",EDGE,"E1.9.15.0"),sQuery(id+"F0.wireOp",EDGE,"E1.9.16.0"),sQuery(id+"F0.wireOp",EDGE,"E1.9.17.0"),sQuery(id+"F0.wireOp",EDGE,"E1.9.18.0"),sQuery(id+"F0.wireOp",EDGE,"E1.9.19.0"),sQuery(id+"F0.wireOp",EDGE,"E1.9.20.0"),sQuery(id+"F0.wireOp",EDGE,"E1.9.21.0"),sQuery(id+"F0.wireOp",EDGE,"E1.9.22.0"),sQuery(id+"F0.wireOp",EDGE,"E1.9.23.0"),sQuery(id+"F0.wireOp",EDGE,"E1.9.24.0"),sQuery(id+"F0.wireOp",EDGE,"E1.9.25.0"),sQuery(id+"F0.wireOp",EDGE,"E1.9.26.0"),sQuery(id+"F0.wireOp",EDGE,"E1.9.27.0"),sQuery(id+"F0.wireOp",EDGE,"E1.9.28.0"),sQuery(id+"F0.wireOp",EDGE,"E1.9.29.0"),sQuery(id+"F0.wireOp",EDGE,"E1.10.0.0"),sQuery(id+"F0.wireOp",EDGE,"E1.10.1.0"),sQuery(id+"F0.wireOp",EDGE,"E1.10.2.0"),sQuery(id+"F0.wireOp",EDGE,"E1.10.3.0"),sQuery(id+"F0.wireOp",EDGE,"E1.10.4.0"),sQuery(id+"F0.wireOp",EDGE,"E1.10.5.0"),sQuery(id+"F0.wireOp",EDGE,"E1.10.6.0"),sQuery(id+"F0.wireOp",EDGE,"E1.10.7.0"),sQuery(id+"F0.wireOp",EDGE,"E1.10.8.0"),sQuery(id+"F0.wireOp",EDGE,"E1.10.9.0"),sQuery(id+"F0.wireOp",EDGE,"E1.10.10.0"),sQuery(id+"F0.wireOp",EDGE,"E1.10.11.0"),sQuery(id+"F0.wireOp",EDGE,"E1.10.12.0"),sQuery(id+"F0.wireOp",EDGE,"E1.10.13.0"),sQuery(id+"F0.wireOp",EDGE,"E1.10.14.0"),sQuery(id+"F0.wireOp",EDGE,"E1.10.15.0"),sQuery(id+"F0.wireOp",EDGE,"E1.10.16.0"),sQuery(id+"F0.wireOp",EDGE,"E1.10.17.0"),sQuery(id+"F0.wireOp",EDGE,"E1.10.18.0"),sQuery(id+"F0.wireOp",EDGE,"E1.10.19.0"),sQuery(id+"F0.wireOp",EDGE,"E1.10.20.0"),sQuery(id+"F0.wireOp",EDGE,"E1.10.21.0"),sQuery(id+"F0.wireOp",EDGE,"E1.10.22.0"),sQuery(id+"F0.wireOp",EDGE,"E1.10.23.0"),sQuery(id+"F0.wireOp",EDGE,"E1.10.24.0"),sQuery(id+"F0.wireOp",EDGE,"E1.10.25.0"),sQuery(id+"F0.wireOp",EDGE,"E1.10.26.0"),sQuery(id+"F0.wireOp",EDGE,"E1.10.27.0"),sQuery(id+"F0.wireOp",EDGE,"E1.10.28.0"),sQuery(id+"F0.wireOp",EDGE,"E1.10.29.0"),sQuery(id+"F0.wireOp",EDGE,"E1.11.0.0"),sQuery(id+"F0.wireOp",EDGE,"E1.11.1.0"),sQuery(id+"F0.wireOp",EDGE,"E1.11.2.0"),sQuery(id+"F0.wireOp",EDGE,"E1.11.3.0"),sQuery(id+"F0.wireOp",EDGE,"E1.11.4.0"),sQuery(id+"F0.wireOp",EDGE,"E1.11.5.0"),sQuery(id+"F0.wireOp",EDGE,"E1.11.6.0"),sQuery(id+"F0.wireOp",EDGE,"E1.11.7.0"),sQuery(id+"F0.wireOp",EDGE,"E1.11.8.0"),sQuery(id+"F0.wireOp",EDGE,"E1.11.9.0"),sQuery(id+"F0.wireOp",EDGE,"E1.11.10.0"),sQuery(id+"F0.wireOp",EDGE,"E1.11.11.0"),sQuery(id+"F0.wireOp",EDGE,"E1.11.12.0"),sQuery(id+"F0.wireOp",EDGE,"E1.11.13.0"),sQuery(id+"F0.wireOp",EDGE,"E1.11.14.0"),sQuery(id+"F0.wireOp",EDGE,"E1.11.15.0"),sQuery(id+"F0.wireOp",EDGE,"E1.11.16.0"),sQuery(id+"F0.wireOp",EDGE,"E1.11.17.0"),sQuery(id+"F0.wireOp",EDGE,"E1.11.18.0"),sQuery(id+"F0.wireOp",EDGE,"E1.11.19.0"),sQuery(id+"F0.wireOp",EDGE,"E1.11.20.0"),sQuery(id+"F0.wireOp",EDGE,"E1.11.21.0"),sQuery(id+"F0.wireOp",EDGE,"E1.11.22.0"),sQuery(id+"F0.wireOp",EDGE,"E1.11.23.0"),sQuery(id+"F0.wireOp",EDGE,"E1.11.24.0"),sQuery(id+"F0.wireOp",EDGE,"E1.11.25.0"),sQuery(id+"F0.wireOp",EDGE,"E1.11.26.0"),sQuery(id+"F0.wireOp",EDGE,"E1.11.27.0"),sQuery(id+"F0.wireOp",EDGE,"E1.11.28.0"),sQuery(id+"F0.wireOp",EDGE,"E1.11.29.0"),sQuery(id+"F0.wireOp",EDGE,"E1.12.0.0"),sQuery(id+"F0.wireOp",EDGE,"E1.12.1.0"),sQuery(id+"F0.wireOp",EDGE,"E1.12.2.0"),sQuery(id+"F0.wireOp",EDGE,"E1.12.3.0"),sQuery(id+"F0.wireOp",EDGE,"E1.12.4.0"),sQuery(id+"F0.wireOp",EDGE,"E1.12.5.0"),sQuery(id+"F0.wireOp",EDGE,"E1.12.6.0"),sQuery(id+"F0.wireOp",EDGE,"E1.12.7.0"),sQuery(id+"F0.wireOp",EDGE,"E1.12.8.0"),sQuery(id+"F0.wireOp",EDGE,"E1.12.9.0"),sQuery(id+"F0.wireOp",EDGE,"E1.12.10.0"),sQuery(id+"F0.wireOp",EDGE,"E1.12.11.0"),sQuery(id+"F0.wireOp",EDGE,"E1.12.12.0"),sQuery(id+"F0.wireOp",EDGE,"E1.12.13.0"),sQuery(id+"F0.wireOp",EDGE,"E1.12.14.0"),sQuery(id+"F0.wireOp",EDGE,"E1.12.15.0"),sQuery(id+"F0.wireOp",EDGE,"E1.12.16.0"),sQuery(id+"F0.wireOp",EDGE,"E1.12.17.0"),sQuery(id+"F0.wireOp",EDGE,"E1.12.18.0"),sQuery(id+"F0.wireOp",EDGE,"E1.12.19.0"),sQuery(id+"F0.wireOp",EDGE,"E1.12.20.0"),sQuery(id+"F0.wireOp",EDGE,"E1.12.21.0"),sQuery(id+"F0.wireOp",EDGE,"E1.12.22.0"),sQuery(id+"F0.wireOp",EDGE,"E1.12.23.0"),sQuery(id+"F0.wireOp",EDGE,"E1.12.24.0"),sQuery(id+"F0.wireOp",EDGE,"E1.12.25.0"),sQuery(id+"F0.wireOp",EDGE,"E1.12.26.0"),sQuery(id+"F0.wireOp",EDGE,"E1.12.27.0"),sQuery(id+"F0.wireOp",EDGE,"E1.12.28.0"),sQuery(id+"F0.wireOp",EDGE,"E1.12.29.0"),sQuery(id+"F0.wireOp",EDGE,"E1.13.0.0"),sQuery(id+"F0.wireOp",EDGE,"E1.13.1.0"),sQuery(id+"F0.wireOp",EDGE,"E1.13.2.0"),sQuery(id+"F0.wireOp",EDGE,"E1.13.3.0"),sQuery(id+"F0.wireOp",EDGE,"E1.13.4.0"),sQuery(id+"F0.wireOp",EDGE,"E1.13.5.0"),sQuery(id+"F0.wireOp",EDGE,"E1.13.6.0"),sQuery(id+"F0.wireOp",EDGE,"E1.13.7.0"),sQuery(id+"F0.wireOp",EDGE,"E1.13.8.0"),sQuery(id+"F0.wireOp",EDGE,"E1.13.9.0"),sQuery(id+"F0.wireOp",EDGE,"E1.13.10.0"),sQuery(id+"F0.wireOp",EDGE,"E1.13.11.0"),sQuery(id+"F0.wireOp",EDGE,"E1.13.12.0"),sQuery(id+"F0.wireOp",EDGE,"E1.13.13.0"),sQuery(id+"F0.wireOp",EDGE,"E1.13.14.0"),sQuery(id+"F0.wireOp",EDGE,"E1.13.15.0"),sQuery(id+"F0.wireOp",EDGE,"E1.13.16.0"),sQuery(id+"F0.wireOp",EDGE,"E1.13.17.0"),sQuery(id+"F0.wireOp",EDGE,"E1.13.18.0"),sQuery(id+"F0.wireOp",EDGE,"E1.13.19.0"),sQuery(id+"F0.wireOp",EDGE,"E1.13.20.0"),sQuery(id+"F0.wireOp",EDGE,"E1.13.21.0"),sQuery(id+"F0.wireOp",EDGE,"E1.13.22.0"),sQuery(id+"F0.wireOp",EDGE,"E1.13.23.0"),sQuery(id+"F0.wireOp",EDGE,"E1.13.24.0"),sQuery(id+"F0.wireOp",EDGE,"E1.13.25.0"),sQuery(id+"F0.wireOp",EDGE,"E1.13.26.0"),sQuery(id+"F0.wireOp",EDGE,"E1.13.27.0"),sQuery(id+"F0.wireOp",EDGE,"E1.13.28.0"),sQuery(id+"F0.wireOp",EDGE,"E1.13.29.0"),sQuery(id+"F0.wireOp",EDGE,"E1.14.0.0"),sQuery(id+"F0.wireOp",EDGE,"E1.14.1.0"),sQuery(id+"F0.wireOp",EDGE,"E1.14.2.0"),sQuery(id+"F0.wireOp",EDGE,"E1.14.3.0"),sQuery(id+"F0.wireOp",EDGE,"E1.14.4.0"),sQuery(id+"F0.wireOp",EDGE,"E1.14.5.0"),sQuery(id+"F0.wireOp",EDGE,"E1.14.6.0"),sQuery(id+"F0.wireOp",EDGE,"E1.14.7.0"),sQuery(id+"F0.wireOp",EDGE,"E1.14.8.0"),sQuery(id+"F0.wireOp",EDGE,"E1.14.9.0"),sQuery(id+"F0.wireOp",EDGE,"E1.14.10.0"),sQuery(id+"F0.wireOp",EDGE,"E1.14.11.0"),sQuery(id+"F0.wireOp",EDGE,"E1.14.12.0"),sQuery(id+"F0.wireOp",EDGE,"E1.14.13.0"),sQuery(id+"F0.wireOp",EDGE,"E1.14.14.0"),sQuery(id+"F0.wireOp",EDGE,"E1.14.15.0"),sQuery(id+"F0.wireOp",EDGE,"E1.14.16.0"),sQuery(id+"F0.wireOp",EDGE,"E1.14.17.0"),sQuery(id+"F0.wireOp",EDGE,"E1.14.18.0"),sQuery(id+"F0.wireOp",EDGE,"E1.14.19.0"),sQuery(id+"F0.wireOp",EDGE,"E1.14.20.0"),sQuery(id+"F0.wireOp",EDGE,"E1.14.21.0"),sQuery(id+"F0.wireOp",EDGE,"E1.14.22.0"),sQuery(id+"F0.wireOp",EDGE,"E1.14.23.0"),sQuery(id+"F0.wireOp",EDGE,"E1.14.24.0"),sQuery(id+"F0.wireOp",EDGE,"E1.14.25.0"),sQuery(id+"F0.wireOp",EDGE,"E1.14.26.0"),sQuery(id+"F0.wireOp",EDGE,"E1.14.27.0"),sQuery(id+"F0.wireOp",EDGE,"E1.14.28.0"),sQuery(id+"F0.wireOp",EDGE,"E1.14.29.0"),sQuery(id+"F0.wireOp",EDGE,"E1.15.0.0"),sQuery(id+"F0.wireOp",EDGE,"E1.15.1.0"),sQuery(id+"F0.wireOp",EDGE,"E1.15.2.0"),sQuery(id+"F0.wireOp",EDGE,"E1.15.3.0"),sQuery(id+"F0.wireOp",EDGE,"E1.15.4.0"),sQuery(id+"F0.wireOp",EDGE,"E1.15.5.0"),sQuery(id+"F0.wireOp",EDGE,"E1.15.6.0"),sQuery(id+"F0.wireOp",EDGE,"E1.15.7.0"),sQuery(id+"F0.wireOp",EDGE,"E1.15.8.0"),sQuery(id+"F0.wireOp",EDGE,"E1.15.9.0"),sQuery(id+"F0.wireOp",EDGE,"E1.15.10.0"),sQuery(id+"F0.wireOp",EDGE,"E1.15.11.0"),sQuery(id+"F0.wireOp",EDGE,"E1.15.12.0"),sQuery(id+"F0.wireOp",EDGE,"E1.15.13.0"),sQuery(id+"F0.wireOp",EDGE,"E1.15.14.0"),sQuery(id+"F0.wireOp",EDGE,"E1.15.15.0"),sQuery(id+"F0.wireOp",EDGE,"E1.15.16.0"),sQuery(id+"F0.wireOp",EDGE,"E1.15.17.0"),sQuery(id+"F0.wireOp",EDGE,"E1.15.18.0"),sQuery(id+"F0.wireOp",EDGE,"E1.15.19.0"),sQuery(id+"F0.wireOp",EDGE,"E1.15.20.0"),sQuery(id+"F0.wireOp",EDGE,"E1.15.21.0"),sQuery(id+"F0.wireOp",EDGE,"E1.15.22.0"),sQuery(id+"F0.wireOp",EDGE,"E1.15.23.0"),sQuery(id+"F0.wireOp",EDGE,"E1.15.24.0"),sQuery(id+"F0.wireOp",EDGE,"E1.15.25.0"),sQuery(id+"F0.wireOp",EDGE,"E1.15.26.0"),sQuery(id+"F0.wireOp",EDGE,"E1.15.27.0"),sQuery(id+"F0.wireOp",EDGE,"E1.15.28.0"),sQuery(id+"F0.wireOp",EDGE,"E1.15.29.0"),sQuery(id+"F0.wireOp",EDGE,"E1.16.0.0"),sQuery(id+"F0.wireOp",EDGE,"E1.16.1.0"),sQuery(id+"F0.wireOp",EDGE,"E1.16.2.0"),sQuery(id+"F0.wireOp",EDGE,"E1.16.3.0"),sQuery(id+"F0.wireOp",EDGE,"E1.16.4.0"),sQuery(id+"F0.wireOp",EDGE,"E1.16.5.0"),sQuery(id+"F0.wireOp",EDGE,"E1.16.6.0"),sQuery(id+"F0.wireOp",EDGE,"E1.16.7.0"),sQuery(id+"F0.wireOp",EDGE,"E1.16.8.0"),sQuery(id+"F0.wireOp",EDGE,"E1.16.9.0"),sQuery(id+"F0.wireOp",EDGE,"E1.16.10.0"),sQuery(id+"F0.wireOp",EDGE,"E1.16.11.0"),sQuery(id+"F0.wireOp",EDGE,"E1.16.12.0"),sQuery(id+"F0.wireOp",EDGE,"E1.16.13.0"),sQuery(id+"F0.wireOp",EDGE,"E1.16.14.0"),sQuery(id+"F0.wireOp",EDGE,"E1.16.15.0"),sQuery(id+"F0.wireOp",EDGE,"E1.16.16.0"),sQuery(id+"F0.wireOp",EDGE,"E1.16.17.0"),sQuery(id+"F0.wireOp",EDGE,"E1.16.18.0"),sQuery(id+"F0.wireOp",EDGE,"E1.16.19.0"),sQuery(id+"F0.wireOp",EDGE,"E1.16.20.0"),sQuery(id+"F0.wireOp",EDGE,"E1.16.21.0"),sQuery(id+"F0.wireOp",EDGE,"E1.16.22.0"),sQuery(id+"F0.wireOp",EDGE,"E1.16.23.0"),sQuery(id+"F0.wireOp",EDGE,"E1.16.24.0"),sQuery(id+"F0.wireOp",EDGE,"E1.16.25.0"),sQuery(id+"F0.wireOp",EDGE,"E1.16.26.0"),sQuery(id+"F0.wireOp",EDGE,"E1.16.27.0"),sQuery(id+"F0.wireOp",EDGE,"E1.16.28.0"),sQuery(id+"F0.wireOp",EDGE,"E1.16.29.0"),sQuery(id+"F0.wireOp",EDGE,"E1.17.0.0"),sQuery(id+"F0.wireOp",EDGE,"E1.17.1.0"),sQuery(id+"F0.wireOp",EDGE,"E1.17.2.0"),sQuery(id+"F0.wireOp",EDGE,"E1.17.3.0"),sQuery(id+"F0.wireOp",EDGE,"E1.17.4.0"),sQuery(id+"F0.wireOp",EDGE,"E1.17.5.0"),sQuery(id+"F0.wireOp",EDGE,"E1.17.6.0"),sQuery(id+"F0.wireOp",EDGE,"E1.17.7.0"),sQuery(id+"F0.wireOp",EDGE,"E1.17.8.0"),sQuery(id+"F0.wireOp",EDGE,"E1.17.9.0"),sQuery(id+"F0.wireOp",EDGE,"E1.17.10.0"),sQuery(id+"F0.wireOp",EDGE,"E1.17.11.0"),sQuery(id+"F0.wireOp",EDGE,"E1.17.12.0"),sQuery(id+"F0.wireOp",EDGE,"E1.17.13.0"),sQuery(id+"F0.wireOp",EDGE,"E1.17.14.0"),sQuery(id+"F0.wireOp",EDGE,"E1.17.15.0"),sQuery(id+"F0.wireOp",EDGE,"E1.17.16.0"),sQuery(id+"F0.wireOp",EDGE,"E1.17.17.0"),sQuery(id+"F0.wireOp",EDGE,"E1.17.18.0"),sQuery(id+"F0.wireOp",EDGE,"E1.17.19.0"),sQuery(id+"F0.wireOp",EDGE,"E1.17.20.0"),sQuery(id+"F0.wireOp",EDGE,"E1.17.21.0"),sQuery(id+"F0.wireOp",EDGE,"E1.17.22.0"),sQuery(id+"F0.wireOp",EDGE,"E1.17.23.0"),sQuery(id+"F0.wireOp",EDGE,"E1.17.24.0"),sQuery(id+"F0.wireOp",EDGE,"E1.17.25.0"),sQuery(id+"F0.wireOp",EDGE,"E1.17.26.0"),sQuery(id+"F0.wireOp",EDGE,"E1.17.27.0"),sQuery(id+"F0.wireOp",EDGE,"E1.17.28.0"),sQuery(id+"F0.wireOp",EDGE,"E1.17.29.0"),sQuery(id+"F0.wireOp",EDGE,"E1.18.0.0"),sQuery(id+"F0.wireOp",EDGE,"E1.18.1.0"),sQuery(id+"F0.wireOp",EDGE,"E1.18.2.0"),sQuery(id+"F0.wireOp",EDGE,"E1.18.3.0"),sQuery(id+"F0.wireOp",EDGE,"E1.18.4.0"),sQuery(id+"F0.wireOp",EDGE,"E1.18.5.0"),sQuery(id+"F0.wireOp",EDGE,"E1.18.6.0"),sQuery(id+"F0.wireOp",EDGE,"E1.18.7.0"),sQuery(id+"F0.wireOp",EDGE,"E1.18.8.0"),sQuery(id+"F0.wireOp",EDGE,"E1.18.9.0"),sQuery(id+"F0.wireOp",EDGE,"E1.18.10.0"),sQuery(id+"F0.wireOp",EDGE,"E1.18.11.0"),sQuery(id+"F0.wireOp",EDGE,"E1.18.12.0"),sQuery(id+"F0.wireOp",EDGE,"E1.18.13.0"),sQuery(id+"F0.wireOp",EDGE,"E1.18.14.0"),sQuery(id+"F0.wireOp",EDGE,"E1.18.15.0"),sQuery(id+"F0.wireOp",EDGE,"E1.18.16.0"),sQuery(id+"F0.wireOp",EDGE,"E1.18.17.0"),sQuery(id+"F0.wireOp",EDGE,"E1.18.18.0"),sQuery(id+"F0.wireOp",EDGE,"E1.18.19.0"),sQuery(id+"F0.wireOp",EDGE,"E1.18.20.0"),sQuery(id+"F0.wireOp",EDGE,"E1.18.21.0"),sQuery(id+"F0.wireOp",EDGE,"E1.18.22.0"),sQuery(id+"F0.wireOp",EDGE,"E1.18.23.0"),sQuery(id+"F0.wireOp",EDGE,"E1.18.24.0"),sQuery(id+"F0.wireOp",EDGE,"E1.18.25.0"),sQuery(id+"F0.wireOp",EDGE,"E1.18.26.0"),sQuery(id+"F0.wireOp",EDGE,"E1.18.27.0"),sQuery(id+"F0.wireOp",EDGE,"E1.18.28.0"),sQuery(id+"F0.wireOp",EDGE,"E1.18.29.0"),sQuery(id+"F0.wireOp",EDGE,"E1.19.0.0"),sQuery(id+"F0.wireOp",EDGE,"E1.19.1.0"),sQuery(id+"F0.wireOp",EDGE,"E1.19.2.0"),sQuery(id+"F0.wireOp",EDGE,"E1.19.3.0"),sQuery(id+"F0.wireOp",EDGE,"E1.19.4.0"),sQuery(id+"F0.wireOp",EDGE,"E1.19.5.0"),sQuery(id+"F0.wireOp",EDGE,"E1.19.6.0"),sQuery(id+"F0.wireOp",EDGE,"E1.19.7.0"),sQuery(id+"F0.wireOp",EDGE,"E1.19.8.0"),sQuery(id+"F0.wireOp",EDGE,"E1.19.9.0"),sQuery(id+"F0.wireOp",EDGE,"E1.19.10.0"),sQuery(id+"F0.wireOp",EDGE,"E1.19.11.0"),sQuery(id+"F0.wireOp",EDGE,"E1.19.12.0"),sQuery(id+"F0.wireOp",EDGE,"E1.19.13.0"),sQuery(id+"F0.wireOp",EDGE,"E1.19.14.0"),sQuery(id+"F0.wireOp",EDGE,"E1.19.15.0"),sQuery(id+"F0.wireOp",EDGE,"E1.19.16.0"),sQuery(id+"F0.wireOp",EDGE,"E1.19.17.0"),sQuery(id+"F0.wireOp",EDGE,"E1.19.18.0"),sQuery(id+"F0.wireOp",EDGE,"E1.19.19.0"),sQuery(id+"F0.wireOp",EDGE,"E1.19.20.0"),sQuery(id+"F0.wireOp",EDGE,"E1.19.21.0"),sQuery(id+"F0.wireOp",EDGE,"E1.19.22.0"),sQuery(id+"F0.wireOp",EDGE,"E1.19.23.0"),sQuery(id+"F0.wireOp",EDGE,"E1.19.24.0"),sQuery(id+"F0.wireOp",EDGE,"E1.19.25.0"),sQuery(id+"F0.wireOp",EDGE,"E1.19.26.0"),sQuery(id+"F0.wireOp",EDGE,"E1.19.27.0"),sQuery(id+"F0.wireOp",EDGE,"E1.19.28.0"),sQuery(id+"F0.wireOp",EDGE,"E1.19.29.0"),sQuery(id+"F0.wireOp",EDGE,"E1.20.0.0"),sQuery(id+"F0.wireOp",EDGE,"E1.20.1.0"),sQuery(id+"F0.wireOp",EDGE,"E1.20.2.0"),sQuery(id+"F0.wireOp",EDGE,"E1.20.3.0"),sQuery(id+"F0.wireOp",EDGE,"E1.20.4.0"),sQuery(id+"F0.wireOp",EDGE,"E1.20.5.0"),sQuery(id+"F0.wireOp",EDGE,"E1.20.6.0"),sQuery(id+"F0.wireOp",EDGE,"E1.20.7.0"),sQuery(id+"F0.wireOp",EDGE,"E1.20.8.0"),sQuery(id+"F0.wireOp",EDGE,"E1.20.9.0"),sQuery(id+"F0.wireOp",EDGE,"E1.20.10.0"),sQuery(id+"F0.wireOp",EDGE,"E1.20.11.0"),sQuery(id+"F0.wireOp",EDGE,"E1.20.12.0"),sQuery(id+"F0.wireOp",EDGE,"E1.20.13.0"),sQuery(id+"F0.wireOp",EDGE,"E1.20.14.0"),sQuery(id+"F0.wireOp",EDGE,"E1.20.15.0"),sQuery(id+"F0.wireOp",EDGE,"E1.20.16.0"),sQuery(id+"F0.wireOp",EDGE,"E1.20.17.0"),sQuery(id+"F0.wireOp",EDGE,"E1.20.18.0"),sQuery(id+"F0.wireOp",EDGE,"E1.20.19.0"),sQuery(id+"F0.wireOp",EDGE,"E1.20.20.0"),sQuery(id+"F0.wireOp",EDGE,"E1.20.21.0"),sQuery(id+"F0.wireOp",EDGE,"E1.20.22.0"),sQuery(id+"F0.wireOp",EDGE,"E1.20.23.0"),sQuery(id+"F0.wireOp",EDGE,"E1.20.24.0"),sQuery(id+"F0.wireOp",EDGE,"E1.20.25.0"),sQuery(id+"F0.wireOp",EDGE,"E1.20.26.0"),sQuery(id+"F0.wireOp",EDGE,"E1.20.27.0"),sQuery(id+"F0.wireOp",EDGE,"E1.20.28.0"),sQuery(id+"F0.wireOp",EDGE,"E1.20.29.0"),sQuery(id+"F0.wireOp",EDGE,"E1.21.0.0"),sQuery(id+"F0.wireOp",EDGE,"E1.21.1.0"),sQuery(id+"F0.wireOp",EDGE,"E1.21.2.0"),sQuery(id+"F0.wireOp",EDGE,"E1.21.3.0"),sQuery(id+"F0.wireOp",EDGE,"E1.21.4.0"),sQuery(id+"F0.wireOp",EDGE,"E1.21.5.0"),sQuery(id+"F0.wireOp",EDGE,"E1.21.6.0"),sQuery(id+"F0.wireOp",EDGE,"E1.21.7.0"),sQuery(id+"F0.wireOp",EDGE,"E1.21.8.0"),sQuery(id+"F0.wireOp",EDGE,"E1.21.9.0"),sQuery(id+"F0.wireOp",EDGE,"E1.21.10.0"),sQuery(id+"F0.wireOp",EDGE,"E1.21.11.0"),sQuery(id+"F0.wireOp",EDGE,"E1.21.12.0"),sQuery(id+"F0.wireOp",EDGE,"E1.21.13.0"),sQuery(id+"F0.wireOp",EDGE,"E1.21.14.0"),sQuery(id+"F0.wireOp",EDGE,"E1.21.15.0"),sQuery(id+"F0.wireOp",EDGE,"E1.21.16.0"),sQuery(id+"F0.wireOp",EDGE,"E1.21.17.0"),sQuery(id+"F0.wireOp",EDGE,"E1.21.18.0"),sQuery(id+"F0.wireOp",EDGE,"E1.21.19.0"),sQuery(id+"F0.wireOp",EDGE,"E1.21.20.0"),sQuery(id+"F0.wireOp",EDGE,"E1.21.21.0"),sQuery(id+"F0.wireOp",EDGE,"E1.21.22.0"),sQuery(id+"F0.wireOp",EDGE,"E1.21.23.0"),sQuery(id+"F0.wireOp",EDGE,"E1.21.24.0"),sQuery(id+"F0.wireOp",EDGE,"E1.21.25.0"),sQuery(id+"F0.wireOp",EDGE,"E1.21.26.0"),sQuery(id+"F0.wireOp",EDGE,"E1.21.27.0"),sQuery(id+"F0.wireOp",EDGE,"E1.21.28.0"),sQuery(id+"F0.wireOp",EDGE,"E1.21.29.0"),sQuery(id+"F0.wireOp",EDGE,"E1.22.0.0"),sQuery(id+"F0.wireOp",EDGE,"E1.22.1.0"),sQuery(id+"F0.wireOp",EDGE,"E1.22.2.0"),sQuery(id+"F0.wireOp",EDGE,"E1.22.3.0"),sQuery(id+"F0.wireOp",EDGE,"E1.22.4.0"),sQuery(id+"F0.wireOp",EDGE,"E1.22.5.0"),sQuery(id+"F0.wireOp",EDGE,"E1.22.6.0"),sQuery(id+"F0.wireOp",EDGE,"E1.22.7.0"),sQuery(id+"F0.wireOp",EDGE,"E1.22.8.0"),sQuery(id+"F0.wireOp",EDGE,"E1.22.9.0"),sQuery(id+"F0.wireOp",EDGE,"E1.22.10.0"),sQuery(id+"F0.wireOp",EDGE,"E1.22.11.0"),sQuery(id+"F0.wireOp",EDGE,"E1.22.12.0"),sQuery(id+"F0.wireOp",EDGE,"E1.22.13.0"),sQuery(id+"F0.wireOp",EDGE,"E1.22.14.0"),sQuery(id+"F0.wireOp",EDGE,"E1.22.15.0"),sQuery(id+"F0.wireOp",EDGE,"E1.22.16.0"),sQuery(id+"F0.wireOp",EDGE,"E1.22.17.0"),sQuery(id+"F0.wireOp",EDGE,"E1.22.18.0"),sQuery(id+"F0.wireOp",EDGE,"E1.22.19.0"),sQuery(id+"F0.wireOp",EDGE,"E1.22.20.0"),sQuery(id+"F0.wireOp",EDGE,"E1.22.21.0"),sQuery(id+"F0.wireOp",EDGE,"E1.22.22.0"),sQuery(id+"F0.wireOp",EDGE,"E1.22.23.0"),sQuery(id+"F0.wireOp",EDGE,"E1.22.24.0"),sQuery(id+"F0.wireOp",EDGE,"E1.22.25.0"),sQuery(id+"F0.wireOp",EDGE,"E1.22.26.0"),sQuery(id+"F0.wireOp",EDGE,"E1.22.27.0"),sQuery(id+"F0.wireOp",EDGE,"E1.22.28.0"),sQuery(id+"F0.wireOp",EDGE,"E1.22.29.0"),sQuery(id+"F0.wireOp",EDGE,"E1.23.0.0"),sQuery(id+"F0.wireOp",EDGE,"E1.23.1.0"),sQuery(id+"F0.wireOp",EDGE,"E1.23.2.0"),sQuery(id+"F0.wireOp",EDGE,"E1.23.3.0"),sQuery(id+"F0.wireOp",EDGE,"E1.23.4.0"),sQuery(id+"F0.wireOp",EDGE,"E1.23.5.0"),sQuery(id+"F0.wireOp",EDGE,"E1.23.6.0"),sQuery(id+"F0.wireOp",EDGE,"E1.23.7.0"),sQuery(id+"F0.wireOp",EDGE,"E1.23.8.0"),sQuery(id+"F0.wireOp",EDGE,"E1.23.9.0"),sQuery(id+"F0.wireOp",EDGE,"E1.23.10.0"),sQuery(id+"F0.wireOp",EDGE,"E1.23.11.0"),sQuery(id+"F0.wireOp",EDGE,"E1.23.12.0"),sQuery(id+"F0.wireOp",EDGE,"E1.23.13.0"),sQuery(id+"F0.wireOp",EDGE,"E1.23.14.0"),sQuery(id+"F0.wireOp",EDGE,"E1.23.15.0"),sQuery(id+"F0.wireOp",EDGE,"E1.23.16.0"),sQuery(id+"F0.wireOp",EDGE,"E1.23.17.0"),sQuery(id+"F0.wireOp",EDGE,"E1.23.18.0"),sQuery(id+"F0.wireOp",EDGE,"E1.23.19.0"),sQuery(id+"F0.wireOp",EDGE,"E1.23.20.0"),sQuery(id+"F0.wireOp",EDGE,"E1.23.21.0"),sQuery(id+"F0.wireOp",EDGE,"E1.23.22.0"),sQuery(id+"F0.wireOp",EDGE,"E1.23.23.0"),sQuery(id+"F0.wireOp",EDGE,"E1.23.24.0"),sQuery(id+"F0.wireOp",EDGE,"E1.23.25.0"),sQuery(id+"F0.wireOp",EDGE,"E1.23.26.0"),sQuery(id+"F0.wireOp",EDGE,"E1.23.27.0"),sQuery(id+"F0.wireOp",EDGE,"E1.23.28.0"),sQuery(id+"F0.wireOp",EDGE,"E1.23.29.0"),sQuery(id+"F0.wireOp",EDGE,"E1.24.0.0"),sQuery(id+"F0.wireOp",EDGE,"E1.24.1.0"),sQuery(id+"F0.wireOp",EDGE,"E1.24.2.0"),sQuery(id+"F0.wireOp",EDGE,"E1.24.3.0"),sQuery(id+"F0.wireOp",EDGE,"E1.24.4.0"),sQuery(id+"F0.wireOp",EDGE,"E1.24.5.0"),sQuery(id+"F0.wireOp",EDGE,"E1.24.6.0"),sQuery(id+"F0.wireOp",EDGE,"E1.24.7.0"),sQuery(id+"F0.wireOp",EDGE,"E1.24.8.0"),sQuery(id+"F0.wireOp",EDGE,"E1.24.9.0"),sQuery(id+"F0.wireOp",EDGE,"E1.24.10.0"),sQuery(id+"F0.wireOp",EDGE,"E1.24.11.0"),sQuery(id+"F0.wireOp",EDGE,"E1.24.12.0"),sQuery(id+"F0.wireOp",EDGE,"E1.24.13.0"),sQuery(id+"F0.wireOp",EDGE,"E1.24.14.0"),sQuery(id+"F0.wireOp",EDGE,"E1.24.15.0"),sQuery(id+"F0.wireOp",EDGE,"E1.24.16.0"),sQuery(id+"F0.wireOp",EDGE,"E1.24.17.0"),sQuery(id+"F0.wireOp",EDGE,"E1.24.18.0"),sQuery(id+"F0.wireOp",EDGE,"E1.24.19.0"),sQuery(id+"F0.wireOp",EDGE,"E1.24.20.0"),sQuery(id+"F0.wireOp",EDGE,"E1.24.21.0"),sQuery(id+"F0.wireOp",EDGE,"E1.24.22.0"),sQuery(id+"F0.wireOp",EDGE,"E1.24.23.0"),sQuery(id+"F0.wireOp",EDGE,"E1.24.24.0"),sQuery(id+"F0.wireOp",EDGE,"E1.24.25.0"),sQuery(id+"F0.wireOp",EDGE,"E1.24.26.0"),sQuery(id+"F0.wireOp",EDGE,"E1.24.27.0"),sQuery(id+"F0.wireOp",EDGE,"E1.24.28.0"),sQuery(id+"F0.wireOp",EDGE,"E1.24.29.0"),sQuery(id+"F0.wireOp",EDGE,"E1.25.0.0"),sQuery(id+"F0.wireOp",EDGE,"E1.25.1.0"),sQuery(id+"F0.wireOp",EDGE,"E1.25.2.0"),sQuery(id+"F0.wireOp",EDGE,"E1.25.3.0"),sQuery(id+"F0.wireOp",EDGE,"E1.25.4.0"),sQuery(id+"F0.wireOp",EDGE,"E1.25.5.0"),sQuery(id+"F0.wireOp",EDGE,"E1.25.6.0"),sQuery(id+"F0.wireOp",EDGE,"E1.25.7.0"),sQuery(id+"F0.wireOp",EDGE,"E1.25.8.0"),sQuery(id+"F0.wireOp",EDGE,"E1.25.9.0"),sQuery(id+"F0.wireOp",EDGE,"E1.25.10.0"),sQuery(id+"F0.wireOp",EDGE,"E1.25.11.0"),sQuery(id+"F0.wireOp",EDGE,"E1.25.12.0"),sQuery(id+"F0.wireOp",EDGE,"E1.25.13.0"),sQuery(id+"F0.wireOp",EDGE,"E1.25.14.0"),sQuery(id+"F0.wireOp",EDGE,"E1.25.15.0"),sQuery(id+"F0.wireOp",EDGE,"E1.25.16.0"),sQuery(id+"F0.wireOp",EDGE,"E1.25.17.0"),sQuery(id+"F0.wireOp",EDGE,"E1.25.18.0"),sQuery(id+"F0.wireOp",EDGE,"E1.25.19.0"),sQuery(id+"F0.wireOp",EDGE,"E1.25.20.0"),sQuery(id+"F0.wireOp",EDGE,"E1.25.21.0"),sQuery(id+"F0.wireOp",EDGE,"E1.25.22.0"),sQuery(id+"F0.wireOp",EDGE,"E1.25.23.0"),sQuery(id+"F0.wireOp",EDGE,"E1.25.24.0"),sQuery(id+"F0.wireOp",EDGE,"E1.25.25.0"),sQuery(id+"F0.wireOp",EDGE,"E1.25.26.0"),sQuery(id+"F0.wireOp",EDGE,"E1.25.27.0"),sQuery(id+"F0.wireOp",EDGE,"E1.25.28.0"),sQuery(id+"F0.wireOp",EDGE,"E1.25.29.0"),sQuery(id+"F0.wireOp",EDGE,"E1.26.0.0"),sQuery(id+"F0.wireOp",EDGE,"E1.26.1.0"),sQuery(id+"F0.wireOp",EDGE,"E1.26.2.0"),sQuery(id+"F0.wireOp",EDGE,"E1.26.3.0"),sQuery(id+"F0.wireOp",EDGE,"E1.26.4.0"),sQuery(id+"F0.wireOp",EDGE,"E1.26.5.0"),sQuery(id+"F0.wireOp",EDGE,"E1.26.6.0"),sQuery(id+"F0.wireOp",EDGE,"E1.26.7.0"),sQuery(id+"F0.wireOp",EDGE,"E1.26.8.0"),sQuery(id+"F0.wireOp",EDGE,"E1.26.9.0"),sQuery(id+"F0.wireOp",EDGE,"E1.26.10.0"),sQuery(id+"F0.wireOp",EDGE,"E1.26.11.0"),sQuery(id+"F0.wireOp",EDGE,"E1.26.12.0"),sQuery(id+"F0.wireOp",EDGE,"E1.26.13.0"),sQuery(id+"F0.wireOp",EDGE,"E1.26.14.0"),sQuery(id+"F0.wireOp",EDGE,"E1.26.15.0"),sQuery(id+"F0.wireOp",EDGE,"E1.26.16.0"),sQuery(id+"F0.wireOp",EDGE,"E1.26.17.0"),sQuery(id+"F0.wireOp",EDGE,"E1.26.18.0"),sQuery(id+"F0.wireOp",EDGE,"E1.26.19.0"),sQuery(id+"F0.wireOp",EDGE,"E1.26.20.0"),sQuery(id+"F0.wireOp",EDGE,"E1.26.21.0"),sQuery(id+"F0.wireOp",EDGE,"E1.26.22.0"),sQuery(id+"F0.wireOp",EDGE,"E1.26.23.0"),sQuery(id+"F0.wireOp",EDGE,"E1.26.24.0"),sQuery(id+"F0.wireOp",EDGE,"E1.26.25.0"),sQuery(id+"F0.wireOp",EDGE,"E1.26.26.0"),sQuery(id+"F0.wireOp",EDGE,"E1.26.27.0"),sQuery(id+"F0.wireOp",EDGE,"E1.26.28.0"),sQuery(id+"F0.wireOp",EDGE,"E1.26.29.0"),sQuery(id+"F0.wireOp",EDGE,"E1.27.0.0"),sQuery(id+"F0.wireOp",EDGE,"E1.27.1.0"),sQuery(id+"F0.wireOp",EDGE,"E1.27.2.0"),sQuery(id+"F0.wireOp",EDGE,"E1.27.3.0"),sQuery(id+"F0.wireOp",EDGE,"E1.27.4.0"),sQuery(id+"F0.wireOp",EDGE,"E1.27.5.0"),sQuery(id+"F0.wireOp",EDGE,"E1.27.6.0"),sQuery(id+"F0.wireOp",EDGE,"E1.27.7.0"),sQuery(id+"F0.wireOp",EDGE,"E1.27.8.0"),sQuery(id+"F0.wireOp",EDGE,"E1.27.9.0"),sQuery(id+"F0.wireOp",EDGE,"E1.27.10.0"),sQuery(id+"F0.wireOp",EDGE,"E1.27.11.0"),sQuery(id+"F0.wireOp",EDGE,"E1.27.12.0"),sQuery(id+"F0.wireOp",EDGE,"E1.27.13.0"),sQuery(id+"F0.wireOp",EDGE,"E1.27.14.0"),sQuery(id+"F0.wireOp",EDGE,"E1.27.15.0"),sQuery(id+"F0.wireOp",EDGE,"E1.27.16.0"),sQuery(id+"F0.wireOp",EDGE,"E1.27.17.0"),sQuery(id+"F0.wireOp",EDGE,"E1.27.18.0"),sQuery(id+"F0.wireOp",EDGE,"E1.27.19.0"),sQuery(id+"F0.wireOp",EDGE,"E1.27.20.0"),sQuery(id+"F0.wireOp",EDGE,"E1.27.21.0"),sQuery(id+"F0.wireOp",EDGE,"E1.27.22.0"),sQuery(id+"F0.wireOp",EDGE,"E1.27.23.0"),sQuery(id+"F0.wireOp",EDGE,"E1.27.24.0"),sQuery(id+"F0.wireOp",EDGE,"E1.27.25.0"),sQuery(id+"F0.wireOp",EDGE,"E1.27.26.0"),sQuery(id+"F0.wireOp",EDGE,"E1.27.27.0"),sQuery(id+"F0.wireOp",EDGE,"E1.27.28.0"),sQuery(id+"F0.wireOp",EDGE,"E1.27.29.0"),sQuery(id+"F0.wireOp",EDGE,"E1.28.0.0"),sQuery(id+"F0.wireOp",EDGE,"E1.28.1.0"),sQuery(id+"F0.wireOp",EDGE,"E1.28.2.0"),sQuery(id+"F0.wireOp",EDGE,"E1.28.3.0"),sQuery(id+"F0.wireOp",EDGE,"E1.28.4.0"),sQuery(id+"F0.wireOp",EDGE,"E1.28.5.0"),sQuery(id+"F0.wireOp",EDGE,"E1.28.6.0"),sQuery(id+"F0.wireOp",EDGE,"E1.28.7.0"),sQuery(id+"F0.wireOp",EDGE,"E1.28.8.0"),sQuery(id+"F0.wireOp",EDGE,"E1.28.9.0"),sQuery(id+"F0.wireOp",EDGE,"E1.28.10.0"),sQuery(id+"F0.wireOp",EDGE,"E1.28.11.0"),sQuery(id+"F0.wireOp",EDGE,"E1.28.12.0"),sQuery(id+"F0.wireOp",EDGE,"E1.28.13.0"),sQuery(id+"F0.wireOp",EDGE,"E1.28.14.0"),sQuery(id+"F0.wireOp",EDGE,"E1.28.15.0"),sQuery(id+"F0.wireOp",EDGE,"E1.28.16.0"),sQuery(id+"F0.wireOp",EDGE,"E1.28.17.0"),sQuery(id+"F0.wireOp",EDGE,"E1.28.18.0"),sQuery(id+"F0.wireOp",EDGE,"E1.28.19.0"),sQuery(id+"F0.wireOp",EDGE,"E1.28.20.0"),sQuery(id+"F0.wireOp",EDGE,"E1.28.21.0"),sQuery(id+"F0.wireOp",EDGE,"E1.28.22.0"),sQuery(id+"F0.wireOp",EDGE,"E1.28.23.0"),sQuery(id+"F0.wireOp",EDGE,"E1.28.24.0"),sQuery(id+"F0.wireOp",EDGE,"E1.28.25.0"),sQuery(id+"F0.wireOp",EDGE,"E1.28.26.0"),sQuery(id+"F0.wireOp",EDGE,"E1.28.27.0"),sQuery(id+"F0.wireOp",EDGE,"E1.28.28.0"),sQuery(id+"F0.wireOp",EDGE,"E1.28.29.0"),sQuery(id+"F0.wireOp",EDGE,"E1.29.0.0"),sQuery(id+"F0.wireOp",EDGE,"E1.29.1.0"),sQuery(id+"F0.wireOp",EDGE,"E1.29.2.0"),sQuery(id+"F0.wireOp",EDGE,"E1.29.3.0"),sQuery(id+"F0.wireOp",EDGE,"E1.29.4.0"),sQuery(id+"F0.wireOp",EDGE,"E1.29.5.0"),sQuery(id+"F0.wireOp",EDGE,"E1.29.6.0"),sQuery(id+"F0.wireOp",EDGE,"E1.29.7.0"),sQuery(id+"F0.wireOp",EDGE,"E1.29.8.0"),sQuery(id+"F0.wireOp",EDGE,"E1.29.9.0"),sQuery(id+"F0.wireOp",EDGE,"E1.29.10.0"),sQuery(id+"F0.wireOp",EDGE,"E1.29.11.0"),sQuery(id+"F0.wireOp",EDGE,"E1.29.12.0"),sQuery(id+"F0.wireOp",EDGE,"E1.29.13.0"),sQuery(id+"F0.wireOp",EDGE,"E1.29.14.0"),sQuery(id+"F0.wireOp",EDGE,"E1.29.15.0"),sQuery(id+"F0.wireOp",EDGE,"E1.29.16.0"),sQuery(id+"F0.wireOp",EDGE,"E1.29.17.0"),sQuery(id+"F0.wireOp",EDGE,"E1.29.18.0"),sQuery(id+"F0.wireOp",EDGE,"E1.29.19.0"),sQuery(id+"F0.wireOp",EDGE,"E1.29.20.0"),sQuery(id+"F0.wireOp",EDGE,"E1.29.21.0"),sQuery(id+"F0.wireOp",EDGE,"E1.29.22.0"),sQuery(id+"F0.wireOp",EDGE,"E1.29.23.0"),sQuery(id+"F0.wireOp",EDGE,"E1.29.24.0"),sQuery(id+"F0.wireOp",EDGE,"E1.29.25.0"),sQuery(id+"F0.wireOp",EDGE,"E1.29.26.0"),sQuery(id+"F0.wireOp",EDGE,"E1.29.27.0"),sQuery(id+"F0.wireOp",EDGE,"E1.29.28.0"),sQuery(id+"F0.wireOp",EDGE,"E1.29.29.0"),sQuery(id+"F0.wireOp",EDGE,"E2.bottom"),sQuery(id+"F0.wireOp",EDGE,"E2.top"),sQuery(id+"F0.wireOp",EDGE,"E2.left"),sQuery(id+"F0.wireOp",EDGE,"E2.right")])],"isStart":true});
            extrude(context, id + "F3", {"entities" : qUnion([Q0]), "operationType" : NewBodyOperationType.ADD, "endBound" : BoundingType.UP_TO_SURFACE, "oppositeDirection" : true, "depth" : 1.4 * mm, "endBoundEntityFace" : qUnion([Q1]), "offsetDistance" : 25 * mm});
        }
        {
            var Q0;
            Q0=makeQuery(id+"F2.imprint","IMPRINT",FACE,{"disambiguationData":[TD([[makeQuery(id+"F2.imprint","IMPRINT",EDGE,{"derivedFrom":sQuery(id+"F2.wireOp",EDGE,"E3.bottom")}),-1.0]])]});
            extrude(context, id + "F4", {"entities" : qUnion([Q0]), "operationType" : NewBodyOperationType.ADD, "depth" : 30 * mm, "offsetDistance" : 25 * mm});
        }
    });
